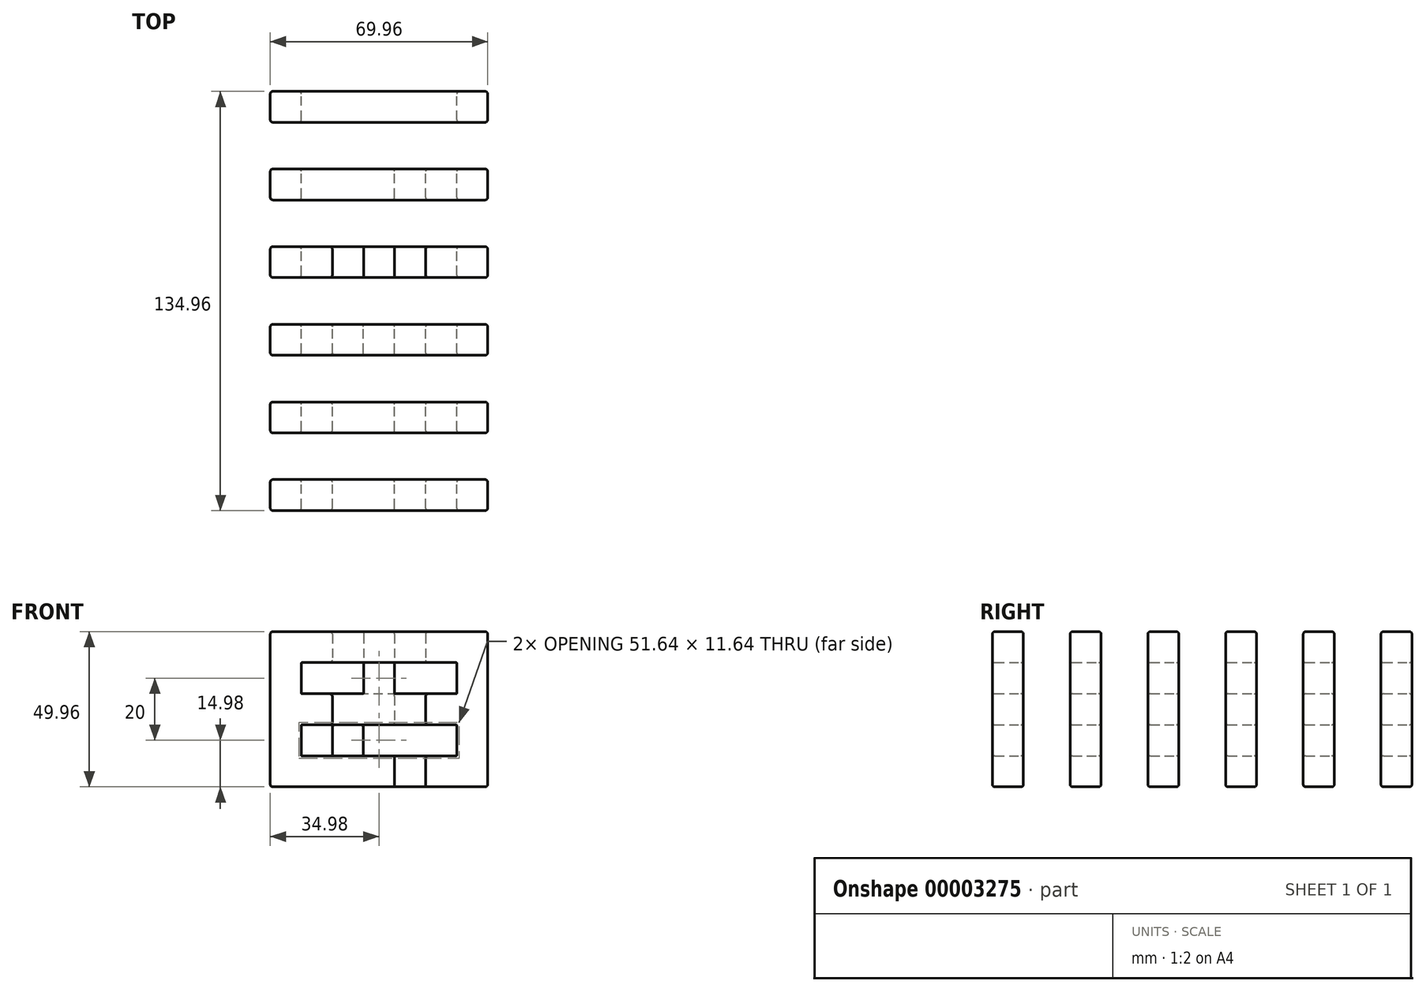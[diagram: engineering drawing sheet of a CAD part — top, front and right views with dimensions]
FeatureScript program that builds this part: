
annotation { "Feature Type Name" : "Feature", "Feature Type Description" : "" }
export const myFeature = defineFeature(function(context is Context, id is Id, definition is map)
    precondition{}
    {
        {
            var Q0;
            Q0=qCreatedBy(makeId("Front.planeOp"),FACE);
            var sketch = newSketch(context, id + "F0", { "sketchPlane" : qUnion([Q0])});
            skLineSegment(sketch, "E0", {"start": v(-35, 25) * mm, "end": v(-25, 25) * mm, "construction": true});
            skLineSegment(sketch, "E1", {"start": v(-25, 25) * mm, "end": v(-15, 25) * mm, "construction": true});
            skLineSegment(sketch, "E2", {"start": v(-15, 25) * mm, "end": v(-5, 25) * mm, "construction": true});
            skLineSegment(sketch, "E3", {"start": v(-5, 25) * mm, "end": v(5, 25) * mm, "construction": true});
            skLineSegment(sketch, "E4", {"start": v(5, 25) * mm, "end": v(15, 25) * mm, "construction": true});
            skLineSegment(sketch, "E5", {"start": v(15, 25) * mm, "end": v(25, 25) * mm, "construction": true});
            skLineSegment(sketch, "E6", {"start": v(25, 25) * mm, "end": v(35, 25) * mm, "construction": true});
            skLineSegment(sketch, "E7", {"start": v(-35, 25) * mm, "end": v(-35, 15) * mm, "construction": true});
            skLineSegment(sketch, "E8", {"start": v(-35, 15) * mm, "end": v(-35, 5) * mm, "construction": true});
            skLineSegment(sketch, "E9", {"start": v(-35, 5) * mm, "end": v(-35, -5) * mm, "construction": true});
            skLineSegment(sketch, "E10", {"start": v(-35, -5) * mm, "end": v(-35, -15) * mm, "construction": true});
            skLineSegment(sketch, "E11", {"start": v(-35, -15) * mm, "end": v(-35, -25) * mm, "construction": true});
            skLineSegment(sketch, "E12", {"start": v(-35, 25) * mm, "end": v(-34.98, 25) * mm, "construction": true});
            skLineSegment(sketch, "E13", {"start": v(-25.02, 25) * mm, "end": v(-25, 25) * mm, "construction": true});
            skLineSegment(sketch, "E14", {"start": v(-25, 25) * mm, "end": v(-24.98, 25) * mm, "construction": true});
            skLineSegment(sketch, "E15", {"start": v(-15.02, 25) * mm, "end": v(-15, 25) * mm, "construction": true});
            skLineSegment(sketch, "E16", {"start": v(-15, 25) * mm, "end": v(-14.98, 25) * mm, "construction": true});
            skLineSegment(sketch, "E17", {"start": v(-5, 25) * mm, "end": v(-5.02, 25) * mm, "construction": true});
            skLineSegment(sketch, "E18", {"start": v(-5, 25) * mm, "end": v(-4.98, 25) * mm, "construction": true});
            skLineSegment(sketch, "E19", {"start": v(5, 25) * mm, "end": v(4.98, 25) * mm, "construction": true});
            skLineSegment(sketch, "E20", {"start": v(5, 25) * mm, "end": v(5.02, 25) * mm, "construction": true});
            skLineSegment(sketch, "E21", {"start": v(15, 25) * mm, "end": v(14.98, 25) * mm, "construction": true});
            skLineSegment(sketch, "E22", {"start": v(15, 25) * mm, "end": v(15.02, 25) * mm, "construction": true});
            skLineSegment(sketch, "E23", {"start": v(25, 25) * mm, "end": v(24.98, 25) * mm, "construction": true});
            skLineSegment(sketch, "E24", {"start": v(25, 25) * mm, "end": v(25.02, 25) * mm, "construction": true});
            skLineSegment(sketch, "E25", {"start": v(35, 25) * mm, "end": v(34.98, 25) * mm, "construction": true});
            skLineSegment(sketch, "E26", {"start": v(-35, 25) * mm, "end": v(-35, 24.98) * mm, "construction": true});
            skLineSegment(sketch, "E27", {"start": v(-35, 15) * mm, "end": v(-35, 15.02) * mm, "construction": true});
            skLineSegment(sketch, "E28", {"start": v(-35, 15) * mm, "end": v(-35, 14.98) * mm, "construction": true});
            skLineSegment(sketch, "E29", {"start": v(-35, 5) * mm, "end": v(-35, 5.02) * mm, "construction": true});
            skLineSegment(sketch, "E30", {"start": v(-35, 5) * mm, "end": v(-35, 4.98) * mm, "construction": true});
            skLineSegment(sketch, "E31", {"start": v(-35, -5) * mm, "end": v(-35, -5.02) * mm, "construction": true});
            skLineSegment(sketch, "E32", {"start": v(-35, -5) * mm, "end": v(-35, -4.98) * mm, "construction": true});
            skLineSegment(sketch, "E33", {"start": v(-35, -15) * mm, "end": v(-35, -14.98) * mm, "construction": true});
            skLineSegment(sketch, "E34", {"start": v(-35, -15) * mm, "end": v(-35, -15.02) * mm, "construction": true});
            skLineSegment(sketch, "E35", {"start": v(-35, -25) * mm, "end": v(-35, -24.98) * mm, "construction": true});
            skLineSegment(sketch, "E36", {"start": v(-35, -24.98) * mm, "end": v(34.98, -24.98) * mm});
            skLineSegment(sketch, "E37", {"start": v(34.98, 25) * mm, "end": v(34.98, -24.98) * mm});
            skLineSegment(sketch, "E38", {"start": v(-35, -15.02) * mm, "end": v(34.98, -15.02) * mm});
            skLineSegment(sketch, "E39", {"start": v(-35, -14.98) * mm, "end": v(34.98, -14.98) * mm});
            skLineSegment(sketch, "E40", {"start": v(-35, -5.02) * mm, "end": v(34.98, -5.02) * mm});
            skLineSegment(sketch, "E41", {"start": v(-35, -4.98) * mm, "end": v(34.98, -4.98) * mm});
            skLineSegment(sketch, "E42", {"start": v(-35, 4.98) * mm, "end": v(34.98, 4.98) * mm});
            skLineSegment(sketch, "E43", {"start": v(-35, 5.02) * mm, "end": v(34.98, 5.02) * mm});
            skLineSegment(sketch, "E44", {"start": v(-35, 14.98) * mm, "end": v(34.98, 14.98) * mm});
            skLineSegment(sketch, "E45", {"start": v(-35, 15.02) * mm, "end": v(34.98, 15.02) * mm});
            skLineSegment(sketch, "E46", {"start": v(-35, 24.98) * mm, "end": v(34.98, 24.98) * mm});
            skLineSegment(sketch, "E47", {"start": v(-34.98, 25) * mm, "end": v(-34.98, -24.98) * mm});
            skLineSegment(sketch, "E48", {"start": v(-25.02, 25) * mm, "end": v(-25.02, -24.98) * mm});
            skLineSegment(sketch, "E49", {"start": v(-24.98, 25) * mm, "end": v(-24.98, -24.98) * mm});
            skLineSegment(sketch, "E50", {"start": v(-15.02, 25) * mm, "end": v(-15.02, -24.98) * mm});
            skLineSegment(sketch, "E51", {"start": v(-14.98, 25) * mm, "end": v(-14.98, -24.98) * mm});
            skLineSegment(sketch, "E52", {"start": v(-5.02, 25) * mm, "end": v(-5.02, -24.98) * mm});
            skLineSegment(sketch, "E53", {"start": v(-4.98, 25) * mm, "end": v(-4.98, -24.98) * mm});
            skLineSegment(sketch, "E54", {"start": v(4.98, 25) * mm, "end": v(4.98, -24.98) * mm});
            skLineSegment(sketch, "E55", {"start": v(5.02, 25) * mm, "end": v(5.02, -24.98) * mm});
            skLineSegment(sketch, "E56", {"start": v(14.98, 25) * mm, "end": v(14.98, -24.98) * mm});
            skLineSegment(sketch, "E57", {"start": v(15.02, 25) * mm, "end": v(15.02, -24.98) * mm});
            skLineSegment(sketch, "E58", {"start": v(24.98, 25) * mm, "end": v(24.98, -24.98) * mm});
            skLineSegment(sketch, "E59", {"start": v(25.02, 25) * mm, "end": v(25.02, -24.98) * mm});
            skLineSegment(sketch, "E60", {"start": v(-4.98, 4.98) * mm, "end": v(4.98, -4.98) * mm, "construction": true});
            skSolve(sketch);
        }
        {
            var Q0;
            {var subQ1=sQuery(id+"F0.wireOp",EDGE,"E45");var subQ5=sQuery(id+"F0.wireOp",EDGE,"E47");var subQ6=makeQuery(id+"F0.imprint","INTERSECT",VERTEX,{"derivedFrom":[subQ1,subQ5]});Q0=makeQuery(id+"F0.imprint","IMPRINT",FACE,{"disambiguationData":[TD([[makeQuery(id+"F0.imprint","IMPRINT",EDGE,{"disambiguationData":[TD([[subQ6,-1.0]])],"derivedFrom":subQ1}),1.0]])]});}
            var Q1;
            {var subQ1=sQuery(id+"F0.wireOp",EDGE,"E45");var subQ5=sQuery(id+"F0.wireOp",EDGE,"E48");var subQ6=makeQuery(id+"F0.imprint","INTERSECT",VERTEX,{"derivedFrom":[subQ1,subQ5]});Q1=makeQuery(id+"F0.imprint","IMPRINT",FACE,{"disambiguationData":[TD([[makeQuery(id+"F0.imprint","IMPRINT",EDGE,{"disambiguationData":[TD([[subQ6,-1.0]])],"derivedFrom":subQ1}),1.0]])]});}
            var Q2;
            {var subQ1=sQuery(id+"F0.wireOp",EDGE,"E45");var subQ5=sQuery(id+"F0.wireOp",EDGE,"E49");var subQ6=makeQuery(id+"F0.imprint","INTERSECT",VERTEX,{"derivedFrom":[subQ1,subQ5]});Q2=makeQuery(id+"F0.imprint","IMPRINT",FACE,{"disambiguationData":[TD([[makeQuery(id+"F0.imprint","IMPRINT",EDGE,{"disambiguationData":[TD([[subQ6,-1.0]])],"derivedFrom":subQ1}),1.0]])]});}
            var Q3;
            {var subQ1=sQuery(id+"F0.wireOp",EDGE,"E45");var subQ5=sQuery(id+"F0.wireOp",EDGE,"E50");var subQ6=makeQuery(id+"F0.imprint","INTERSECT",VERTEX,{"derivedFrom":[subQ1,subQ5]});Q3=makeQuery(id+"F0.imprint","IMPRINT",FACE,{"disambiguationData":[TD([[makeQuery(id+"F0.imprint","IMPRINT",EDGE,{"disambiguationData":[TD([[subQ6,-1.0]])],"derivedFrom":subQ1}),1.0]])]});}
            var Q4;
            {var subQ1=sQuery(id+"F0.wireOp",EDGE,"E45");var subQ5=sQuery(id+"F0.wireOp",EDGE,"E51");var subQ6=makeQuery(id+"F0.imprint","INTERSECT",VERTEX,{"derivedFrom":[subQ1,subQ5]});Q4=makeQuery(id+"F0.imprint","IMPRINT",FACE,{"disambiguationData":[TD([[makeQuery(id+"F0.imprint","IMPRINT",EDGE,{"disambiguationData":[TD([[subQ6,-1.0]])],"derivedFrom":subQ1}),1.0]])]});}
            var Q5;
            {var subQ1=sQuery(id+"F0.wireOp",EDGE,"E45");var subQ5=sQuery(id+"F0.wireOp",EDGE,"E52");var subQ6=makeQuery(id+"F0.imprint","INTERSECT",VERTEX,{"derivedFrom":[subQ1,subQ5]});Q5=makeQuery(id+"F0.imprint","IMPRINT",FACE,{"disambiguationData":[TD([[makeQuery(id+"F0.imprint","IMPRINT",EDGE,{"disambiguationData":[TD([[subQ6,-1.0]])],"derivedFrom":subQ1}),1.0]])]});}
            var Q6;
            {var subQ1=sQuery(id+"F0.wireOp",EDGE,"E45");var subQ5=sQuery(id+"F0.wireOp",EDGE,"E53");var subQ6=makeQuery(id+"F0.imprint","INTERSECT",VERTEX,{"derivedFrom":[subQ1,subQ5]});Q6=makeQuery(id+"F0.imprint","IMPRINT",FACE,{"disambiguationData":[TD([[makeQuery(id+"F0.imprint","IMPRINT",EDGE,{"disambiguationData":[TD([[subQ6,-1.0]])],"derivedFrom":subQ1}),1.0]])]});}
            var Q7;
            {var subQ1=sQuery(id+"F0.wireOp",EDGE,"E45");var subQ5=sQuery(id+"F0.wireOp",EDGE,"E54");var subQ6=makeQuery(id+"F0.imprint","INTERSECT",VERTEX,{"derivedFrom":[subQ1,subQ5]});Q7=makeQuery(id+"F0.imprint","IMPRINT",FACE,{"disambiguationData":[TD([[makeQuery(id+"F0.imprint","IMPRINT",EDGE,{"disambiguationData":[TD([[subQ6,-1.0]])],"derivedFrom":subQ1}),1.0]])]});}
            var Q8;
            {var subQ1=sQuery(id+"F0.wireOp",EDGE,"E45");var subQ5=sQuery(id+"F0.wireOp",EDGE,"E55");var subQ6=makeQuery(id+"F0.imprint","INTERSECT",VERTEX,{"derivedFrom":[subQ1,subQ5]});Q8=makeQuery(id+"F0.imprint","IMPRINT",FACE,{"disambiguationData":[TD([[makeQuery(id+"F0.imprint","IMPRINT",EDGE,{"disambiguationData":[TD([[subQ6,-1.0]])],"derivedFrom":subQ1}),1.0]])]});}
            var Q9;
            {var subQ0=sQuery(id+"F0.wireOp",EDGE,"E56");var subQ1=sQuery(id+"F0.wireOp",EDGE,"E45");var subQ2=makeQuery(id+"F0.imprint","INTERSECT",VERTEX,{"derivedFrom":[subQ1,subQ0]});Q9=makeQuery(id+"F0.imprint","IMPRINT",FACE,{"disambiguationData":[TD([[makeQuery(id+"F0.imprint","IMPRINT",EDGE,{"disambiguationData":[TD([[subQ2,-1.0]])],"derivedFrom":subQ1}),1.0]])]});}
            var Q10;
            {var subQ1=sQuery(id+"F0.wireOp",EDGE,"E45");var subQ5=sQuery(id+"F0.wireOp",EDGE,"E57");var subQ6=makeQuery(id+"F0.imprint","INTERSECT",VERTEX,{"derivedFrom":[subQ1,subQ5]});Q10=makeQuery(id+"F0.imprint","IMPRINT",FACE,{"disambiguationData":[TD([[makeQuery(id+"F0.imprint","IMPRINT",EDGE,{"disambiguationData":[TD([[subQ6,-1.0]])],"derivedFrom":subQ1}),1.0]])]});}
            var Q11;
            {var subQ0=sQuery(id+"F0.wireOp",EDGE,"E58");var subQ1=sQuery(id+"F0.wireOp",EDGE,"E45");var subQ2=makeQuery(id+"F0.imprint","INTERSECT",VERTEX,{"derivedFrom":[subQ1,subQ0]});Q11=makeQuery(id+"F0.imprint","IMPRINT",FACE,{"disambiguationData":[TD([[makeQuery(id+"F0.imprint","IMPRINT",EDGE,{"disambiguationData":[TD([[subQ2,-1.0]])],"derivedFrom":subQ1}),1.0]])]});}
            var Q12;
            {var subQ1=sQuery(id+"F0.wireOp",EDGE,"E45");var subQ5=sQuery(id+"F0.wireOp",EDGE,"E37");var subQ7=makeQuery(id+"F0.imprint","INTERSECT",VERTEX,{"derivedFrom":[subQ5,subQ1]});Q12=makeQuery(id+"F0.imprint","IMPRINT",FACE,{"disambiguationData":[TD([[makeQuery(id+"F0.imprint","IMPRINT",EDGE,{"disambiguationData":[TD([[subQ7,1.0]])],"derivedFrom":subQ5}),-1.0]])]});}
            var Q13;
            {var subQ3=sQuery(id+"F0.wireOp",EDGE,"E44");var subQ5=sQuery(id+"F0.wireOp",EDGE,"E37");var subQ7=makeQuery(id+"F0.imprint","INTERSECT",VERTEX,{"derivedFrom":[subQ5,subQ3]});Q13=makeQuery(id+"F0.imprint","IMPRINT",FACE,{"disambiguationData":[TD([[makeQuery(id+"F0.imprint","IMPRINT",EDGE,{"disambiguationData":[TD([[subQ7,1.0]])],"derivedFrom":subQ5}),-1.0]])]});}
            var Q14;
            {var subQ3=sQuery(id+"F0.wireOp",EDGE,"E43");var subQ5=sQuery(id+"F0.wireOp",EDGE,"E37");var subQ7=makeQuery(id+"F0.imprint","INTERSECT",VERTEX,{"derivedFrom":[subQ5,subQ3]});Q14=makeQuery(id+"F0.imprint","IMPRINT",FACE,{"disambiguationData":[TD([[makeQuery(id+"F0.imprint","IMPRINT",EDGE,{"disambiguationData":[TD([[subQ7,1.0]])],"derivedFrom":subQ5}),-1.0]])]});}
            var Q15;
            {var subQ3=sQuery(id+"F0.wireOp",EDGE,"E42");var subQ5=sQuery(id+"F0.wireOp",EDGE,"E37");var subQ7=makeQuery(id+"F0.imprint","INTERSECT",VERTEX,{"derivedFrom":[subQ5,subQ3]});Q15=makeQuery(id+"F0.imprint","IMPRINT",FACE,{"disambiguationData":[TD([[makeQuery(id+"F0.imprint","IMPRINT",EDGE,{"disambiguationData":[TD([[subQ7,1.0]])],"derivedFrom":subQ5}),-1.0]])]});}
            var Q16;
            {var subQ3=sQuery(id+"F0.wireOp",EDGE,"E41");var subQ5=sQuery(id+"F0.wireOp",EDGE,"E37");var subQ7=makeQuery(id+"F0.imprint","INTERSECT",VERTEX,{"derivedFrom":[subQ5,subQ3]});Q16=makeQuery(id+"F0.imprint","IMPRINT",FACE,{"disambiguationData":[TD([[makeQuery(id+"F0.imprint","IMPRINT",EDGE,{"disambiguationData":[TD([[subQ7,1.0]])],"derivedFrom":subQ5}),-1.0]])]});}
            var Q17;
            {var subQ3=sQuery(id+"F0.wireOp",EDGE,"E40");var subQ5=sQuery(id+"F0.wireOp",EDGE,"E37");var subQ7=makeQuery(id+"F0.imprint","INTERSECT",VERTEX,{"derivedFrom":[subQ5,subQ3]});Q17=makeQuery(id+"F0.imprint","IMPRINT",FACE,{"disambiguationData":[TD([[makeQuery(id+"F0.imprint","IMPRINT",EDGE,{"disambiguationData":[TD([[subQ7,1.0]])],"derivedFrom":subQ5}),-1.0]])]});}
            var Q18;
            {var subQ3=sQuery(id+"F0.wireOp",EDGE,"E39");var subQ5=sQuery(id+"F0.wireOp",EDGE,"E37");var subQ7=makeQuery(id+"F0.imprint","INTERSECT",VERTEX,{"derivedFrom":[subQ5,subQ3]});Q18=makeQuery(id+"F0.imprint","IMPRINT",FACE,{"disambiguationData":[TD([[makeQuery(id+"F0.imprint","IMPRINT",EDGE,{"disambiguationData":[TD([[subQ7,1.0]])],"derivedFrom":subQ5}),-1.0]])]});}
            var Q19;
            {var subQ3=sQuery(id+"F0.wireOp",EDGE,"E38");var subQ5=sQuery(id+"F0.wireOp",EDGE,"E37");var subQ7=makeQuery(id+"F0.imprint","INTERSECT",VERTEX,{"derivedFrom":[subQ5,subQ3]});Q19=makeQuery(id+"F0.imprint","IMPRINT",FACE,{"disambiguationData":[TD([[makeQuery(id+"F0.imprint","IMPRINT",EDGE,{"disambiguationData":[TD([[subQ7,1.0]])],"derivedFrom":subQ5}),-1.0]])]});}
            var Q20;
            {var subQ3=sQuery(id+"F0.wireOp",EDGE,"E36");var subQ5=sQuery(id+"F0.wireOp",EDGE,"E37");var subQ7=makeQuery(id+"F0.imprint","INTERSECT",VERTEX,{"derivedFrom":[subQ3,subQ5]});Q20=makeQuery(id+"F0.imprint","IMPRINT",FACE,{"disambiguationData":[TD([[makeQuery(id+"F0.imprint","IMPRINT",EDGE,{"disambiguationData":[TD([[subQ7,1.0]])],"derivedFrom":subQ3}),1.0]])]});}
            var Q21;
            {var subQ3=sQuery(id+"F0.wireOp",EDGE,"E36");var subQ5=sQuery(id+"F0.wireOp",EDGE,"E58");var subQ7=makeQuery(id+"F0.imprint","INTERSECT",VERTEX,{"derivedFrom":[subQ3,subQ5]});Q21=makeQuery(id+"F0.imprint","IMPRINT",FACE,{"disambiguationData":[TD([[makeQuery(id+"F0.imprint","IMPRINT",EDGE,{"disambiguationData":[TD([[subQ7,-1.0]])],"derivedFrom":subQ3}),1.0]])]});}
            var Q22;
            {var subQ3=sQuery(id+"F0.wireOp",EDGE,"E36");var subQ5=sQuery(id+"F0.wireOp",EDGE,"E57");var subQ7=makeQuery(id+"F0.imprint","INTERSECT",VERTEX,{"derivedFrom":[subQ3,subQ5]});Q22=makeQuery(id+"F0.imprint","IMPRINT",FACE,{"disambiguationData":[TD([[makeQuery(id+"F0.imprint","IMPRINT",EDGE,{"disambiguationData":[TD([[subQ7,-1.0]])],"derivedFrom":subQ3}),1.0]])]});}
            var Q23;
            {var subQ3=sQuery(id+"F0.wireOp",EDGE,"E36");var subQ5=sQuery(id+"F0.wireOp",EDGE,"E56");var subQ7=makeQuery(id+"F0.imprint","INTERSECT",VERTEX,{"derivedFrom":[subQ3,subQ5]});Q23=makeQuery(id+"F0.imprint","IMPRINT",FACE,{"disambiguationData":[TD([[makeQuery(id+"F0.imprint","IMPRINT",EDGE,{"disambiguationData":[TD([[subQ7,-1.0]])],"derivedFrom":subQ3}),1.0]])]});}
            var Q24;
            {var subQ3=sQuery(id+"F0.wireOp",EDGE,"E36");var subQ5=sQuery(id+"F0.wireOp",EDGE,"E49");var subQ7=makeQuery(id+"F0.imprint","INTERSECT",VERTEX,{"derivedFrom":[subQ3,subQ5]});Q24=makeQuery(id+"F0.imprint","IMPRINT",FACE,{"disambiguationData":[TD([[makeQuery(id+"F0.imprint","IMPRINT",EDGE,{"disambiguationData":[TD([[subQ7,-1.0]])],"derivedFrom":subQ3}),1.0]])]});}
            var Q25;
            {var subQ3=sQuery(id+"F0.wireOp",EDGE,"E36");var subQ5=sQuery(id+"F0.wireOp",EDGE,"E47");var subQ7=makeQuery(id+"F0.imprint","INTERSECT",VERTEX,{"derivedFrom":[subQ3,subQ5]});Q25=makeQuery(id+"F0.imprint","IMPRINT",FACE,{"disambiguationData":[TD([[makeQuery(id+"F0.imprint","IMPRINT",EDGE,{"disambiguationData":[TD([[subQ7,-1.0]])],"derivedFrom":subQ3}),1.0]])]});}
            var Q26;
            {var subQ3=sQuery(id+"F0.wireOp",EDGE,"E36");var subQ5=sQuery(id+"F0.wireOp",EDGE,"E48");var subQ7=makeQuery(id+"F0.imprint","INTERSECT",VERTEX,{"derivedFrom":[subQ3,subQ5]});Q26=makeQuery(id+"F0.imprint","IMPRINT",FACE,{"disambiguationData":[TD([[makeQuery(id+"F0.imprint","IMPRINT",EDGE,{"disambiguationData":[TD([[subQ7,-1.0]])],"derivedFrom":subQ3}),1.0]])]});}
            var Q27;
            {var subQ3=sQuery(id+"F0.wireOp",EDGE,"E36");var subQ5=sQuery(id+"F0.wireOp",EDGE,"E55");var subQ7=makeQuery(id+"F0.imprint","INTERSECT",VERTEX,{"derivedFrom":[subQ3,subQ5]});Q27=makeQuery(id+"F0.imprint","IMPRINT",FACE,{"disambiguationData":[TD([[makeQuery(id+"F0.imprint","IMPRINT",EDGE,{"disambiguationData":[TD([[subQ7,-1.0]])],"derivedFrom":subQ3}),1.0]])]});}
            var Q28;
            {var subQ3=sQuery(id+"F0.wireOp",EDGE,"E36");var subQ5=sQuery(id+"F0.wireOp",EDGE,"E54");var subQ7=makeQuery(id+"F0.imprint","INTERSECT",VERTEX,{"derivedFrom":[subQ3,subQ5]});Q28=makeQuery(id+"F0.imprint","IMPRINT",FACE,{"disambiguationData":[TD([[makeQuery(id+"F0.imprint","IMPRINT",EDGE,{"disambiguationData":[TD([[subQ7,-1.0]])],"derivedFrom":subQ3}),1.0]])]});}
            var Q29;
            {var subQ3=sQuery(id+"F0.wireOp",EDGE,"E36");var subQ5=sQuery(id+"F0.wireOp",EDGE,"E53");var subQ7=makeQuery(id+"F0.imprint","INTERSECT",VERTEX,{"derivedFrom":[subQ3,subQ5]});Q29=makeQuery(id+"F0.imprint","IMPRINT",FACE,{"disambiguationData":[TD([[makeQuery(id+"F0.imprint","IMPRINT",EDGE,{"disambiguationData":[TD([[subQ7,-1.0]])],"derivedFrom":subQ3}),1.0]])]});}
            var Q30;
            {var subQ3=sQuery(id+"F0.wireOp",EDGE,"E36");var subQ5=sQuery(id+"F0.wireOp",EDGE,"E52");var subQ7=makeQuery(id+"F0.imprint","INTERSECT",VERTEX,{"derivedFrom":[subQ3,subQ5]});Q30=makeQuery(id+"F0.imprint","IMPRINT",FACE,{"disambiguationData":[TD([[makeQuery(id+"F0.imprint","IMPRINT",EDGE,{"disambiguationData":[TD([[subQ7,-1.0]])],"derivedFrom":subQ3}),1.0]])]});}
            var Q31;
            {var subQ3=sQuery(id+"F0.wireOp",EDGE,"E36");var subQ5=sQuery(id+"F0.wireOp",EDGE,"E51");var subQ7=makeQuery(id+"F0.imprint","INTERSECT",VERTEX,{"derivedFrom":[subQ3,subQ5]});Q31=makeQuery(id+"F0.imprint","IMPRINT",FACE,{"disambiguationData":[TD([[makeQuery(id+"F0.imprint","IMPRINT",EDGE,{"disambiguationData":[TD([[subQ7,-1.0]])],"derivedFrom":subQ3}),1.0]])]});}
            var Q32;
            {var subQ3=sQuery(id+"F0.wireOp",EDGE,"E36");var subQ5=sQuery(id+"F0.wireOp",EDGE,"E50");var subQ7=makeQuery(id+"F0.imprint","INTERSECT",VERTEX,{"derivedFrom":[subQ3,subQ5]});Q32=makeQuery(id+"F0.imprint","IMPRINT",FACE,{"disambiguationData":[TD([[makeQuery(id+"F0.imprint","IMPRINT",EDGE,{"disambiguationData":[TD([[subQ7,-1.0]])],"derivedFrom":subQ3}),1.0]])]});}
            var Q33;
            {var subQ3=sQuery(id+"F0.wireOp",EDGE,"E40");var subQ5=sQuery(id+"F0.wireOp",EDGE,"E47");var subQ7=makeQuery(id+"F0.imprint","INTERSECT",VERTEX,{"derivedFrom":[subQ3,subQ5]});Q33=makeQuery(id+"F0.imprint","IMPRINT",FACE,{"disambiguationData":[TD([[makeQuery(id+"F0.imprint","IMPRINT",EDGE,{"disambiguationData":[TD([[subQ7,-1.0]])],"derivedFrom":subQ3}),1.0]])]});}
            var Q34;
            {var subQ3=sQuery(id+"F0.wireOp",EDGE,"E41");var subQ5=sQuery(id+"F0.wireOp",EDGE,"E47");var subQ7=makeQuery(id+"F0.imprint","INTERSECT",VERTEX,{"derivedFrom":[subQ3,subQ5]});Q34=makeQuery(id+"F0.imprint","IMPRINT",FACE,{"disambiguationData":[TD([[makeQuery(id+"F0.imprint","IMPRINT",EDGE,{"disambiguationData":[TD([[subQ7,-1.0]])],"derivedFrom":subQ3}),1.0]])]});}
            var Q35;
            {var subQ3=sQuery(id+"F0.wireOp",EDGE,"E44");var subQ5=sQuery(id+"F0.wireOp",EDGE,"E47");var subQ7=makeQuery(id+"F0.imprint","INTERSECT",VERTEX,{"derivedFrom":[subQ3,subQ5]});Q35=makeQuery(id+"F0.imprint","IMPRINT",FACE,{"disambiguationData":[TD([[makeQuery(id+"F0.imprint","IMPRINT",EDGE,{"disambiguationData":[TD([[subQ7,-1.0]])],"derivedFrom":subQ3}),1.0]])]});}
            var Q36;
            {var subQ3=sQuery(id+"F0.wireOp",EDGE,"E42");var subQ5=sQuery(id+"F0.wireOp",EDGE,"E47");var subQ7=makeQuery(id+"F0.imprint","INTERSECT",VERTEX,{"derivedFrom":[subQ3,subQ5]});Q36=makeQuery(id+"F0.imprint","IMPRINT",FACE,{"disambiguationData":[TD([[makeQuery(id+"F0.imprint","IMPRINT",EDGE,{"disambiguationData":[TD([[subQ7,-1.0]])],"derivedFrom":subQ3}),1.0]])]});}
            var Q37;
            {var subQ3=sQuery(id+"F0.wireOp",EDGE,"E38");var subQ5=sQuery(id+"F0.wireOp",EDGE,"E47");var subQ7=makeQuery(id+"F0.imprint","INTERSECT",VERTEX,{"derivedFrom":[subQ3,subQ5]});Q37=makeQuery(id+"F0.imprint","IMPRINT",FACE,{"disambiguationData":[TD([[makeQuery(id+"F0.imprint","IMPRINT",EDGE,{"disambiguationData":[TD([[subQ7,-1.0]])],"derivedFrom":subQ3}),1.0]])]});}
            var Q38;
            {var subQ3=sQuery(id+"F0.wireOp",EDGE,"E39");var subQ5=sQuery(id+"F0.wireOp",EDGE,"E47");var subQ7=makeQuery(id+"F0.imprint","INTERSECT",VERTEX,{"derivedFrom":[subQ3,subQ5]});Q38=makeQuery(id+"F0.imprint","IMPRINT",FACE,{"disambiguationData":[TD([[makeQuery(id+"F0.imprint","IMPRINT",EDGE,{"disambiguationData":[TD([[subQ7,-1.0]])],"derivedFrom":subQ3}),1.0]])]});}
            var Q39;
            {var subQ3=sQuery(id+"F0.wireOp",EDGE,"E43");var subQ5=sQuery(id+"F0.wireOp",EDGE,"E47");var subQ7=makeQuery(id+"F0.imprint","INTERSECT",VERTEX,{"derivedFrom":[subQ3,subQ5]});Q39=makeQuery(id+"F0.imprint","IMPRINT",FACE,{"disambiguationData":[TD([[makeQuery(id+"F0.imprint","IMPRINT",EDGE,{"disambiguationData":[TD([[subQ7,-1.0]])],"derivedFrom":subQ3}),1.0]])]});}
            var Q40;
            {var subQ3=sQuery(id+"F0.wireOp",EDGE,"E41");var subQ5=sQuery(id+"F0.wireOp",EDGE,"E56");var subQ7=makeQuery(id+"F0.imprint","INTERSECT",VERTEX,{"derivedFrom":[subQ3,subQ5]});Q40=makeQuery(id+"F0.imprint","IMPRINT",FACE,{"disambiguationData":[TD([[makeQuery(id+"F0.imprint","IMPRINT",EDGE,{"disambiguationData":[TD([[subQ7,-1.0]])],"derivedFrom":subQ3}),1.0]])]});}
            var Q41;
            {var subQ3=sQuery(id+"F0.wireOp",EDGE,"E41");var subQ5=sQuery(id+"F0.wireOp",EDGE,"E57");var subQ7=makeQuery(id+"F0.imprint","INTERSECT",VERTEX,{"derivedFrom":[subQ3,subQ5]});Q41=makeQuery(id+"F0.imprint","IMPRINT",FACE,{"disambiguationData":[TD([[makeQuery(id+"F0.imprint","IMPRINT",EDGE,{"disambiguationData":[TD([[subQ7,-1.0]])],"derivedFrom":subQ3}),1.0]])]});}
            var Q42;
            {var subQ3=sQuery(id+"F0.wireOp",EDGE,"E41");var subQ5=sQuery(id+"F0.wireOp",EDGE,"E52");var subQ7=makeQuery(id+"F0.imprint","INTERSECT",VERTEX,{"derivedFrom":[subQ3,subQ5]});Q42=makeQuery(id+"F0.imprint","IMPRINT",FACE,{"disambiguationData":[TD([[makeQuery(id+"F0.imprint","IMPRINT",EDGE,{"disambiguationData":[TD([[subQ7,-1.0]])],"derivedFrom":subQ3}),1.0]])]});}
            var Q43;
            {var subQ3=sQuery(id+"F0.wireOp",EDGE,"E41");var subQ5=sQuery(id+"F0.wireOp",EDGE,"E48");var subQ7=makeQuery(id+"F0.imprint","INTERSECT",VERTEX,{"derivedFrom":[subQ3,subQ5]});Q43=makeQuery(id+"F0.imprint","IMPRINT",FACE,{"disambiguationData":[TD([[makeQuery(id+"F0.imprint","IMPRINT",EDGE,{"disambiguationData":[TD([[subQ7,-1.0]])],"derivedFrom":subQ3}),1.0]])]});}
            var Q44;
            {var subQ3=sQuery(id+"F0.wireOp",EDGE,"E41");var subQ5=sQuery(id+"F0.wireOp",EDGE,"E51");var subQ7=makeQuery(id+"F0.imprint","INTERSECT",VERTEX,{"derivedFrom":[subQ3,subQ5]});Q44=makeQuery(id+"F0.imprint","IMPRINT",FACE,{"disambiguationData":[TD([[makeQuery(id+"F0.imprint","IMPRINT",EDGE,{"disambiguationData":[TD([[subQ7,-1.0]])],"derivedFrom":subQ3}),1.0]])]});}
            var Q45;
            {var subQ3=sQuery(id+"F0.wireOp",EDGE,"E41");var subQ5=sQuery(id+"F0.wireOp",EDGE,"E54");var subQ7=makeQuery(id+"F0.imprint","INTERSECT",VERTEX,{"derivedFrom":[subQ3,subQ5]});Q45=makeQuery(id+"F0.imprint","IMPRINT",FACE,{"disambiguationData":[TD([[makeQuery(id+"F0.imprint","IMPRINT",EDGE,{"disambiguationData":[TD([[subQ7,-1.0]])],"derivedFrom":subQ3}),1.0]])]});}
            var Q46;
            {var subQ3=sQuery(id+"F0.wireOp",EDGE,"E41");var subQ5=sQuery(id+"F0.wireOp",EDGE,"E49");var subQ7=makeQuery(id+"F0.imprint","INTERSECT",VERTEX,{"derivedFrom":[subQ3,subQ5]});Q46=makeQuery(id+"F0.imprint","IMPRINT",FACE,{"disambiguationData":[TD([[makeQuery(id+"F0.imprint","IMPRINT",EDGE,{"disambiguationData":[TD([[subQ7,-1.0]])],"derivedFrom":subQ3}),1.0]])]});}
            var Q47;
            {var subQ3=sQuery(id+"F0.wireOp",EDGE,"E41");var subQ5=sQuery(id+"F0.wireOp",EDGE,"E50");var subQ7=makeQuery(id+"F0.imprint","INTERSECT",VERTEX,{"derivedFrom":[subQ3,subQ5]});Q47=makeQuery(id+"F0.imprint","IMPRINT",FACE,{"disambiguationData":[TD([[makeQuery(id+"F0.imprint","IMPRINT",EDGE,{"disambiguationData":[TD([[subQ7,-1.0]])],"derivedFrom":subQ3}),1.0]])]});}
            var Q48;
            {var subQ3=sQuery(id+"F0.wireOp",EDGE,"E41");var subQ5=sQuery(id+"F0.wireOp",EDGE,"E55");var subQ7=makeQuery(id+"F0.imprint","INTERSECT",VERTEX,{"derivedFrom":[subQ3,subQ5]});Q48=makeQuery(id+"F0.imprint","IMPRINT",FACE,{"disambiguationData":[TD([[makeQuery(id+"F0.imprint","IMPRINT",EDGE,{"disambiguationData":[TD([[subQ7,-1.0]])],"derivedFrom":subQ3}),1.0]])]});}
            var Q49;
            {var subQ3=sQuery(id+"F0.wireOp",EDGE,"E41");var subQ5=sQuery(id+"F0.wireOp",EDGE,"E53");var subQ7=makeQuery(id+"F0.imprint","INTERSECT",VERTEX,{"derivedFrom":[subQ3,subQ5]});Q49=makeQuery(id+"F0.imprint","IMPRINT",FACE,{"disambiguationData":[TD([[makeQuery(id+"F0.imprint","IMPRINT",EDGE,{"disambiguationData":[TD([[subQ7,-1.0]])],"derivedFrom":subQ3}),1.0]])]});}
            var Q50;
            {var subQ0=sQuery(id+"F0.wireOp",EDGE,"E58");var subQ3=sQuery(id+"F0.wireOp",EDGE,"E41");var subQ4=makeQuery(id+"F0.imprint","INTERSECT",VERTEX,{"derivedFrom":[subQ3,subQ0]});Q50=makeQuery(id+"F0.imprint","IMPRINT",FACE,{"disambiguationData":[TD([[makeQuery(id+"F0.imprint","IMPRINT",EDGE,{"disambiguationData":[TD([[subQ4,-1.0]])],"derivedFrom":subQ3}),1.0]])]});}
            extrude(context, id + "F1", {"entities" : qUnion([Q0, Q1, Q2, Q3, Q4, Q5, Q6, Q7, Q8, Q9, Q10, Q11, Q12, Q13, Q14, Q15, Q16, Q17, Q18, Q19, Q20, Q21, Q22, Q23, Q24, Q25, Q26, Q27, Q28, Q29, Q30, Q31, Q32, Q33, Q34, Q35, Q36, Q37, Q38, Q39, Q40, Q41, Q42, Q43, Q44, Q45, Q46, Q47, Q48, Q49, Q50]), "endBound" : BoundingType.SYMMETRIC, "depth" : 9.96 * mm});
        }
        {
            var Q0;
            {var subQ1=sQuery(id+"F0.wireOp",EDGE,"E45");var subQ5=sQuery(id+"F0.wireOp",EDGE,"E53");var subQ6=makeQuery(id+"F0.imprint","INTERSECT",VERTEX,{"derivedFrom":[subQ1,subQ5]});Q0=makeQuery(id+"F0.imprint","IMPRINT",FACE,{"disambiguationData":[TD([[makeQuery(id+"F0.imprint","IMPRINT",EDGE,{"disambiguationData":[TD([[subQ6,-1.0]])],"derivedFrom":subQ1}),1.0]])]});}
            var Q1;
            {var subQ1=sQuery(id+"F0.wireOp",EDGE,"E45");var subQ5=sQuery(id+"F0.wireOp",EDGE,"E48");var subQ6=makeQuery(id+"F0.imprint","INTERSECT",VERTEX,{"derivedFrom":[subQ1,subQ5]});Q1=makeQuery(id+"F0.imprint","IMPRINT",FACE,{"disambiguationData":[TD([[makeQuery(id+"F0.imprint","IMPRINT",EDGE,{"disambiguationData":[TD([[subQ6,-1.0]])],"derivedFrom":subQ1}),1.0]])]});}
            var Q2;
            {var subQ1=sQuery(id+"F0.wireOp",EDGE,"E45");var subQ5=sQuery(id+"F0.wireOp",EDGE,"E52");var subQ6=makeQuery(id+"F0.imprint","INTERSECT",VERTEX,{"derivedFrom":[subQ1,subQ5]});Q2=makeQuery(id+"F0.imprint","IMPRINT",FACE,{"disambiguationData":[TD([[makeQuery(id+"F0.imprint","IMPRINT",EDGE,{"disambiguationData":[TD([[subQ6,-1.0]])],"derivedFrom":subQ1}),1.0]])]});}
            var Q3;
            {var subQ1=sQuery(id+"F0.wireOp",EDGE,"E45");var subQ5=sQuery(id+"F0.wireOp",EDGE,"E47");var subQ6=makeQuery(id+"F0.imprint","INTERSECT",VERTEX,{"derivedFrom":[subQ1,subQ5]});Q3=makeQuery(id+"F0.imprint","IMPRINT",FACE,{"disambiguationData":[TD([[makeQuery(id+"F0.imprint","IMPRINT",EDGE,{"disambiguationData":[TD([[subQ6,-1.0]])],"derivedFrom":subQ1}),1.0]])]});}
            var Q4;
            {var subQ1=sQuery(id+"F0.wireOp",EDGE,"E45");var subQ5=sQuery(id+"F0.wireOp",EDGE,"E54");var subQ6=makeQuery(id+"F0.imprint","INTERSECT",VERTEX,{"derivedFrom":[subQ1,subQ5]});Q4=makeQuery(id+"F0.imprint","IMPRINT",FACE,{"disambiguationData":[TD([[makeQuery(id+"F0.imprint","IMPRINT",EDGE,{"disambiguationData":[TD([[subQ6,-1.0]])],"derivedFrom":subQ1}),1.0]])]});}
            var Q5;
            {var subQ1=sQuery(id+"F0.wireOp",EDGE,"E45");var subQ5=sQuery(id+"F0.wireOp",EDGE,"E37");var subQ7=makeQuery(id+"F0.imprint","INTERSECT",VERTEX,{"derivedFrom":[subQ5,subQ1]});Q5=makeQuery(id+"F0.imprint","IMPRINT",FACE,{"disambiguationData":[TD([[makeQuery(id+"F0.imprint","IMPRINT",EDGE,{"disambiguationData":[TD([[subQ7,1.0]])],"derivedFrom":subQ5}),-1.0]])]});}
            var Q6;
            {var subQ1=sQuery(id+"F0.wireOp",EDGE,"E45");var subQ5=sQuery(id+"F0.wireOp",EDGE,"E55");var subQ6=makeQuery(id+"F0.imprint","INTERSECT",VERTEX,{"derivedFrom":[subQ1,subQ5]});Q6=makeQuery(id+"F0.imprint","IMPRINT",FACE,{"disambiguationData":[TD([[makeQuery(id+"F0.imprint","IMPRINT",EDGE,{"disambiguationData":[TD([[subQ6,-1.0]])],"derivedFrom":subQ1}),1.0]])]});}
            var Q7;
            {var subQ1=sQuery(id+"F0.wireOp",EDGE,"E45");var subQ5=sQuery(id+"F0.wireOp",EDGE,"E50");var subQ6=makeQuery(id+"F0.imprint","INTERSECT",VERTEX,{"derivedFrom":[subQ1,subQ5]});Q7=makeQuery(id+"F0.imprint","IMPRINT",FACE,{"disambiguationData":[TD([[makeQuery(id+"F0.imprint","IMPRINT",EDGE,{"disambiguationData":[TD([[subQ6,-1.0]])],"derivedFrom":subQ1}),1.0]])]});}
            var Q8;
            {var subQ1=sQuery(id+"F0.wireOp",EDGE,"E45");var subQ5=sQuery(id+"F0.wireOp",EDGE,"E57");var subQ6=makeQuery(id+"F0.imprint","INTERSECT",VERTEX,{"derivedFrom":[subQ1,subQ5]});Q8=makeQuery(id+"F0.imprint","IMPRINT",FACE,{"disambiguationData":[TD([[makeQuery(id+"F0.imprint","IMPRINT",EDGE,{"disambiguationData":[TD([[subQ6,-1.0]])],"derivedFrom":subQ1}),1.0]])]});}
            var Q9;
            {var subQ0=sQuery(id+"F0.wireOp",EDGE,"E58");var subQ1=sQuery(id+"F0.wireOp",EDGE,"E45");var subQ2=makeQuery(id+"F0.imprint","INTERSECT",VERTEX,{"derivedFrom":[subQ1,subQ0]});Q9=makeQuery(id+"F0.imprint","IMPRINT",FACE,{"disambiguationData":[TD([[makeQuery(id+"F0.imprint","IMPRINT",EDGE,{"disambiguationData":[TD([[subQ2,-1.0]])],"derivedFrom":subQ1}),1.0]])]});}
            var Q10;
            {var subQ0=sQuery(id+"F0.wireOp",EDGE,"E56");var subQ1=sQuery(id+"F0.wireOp",EDGE,"E45");var subQ2=makeQuery(id+"F0.imprint","INTERSECT",VERTEX,{"derivedFrom":[subQ1,subQ0]});Q10=makeQuery(id+"F0.imprint","IMPRINT",FACE,{"disambiguationData":[TD([[makeQuery(id+"F0.imprint","IMPRINT",EDGE,{"disambiguationData":[TD([[subQ2,-1.0]])],"derivedFrom":subQ1}),1.0]])]});}
            var Q11;
            {var subQ1=sQuery(id+"F0.wireOp",EDGE,"E45");var subQ5=sQuery(id+"F0.wireOp",EDGE,"E51");var subQ6=makeQuery(id+"F0.imprint","INTERSECT",VERTEX,{"derivedFrom":[subQ1,subQ5]});Q11=makeQuery(id+"F0.imprint","IMPRINT",FACE,{"disambiguationData":[TD([[makeQuery(id+"F0.imprint","IMPRINT",EDGE,{"disambiguationData":[TD([[subQ6,-1.0]])],"derivedFrom":subQ1}),1.0]])]});}
            var Q12;
            {var subQ1=sQuery(id+"F0.wireOp",EDGE,"E45");var subQ5=sQuery(id+"F0.wireOp",EDGE,"E49");var subQ6=makeQuery(id+"F0.imprint","INTERSECT",VERTEX,{"derivedFrom":[subQ1,subQ5]});Q12=makeQuery(id+"F0.imprint","IMPRINT",FACE,{"disambiguationData":[TD([[makeQuery(id+"F0.imprint","IMPRINT",EDGE,{"disambiguationData":[TD([[subQ6,-1.0]])],"derivedFrom":subQ1}),1.0]])]});}
            var Q13;
            {var subQ3=sQuery(id+"F0.wireOp",EDGE,"E39");var subQ5=sQuery(id+"F0.wireOp",EDGE,"E37");var subQ7=makeQuery(id+"F0.imprint","INTERSECT",VERTEX,{"derivedFrom":[subQ5,subQ3]});Q13=makeQuery(id+"F0.imprint","IMPRINT",FACE,{"disambiguationData":[TD([[makeQuery(id+"F0.imprint","IMPRINT",EDGE,{"disambiguationData":[TD([[subQ7,1.0]])],"derivedFrom":subQ5}),-1.0]])]});}
            var Q14;
            {var subQ3=sQuery(id+"F0.wireOp",EDGE,"E36");var subQ5=sQuery(id+"F0.wireOp",EDGE,"E37");var subQ7=makeQuery(id+"F0.imprint","INTERSECT",VERTEX,{"derivedFrom":[subQ3,subQ5]});Q14=makeQuery(id+"F0.imprint","IMPRINT",FACE,{"disambiguationData":[TD([[makeQuery(id+"F0.imprint","IMPRINT",EDGE,{"disambiguationData":[TD([[subQ7,1.0]])],"derivedFrom":subQ3}),1.0]])]});}
            var Q15;
            {var subQ3=sQuery(id+"F0.wireOp",EDGE,"E40");var subQ5=sQuery(id+"F0.wireOp",EDGE,"E37");var subQ7=makeQuery(id+"F0.imprint","INTERSECT",VERTEX,{"derivedFrom":[subQ5,subQ3]});Q15=makeQuery(id+"F0.imprint","IMPRINT",FACE,{"disambiguationData":[TD([[makeQuery(id+"F0.imprint","IMPRINT",EDGE,{"disambiguationData":[TD([[subQ7,1.0]])],"derivedFrom":subQ5}),-1.0]])]});}
            var Q16;
            {var subQ3=sQuery(id+"F0.wireOp",EDGE,"E41");var subQ5=sQuery(id+"F0.wireOp",EDGE,"E37");var subQ7=makeQuery(id+"F0.imprint","INTERSECT",VERTEX,{"derivedFrom":[subQ5,subQ3]});Q16=makeQuery(id+"F0.imprint","IMPRINT",FACE,{"disambiguationData":[TD([[makeQuery(id+"F0.imprint","IMPRINT",EDGE,{"disambiguationData":[TD([[subQ7,1.0]])],"derivedFrom":subQ5}),-1.0]])]});}
            var Q17;
            {var subQ3=sQuery(id+"F0.wireOp",EDGE,"E44");var subQ5=sQuery(id+"F0.wireOp",EDGE,"E37");var subQ7=makeQuery(id+"F0.imprint","INTERSECT",VERTEX,{"derivedFrom":[subQ5,subQ3]});Q17=makeQuery(id+"F0.imprint","IMPRINT",FACE,{"disambiguationData":[TD([[makeQuery(id+"F0.imprint","IMPRINT",EDGE,{"disambiguationData":[TD([[subQ7,1.0]])],"derivedFrom":subQ5}),-1.0]])]});}
            var Q18;
            {var subQ3=sQuery(id+"F0.wireOp",EDGE,"E42");var subQ5=sQuery(id+"F0.wireOp",EDGE,"E37");var subQ7=makeQuery(id+"F0.imprint","INTERSECT",VERTEX,{"derivedFrom":[subQ5,subQ3]});Q18=makeQuery(id+"F0.imprint","IMPRINT",FACE,{"disambiguationData":[TD([[makeQuery(id+"F0.imprint","IMPRINT",EDGE,{"disambiguationData":[TD([[subQ7,1.0]])],"derivedFrom":subQ5}),-1.0]])]});}
            var Q19;
            {var subQ3=sQuery(id+"F0.wireOp",EDGE,"E38");var subQ5=sQuery(id+"F0.wireOp",EDGE,"E37");var subQ7=makeQuery(id+"F0.imprint","INTERSECT",VERTEX,{"derivedFrom":[subQ5,subQ3]});Q19=makeQuery(id+"F0.imprint","IMPRINT",FACE,{"disambiguationData":[TD([[makeQuery(id+"F0.imprint","IMPRINT",EDGE,{"disambiguationData":[TD([[subQ7,1.0]])],"derivedFrom":subQ5}),-1.0]])]});}
            var Q20;
            {var subQ3=sQuery(id+"F0.wireOp",EDGE,"E43");var subQ5=sQuery(id+"F0.wireOp",EDGE,"E37");var subQ7=makeQuery(id+"F0.imprint","INTERSECT",VERTEX,{"derivedFrom":[subQ5,subQ3]});Q20=makeQuery(id+"F0.imprint","IMPRINT",FACE,{"disambiguationData":[TD([[makeQuery(id+"F0.imprint","IMPRINT",EDGE,{"disambiguationData":[TD([[subQ7,1.0]])],"derivedFrom":subQ5}),-1.0]])]});}
            var Q21;
            {var subQ3=sQuery(id+"F0.wireOp",EDGE,"E36");var subQ5=sQuery(id+"F0.wireOp",EDGE,"E47");var subQ7=makeQuery(id+"F0.imprint","INTERSECT",VERTEX,{"derivedFrom":[subQ3,subQ5]});Q21=makeQuery(id+"F0.imprint","IMPRINT",FACE,{"disambiguationData":[TD([[makeQuery(id+"F0.imprint","IMPRINT",EDGE,{"disambiguationData":[TD([[subQ7,-1.0]])],"derivedFrom":subQ3}),1.0]])]});}
            var Q22;
            {var subQ3=sQuery(id+"F0.wireOp",EDGE,"E40");var subQ5=sQuery(id+"F0.wireOp",EDGE,"E47");var subQ7=makeQuery(id+"F0.imprint","INTERSECT",VERTEX,{"derivedFrom":[subQ3,subQ5]});Q22=makeQuery(id+"F0.imprint","IMPRINT",FACE,{"disambiguationData":[TD([[makeQuery(id+"F0.imprint","IMPRINT",EDGE,{"disambiguationData":[TD([[subQ7,-1.0]])],"derivedFrom":subQ3}),1.0]])]});}
            var Q23;
            {var subQ3=sQuery(id+"F0.wireOp",EDGE,"E41");var subQ5=sQuery(id+"F0.wireOp",EDGE,"E47");var subQ7=makeQuery(id+"F0.imprint","INTERSECT",VERTEX,{"derivedFrom":[subQ3,subQ5]});Q23=makeQuery(id+"F0.imprint","IMPRINT",FACE,{"disambiguationData":[TD([[makeQuery(id+"F0.imprint","IMPRINT",EDGE,{"disambiguationData":[TD([[subQ7,-1.0]])],"derivedFrom":subQ3}),1.0]])]});}
            var Q24;
            {var subQ3=sQuery(id+"F0.wireOp",EDGE,"E44");var subQ5=sQuery(id+"F0.wireOp",EDGE,"E47");var subQ7=makeQuery(id+"F0.imprint","INTERSECT",VERTEX,{"derivedFrom":[subQ3,subQ5]});Q24=makeQuery(id+"F0.imprint","IMPRINT",FACE,{"disambiguationData":[TD([[makeQuery(id+"F0.imprint","IMPRINT",EDGE,{"disambiguationData":[TD([[subQ7,-1.0]])],"derivedFrom":subQ3}),1.0]])]});}
            var Q25;
            {var subQ3=sQuery(id+"F0.wireOp",EDGE,"E42");var subQ5=sQuery(id+"F0.wireOp",EDGE,"E47");var subQ7=makeQuery(id+"F0.imprint","INTERSECT",VERTEX,{"derivedFrom":[subQ3,subQ5]});Q25=makeQuery(id+"F0.imprint","IMPRINT",FACE,{"disambiguationData":[TD([[makeQuery(id+"F0.imprint","IMPRINT",EDGE,{"disambiguationData":[TD([[subQ7,-1.0]])],"derivedFrom":subQ3}),1.0]])]});}
            var Q26;
            {var subQ3=sQuery(id+"F0.wireOp",EDGE,"E38");var subQ5=sQuery(id+"F0.wireOp",EDGE,"E47");var subQ7=makeQuery(id+"F0.imprint","INTERSECT",VERTEX,{"derivedFrom":[subQ3,subQ5]});Q26=makeQuery(id+"F0.imprint","IMPRINT",FACE,{"disambiguationData":[TD([[makeQuery(id+"F0.imprint","IMPRINT",EDGE,{"disambiguationData":[TD([[subQ7,-1.0]])],"derivedFrom":subQ3}),1.0]])]});}
            var Q27;
            {var subQ3=sQuery(id+"F0.wireOp",EDGE,"E39");var subQ5=sQuery(id+"F0.wireOp",EDGE,"E47");var subQ7=makeQuery(id+"F0.imprint","INTERSECT",VERTEX,{"derivedFrom":[subQ3,subQ5]});Q27=makeQuery(id+"F0.imprint","IMPRINT",FACE,{"disambiguationData":[TD([[makeQuery(id+"F0.imprint","IMPRINT",EDGE,{"disambiguationData":[TD([[subQ7,-1.0]])],"derivedFrom":subQ3}),1.0]])]});}
            var Q28;
            {var subQ3=sQuery(id+"F0.wireOp",EDGE,"E43");var subQ5=sQuery(id+"F0.wireOp",EDGE,"E47");var subQ7=makeQuery(id+"F0.imprint","INTERSECT",VERTEX,{"derivedFrom":[subQ3,subQ5]});Q28=makeQuery(id+"F0.imprint","IMPRINT",FACE,{"disambiguationData":[TD([[makeQuery(id+"F0.imprint","IMPRINT",EDGE,{"disambiguationData":[TD([[subQ7,-1.0]])],"derivedFrom":subQ3}),1.0]])]});}
            var Q29;
            {var subQ3=sQuery(id+"F0.wireOp",EDGE,"E36");var subQ5=sQuery(id+"F0.wireOp",EDGE,"E49");var subQ7=makeQuery(id+"F0.imprint","INTERSECT",VERTEX,{"derivedFrom":[subQ3,subQ5]});Q29=makeQuery(id+"F0.imprint","IMPRINT",FACE,{"disambiguationData":[TD([[makeQuery(id+"F0.imprint","IMPRINT",EDGE,{"disambiguationData":[TD([[subQ7,-1.0]])],"derivedFrom":subQ3}),1.0]])]});}
            var Q30;
            {var subQ3=sQuery(id+"F0.wireOp",EDGE,"E36");var subQ5=sQuery(id+"F0.wireOp",EDGE,"E48");var subQ7=makeQuery(id+"F0.imprint","INTERSECT",VERTEX,{"derivedFrom":[subQ3,subQ5]});Q30=makeQuery(id+"F0.imprint","IMPRINT",FACE,{"disambiguationData":[TD([[makeQuery(id+"F0.imprint","IMPRINT",EDGE,{"disambiguationData":[TD([[subQ7,-1.0]])],"derivedFrom":subQ3}),1.0]])]});}
            var Q31;
            {var subQ3=sQuery(id+"F0.wireOp",EDGE,"E36");var subQ5=sQuery(id+"F0.wireOp",EDGE,"E57");var subQ7=makeQuery(id+"F0.imprint","INTERSECT",VERTEX,{"derivedFrom":[subQ3,subQ5]});Q31=makeQuery(id+"F0.imprint","IMPRINT",FACE,{"disambiguationData":[TD([[makeQuery(id+"F0.imprint","IMPRINT",EDGE,{"disambiguationData":[TD([[subQ7,-1.0]])],"derivedFrom":subQ3}),1.0]])]});}
            var Q32;
            {var subQ3=sQuery(id+"F0.wireOp",EDGE,"E36");var subQ5=sQuery(id+"F0.wireOp",EDGE,"E58");var subQ7=makeQuery(id+"F0.imprint","INTERSECT",VERTEX,{"derivedFrom":[subQ3,subQ5]});Q32=makeQuery(id+"F0.imprint","IMPRINT",FACE,{"disambiguationData":[TD([[makeQuery(id+"F0.imprint","IMPRINT",EDGE,{"disambiguationData":[TD([[subQ7,-1.0]])],"derivedFrom":subQ3}),1.0]])]});}
            var Q33;
            {var subQ3=sQuery(id+"F0.wireOp",EDGE,"E36");var subQ5=sQuery(id+"F0.wireOp",EDGE,"E53");var subQ7=makeQuery(id+"F0.imprint","INTERSECT",VERTEX,{"derivedFrom":[subQ3,subQ5]});Q33=makeQuery(id+"F0.imprint","IMPRINT",FACE,{"disambiguationData":[TD([[makeQuery(id+"F0.imprint","IMPRINT",EDGE,{"disambiguationData":[TD([[subQ7,-1.0]])],"derivedFrom":subQ3}),1.0]])]});}
            var Q34;
            {var subQ3=sQuery(id+"F0.wireOp",EDGE,"E36");var subQ5=sQuery(id+"F0.wireOp",EDGE,"E52");var subQ7=makeQuery(id+"F0.imprint","INTERSECT",VERTEX,{"derivedFrom":[subQ3,subQ5]});Q34=makeQuery(id+"F0.imprint","IMPRINT",FACE,{"disambiguationData":[TD([[makeQuery(id+"F0.imprint","IMPRINT",EDGE,{"disambiguationData":[TD([[subQ7,-1.0]])],"derivedFrom":subQ3}),1.0]])]});}
            var Q35;
            {var subQ3=sQuery(id+"F0.wireOp",EDGE,"E36");var subQ5=sQuery(id+"F0.wireOp",EDGE,"E51");var subQ7=makeQuery(id+"F0.imprint","INTERSECT",VERTEX,{"derivedFrom":[subQ3,subQ5]});Q35=makeQuery(id+"F0.imprint","IMPRINT",FACE,{"disambiguationData":[TD([[makeQuery(id+"F0.imprint","IMPRINT",EDGE,{"disambiguationData":[TD([[subQ7,-1.0]])],"derivedFrom":subQ3}),1.0]])]});}
            var Q36;
            {var subQ3=sQuery(id+"F0.wireOp",EDGE,"E36");var subQ5=sQuery(id+"F0.wireOp",EDGE,"E50");var subQ7=makeQuery(id+"F0.imprint","INTERSECT",VERTEX,{"derivedFrom":[subQ3,subQ5]});Q36=makeQuery(id+"F0.imprint","IMPRINT",FACE,{"disambiguationData":[TD([[makeQuery(id+"F0.imprint","IMPRINT",EDGE,{"disambiguationData":[TD([[subQ7,-1.0]])],"derivedFrom":subQ3}),1.0]])]});}
            var Q37;
            {var subQ3=sQuery(id+"F0.wireOp",EDGE,"E41");var subQ5=sQuery(id+"F0.wireOp",EDGE,"E57");var subQ7=makeQuery(id+"F0.imprint","INTERSECT",VERTEX,{"derivedFrom":[subQ3,subQ5]});Q37=makeQuery(id+"F0.imprint","IMPRINT",FACE,{"disambiguationData":[TD([[makeQuery(id+"F0.imprint","IMPRINT",EDGE,{"disambiguationData":[TD([[subQ7,-1.0]])],"derivedFrom":subQ3}),1.0]])]});}
            var Q38;
            {var subQ3=sQuery(id+"F0.wireOp",EDGE,"E41");var subQ5=sQuery(id+"F0.wireOp",EDGE,"E52");var subQ7=makeQuery(id+"F0.imprint","INTERSECT",VERTEX,{"derivedFrom":[subQ3,subQ5]});Q38=makeQuery(id+"F0.imprint","IMPRINT",FACE,{"disambiguationData":[TD([[makeQuery(id+"F0.imprint","IMPRINT",EDGE,{"disambiguationData":[TD([[subQ7,-1.0]])],"derivedFrom":subQ3}),1.0]])]});}
            var Q39;
            {var subQ0=sQuery(id+"F0.wireOp",EDGE,"E58");var subQ3=sQuery(id+"F0.wireOp",EDGE,"E41");var subQ4=makeQuery(id+"F0.imprint","INTERSECT",VERTEX,{"derivedFrom":[subQ3,subQ0]});Q39=makeQuery(id+"F0.imprint","IMPRINT",FACE,{"disambiguationData":[TD([[makeQuery(id+"F0.imprint","IMPRINT",EDGE,{"disambiguationData":[TD([[subQ4,-1.0]])],"derivedFrom":subQ3}),1.0]])]});}
            var Q40;
            {var subQ3=sQuery(id+"F0.wireOp",EDGE,"E41");var subQ5=sQuery(id+"F0.wireOp",EDGE,"E48");var subQ7=makeQuery(id+"F0.imprint","INTERSECT",VERTEX,{"derivedFrom":[subQ3,subQ5]});Q40=makeQuery(id+"F0.imprint","IMPRINT",FACE,{"disambiguationData":[TD([[makeQuery(id+"F0.imprint","IMPRINT",EDGE,{"disambiguationData":[TD([[subQ7,-1.0]])],"derivedFrom":subQ3}),1.0]])]});}
            var Q41;
            {var subQ3=sQuery(id+"F0.wireOp",EDGE,"E41");var subQ5=sQuery(id+"F0.wireOp",EDGE,"E51");var subQ7=makeQuery(id+"F0.imprint","INTERSECT",VERTEX,{"derivedFrom":[subQ3,subQ5]});Q41=makeQuery(id+"F0.imprint","IMPRINT",FACE,{"disambiguationData":[TD([[makeQuery(id+"F0.imprint","IMPRINT",EDGE,{"disambiguationData":[TD([[subQ7,-1.0]])],"derivedFrom":subQ3}),1.0]])]});}
            var Q42;
            {var subQ3=sQuery(id+"F0.wireOp",EDGE,"E41");var subQ5=sQuery(id+"F0.wireOp",EDGE,"E49");var subQ7=makeQuery(id+"F0.imprint","INTERSECT",VERTEX,{"derivedFrom":[subQ3,subQ5]});Q42=makeQuery(id+"F0.imprint","IMPRINT",FACE,{"disambiguationData":[TD([[makeQuery(id+"F0.imprint","IMPRINT",EDGE,{"disambiguationData":[TD([[subQ7,-1.0]])],"derivedFrom":subQ3}),1.0]])]});}
            var Q43;
            {var subQ3=sQuery(id+"F0.wireOp",EDGE,"E41");var subQ5=sQuery(id+"F0.wireOp",EDGE,"E50");var subQ7=makeQuery(id+"F0.imprint","INTERSECT",VERTEX,{"derivedFrom":[subQ3,subQ5]});Q43=makeQuery(id+"F0.imprint","IMPRINT",FACE,{"disambiguationData":[TD([[makeQuery(id+"F0.imprint","IMPRINT",EDGE,{"disambiguationData":[TD([[subQ7,-1.0]])],"derivedFrom":subQ3}),1.0]])]});}
            var Q44;
            {var subQ3=sQuery(id+"F0.wireOp",EDGE,"E41");var subQ5=sQuery(id+"F0.wireOp",EDGE,"E53");var subQ7=makeQuery(id+"F0.imprint","INTERSECT",VERTEX,{"derivedFrom":[subQ3,subQ5]});Q44=makeQuery(id+"F0.imprint","IMPRINT",FACE,{"disambiguationData":[TD([[makeQuery(id+"F0.imprint","IMPRINT",EDGE,{"disambiguationData":[TD([[subQ7,-1.0]])],"derivedFrom":subQ3}),1.0]])]});}
            extrude(context, id + "F2", {"entities" : qUnion([Q0, Q1, Q2, Q3, Q4, Q5, Q6, Q7, Q8, Q9, Q10, Q11, Q12, Q13, Q14, Q15, Q16, Q17, Q18, Q19, Q20, Q21, Q22, Q23, Q24, Q25, Q26, Q27, Q28, Q29, Q30, Q31, Q32, Q33, Q34, Q35, Q36, Q37, Q38, Q39, Q40, Q41, Q42, Q43, Q44]), "endBound" : BoundingType.SYMMETRIC, "depth" : 9.96 * mm});
        }
        {
            var Q0;
            {var subQ1=sQuery(id+"F0.wireOp",EDGE,"E45");var subQ5=sQuery(id+"F0.wireOp",EDGE,"E53");var subQ6=makeQuery(id+"F0.imprint","INTERSECT",VERTEX,{"derivedFrom":[subQ1,subQ5]});Q0=makeQuery(id+"F0.imprint","IMPRINT",FACE,{"disambiguationData":[TD([[makeQuery(id+"F0.imprint","IMPRINT",EDGE,{"disambiguationData":[TD([[subQ6,-1.0]])],"derivedFrom":subQ1}),1.0]])]});}
            var Q1;
            {var subQ1=sQuery(id+"F0.wireOp",EDGE,"E45");var subQ5=sQuery(id+"F0.wireOp",EDGE,"E48");var subQ6=makeQuery(id+"F0.imprint","INTERSECT",VERTEX,{"derivedFrom":[subQ1,subQ5]});Q1=makeQuery(id+"F0.imprint","IMPRINT",FACE,{"disambiguationData":[TD([[makeQuery(id+"F0.imprint","IMPRINT",EDGE,{"disambiguationData":[TD([[subQ6,-1.0]])],"derivedFrom":subQ1}),1.0]])]});}
            var Q2;
            {var subQ1=sQuery(id+"F0.wireOp",EDGE,"E45");var subQ5=sQuery(id+"F0.wireOp",EDGE,"E47");var subQ6=makeQuery(id+"F0.imprint","INTERSECT",VERTEX,{"derivedFrom":[subQ1,subQ5]});Q2=makeQuery(id+"F0.imprint","IMPRINT",FACE,{"disambiguationData":[TD([[makeQuery(id+"F0.imprint","IMPRINT",EDGE,{"disambiguationData":[TD([[subQ6,-1.0]])],"derivedFrom":subQ1}),1.0]])]});}
            var Q3;
            {var subQ1=sQuery(id+"F0.wireOp",EDGE,"E45");var subQ5=sQuery(id+"F0.wireOp",EDGE,"E37");var subQ7=makeQuery(id+"F0.imprint","INTERSECT",VERTEX,{"derivedFrom":[subQ5,subQ1]});Q3=makeQuery(id+"F0.imprint","IMPRINT",FACE,{"disambiguationData":[TD([[makeQuery(id+"F0.imprint","IMPRINT",EDGE,{"disambiguationData":[TD([[subQ7,1.0]])],"derivedFrom":subQ5}),-1.0]])]});}
            var Q4;
            {var subQ1=sQuery(id+"F0.wireOp",EDGE,"E45");var subQ5=sQuery(id+"F0.wireOp",EDGE,"E57");var subQ6=makeQuery(id+"F0.imprint","INTERSECT",VERTEX,{"derivedFrom":[subQ1,subQ5]});Q4=makeQuery(id+"F0.imprint","IMPRINT",FACE,{"disambiguationData":[TD([[makeQuery(id+"F0.imprint","IMPRINT",EDGE,{"disambiguationData":[TD([[subQ6,-1.0]])],"derivedFrom":subQ1}),1.0]])]});}
            var Q5;
            {var subQ0=sQuery(id+"F0.wireOp",EDGE,"E58");var subQ1=sQuery(id+"F0.wireOp",EDGE,"E45");var subQ2=makeQuery(id+"F0.imprint","INTERSECT",VERTEX,{"derivedFrom":[subQ1,subQ0]});Q5=makeQuery(id+"F0.imprint","IMPRINT",FACE,{"disambiguationData":[TD([[makeQuery(id+"F0.imprint","IMPRINT",EDGE,{"disambiguationData":[TD([[subQ2,-1.0]])],"derivedFrom":subQ1}),1.0]])]});}
            var Q6;
            {var subQ1=sQuery(id+"F0.wireOp",EDGE,"E45");var subQ5=sQuery(id+"F0.wireOp",EDGE,"E49");var subQ6=makeQuery(id+"F0.imprint","INTERSECT",VERTEX,{"derivedFrom":[subQ1,subQ5]});Q6=makeQuery(id+"F0.imprint","IMPRINT",FACE,{"disambiguationData":[TD([[makeQuery(id+"F0.imprint","IMPRINT",EDGE,{"disambiguationData":[TD([[subQ6,-1.0]])],"derivedFrom":subQ1}),1.0]])]});}
            var Q7;
            {var subQ3=sQuery(id+"F0.wireOp",EDGE,"E36");var subQ5=sQuery(id+"F0.wireOp",EDGE,"E47");var subQ7=makeQuery(id+"F0.imprint","INTERSECT",VERTEX,{"derivedFrom":[subQ3,subQ5]});Q7=makeQuery(id+"F0.imprint","IMPRINT",FACE,{"disambiguationData":[TD([[makeQuery(id+"F0.imprint","IMPRINT",EDGE,{"disambiguationData":[TD([[subQ7,-1.0]])],"derivedFrom":subQ3}),1.0]])]});}
            var Q8;
            {var subQ3=sQuery(id+"F0.wireOp",EDGE,"E40");var subQ5=sQuery(id+"F0.wireOp",EDGE,"E47");var subQ7=makeQuery(id+"F0.imprint","INTERSECT",VERTEX,{"derivedFrom":[subQ3,subQ5]});Q8=makeQuery(id+"F0.imprint","IMPRINT",FACE,{"disambiguationData":[TD([[makeQuery(id+"F0.imprint","IMPRINT",EDGE,{"disambiguationData":[TD([[subQ7,-1.0]])],"derivedFrom":subQ3}),1.0]])]});}
            var Q9;
            {var subQ3=sQuery(id+"F0.wireOp",EDGE,"E41");var subQ5=sQuery(id+"F0.wireOp",EDGE,"E47");var subQ7=makeQuery(id+"F0.imprint","INTERSECT",VERTEX,{"derivedFrom":[subQ3,subQ5]});Q9=makeQuery(id+"F0.imprint","IMPRINT",FACE,{"disambiguationData":[TD([[makeQuery(id+"F0.imprint","IMPRINT",EDGE,{"disambiguationData":[TD([[subQ7,-1.0]])],"derivedFrom":subQ3}),1.0]])]});}
            var Q10;
            {var subQ3=sQuery(id+"F0.wireOp",EDGE,"E44");var subQ5=sQuery(id+"F0.wireOp",EDGE,"E47");var subQ7=makeQuery(id+"F0.imprint","INTERSECT",VERTEX,{"derivedFrom":[subQ3,subQ5]});Q10=makeQuery(id+"F0.imprint","IMPRINT",FACE,{"disambiguationData":[TD([[makeQuery(id+"F0.imprint","IMPRINT",EDGE,{"disambiguationData":[TD([[subQ7,-1.0]])],"derivedFrom":subQ3}),1.0]])]});}
            var Q11;
            {var subQ3=sQuery(id+"F0.wireOp",EDGE,"E42");var subQ5=sQuery(id+"F0.wireOp",EDGE,"E47");var subQ7=makeQuery(id+"F0.imprint","INTERSECT",VERTEX,{"derivedFrom":[subQ3,subQ5]});Q11=makeQuery(id+"F0.imprint","IMPRINT",FACE,{"disambiguationData":[TD([[makeQuery(id+"F0.imprint","IMPRINT",EDGE,{"disambiguationData":[TD([[subQ7,-1.0]])],"derivedFrom":subQ3}),1.0]])]});}
            var Q12;
            {var subQ3=sQuery(id+"F0.wireOp",EDGE,"E38");var subQ5=sQuery(id+"F0.wireOp",EDGE,"E47");var subQ7=makeQuery(id+"F0.imprint","INTERSECT",VERTEX,{"derivedFrom":[subQ3,subQ5]});Q12=makeQuery(id+"F0.imprint","IMPRINT",FACE,{"disambiguationData":[TD([[makeQuery(id+"F0.imprint","IMPRINT",EDGE,{"disambiguationData":[TD([[subQ7,-1.0]])],"derivedFrom":subQ3}),1.0]])]});}
            var Q13;
            {var subQ3=sQuery(id+"F0.wireOp",EDGE,"E39");var subQ5=sQuery(id+"F0.wireOp",EDGE,"E47");var subQ7=makeQuery(id+"F0.imprint","INTERSECT",VERTEX,{"derivedFrom":[subQ3,subQ5]});Q13=makeQuery(id+"F0.imprint","IMPRINT",FACE,{"disambiguationData":[TD([[makeQuery(id+"F0.imprint","IMPRINT",EDGE,{"disambiguationData":[TD([[subQ7,-1.0]])],"derivedFrom":subQ3}),1.0]])]});}
            var Q14;
            {var subQ3=sQuery(id+"F0.wireOp",EDGE,"E43");var subQ5=sQuery(id+"F0.wireOp",EDGE,"E47");var subQ7=makeQuery(id+"F0.imprint","INTERSECT",VERTEX,{"derivedFrom":[subQ3,subQ5]});Q14=makeQuery(id+"F0.imprint","IMPRINT",FACE,{"disambiguationData":[TD([[makeQuery(id+"F0.imprint","IMPRINT",EDGE,{"disambiguationData":[TD([[subQ7,-1.0]])],"derivedFrom":subQ3}),1.0]])]});}
            var Q15;
            {var subQ3=sQuery(id+"F0.wireOp",EDGE,"E39");var subQ5=sQuery(id+"F0.wireOp",EDGE,"E37");var subQ7=makeQuery(id+"F0.imprint","INTERSECT",VERTEX,{"derivedFrom":[subQ5,subQ3]});Q15=makeQuery(id+"F0.imprint","IMPRINT",FACE,{"disambiguationData":[TD([[makeQuery(id+"F0.imprint","IMPRINT",EDGE,{"disambiguationData":[TD([[subQ7,1.0]])],"derivedFrom":subQ5}),-1.0]])]});}
            var Q16;
            {var subQ3=sQuery(id+"F0.wireOp",EDGE,"E36");var subQ5=sQuery(id+"F0.wireOp",EDGE,"E37");var subQ7=makeQuery(id+"F0.imprint","INTERSECT",VERTEX,{"derivedFrom":[subQ3,subQ5]});Q16=makeQuery(id+"F0.imprint","IMPRINT",FACE,{"disambiguationData":[TD([[makeQuery(id+"F0.imprint","IMPRINT",EDGE,{"disambiguationData":[TD([[subQ7,1.0]])],"derivedFrom":subQ3}),1.0]])]});}
            var Q17;
            {var subQ3=sQuery(id+"F0.wireOp",EDGE,"E40");var subQ5=sQuery(id+"F0.wireOp",EDGE,"E37");var subQ7=makeQuery(id+"F0.imprint","INTERSECT",VERTEX,{"derivedFrom":[subQ5,subQ3]});Q17=makeQuery(id+"F0.imprint","IMPRINT",FACE,{"disambiguationData":[TD([[makeQuery(id+"F0.imprint","IMPRINT",EDGE,{"disambiguationData":[TD([[subQ7,1.0]])],"derivedFrom":subQ5}),-1.0]])]});}
            var Q18;
            {var subQ3=sQuery(id+"F0.wireOp",EDGE,"E41");var subQ5=sQuery(id+"F0.wireOp",EDGE,"E37");var subQ7=makeQuery(id+"F0.imprint","INTERSECT",VERTEX,{"derivedFrom":[subQ5,subQ3]});Q18=makeQuery(id+"F0.imprint","IMPRINT",FACE,{"disambiguationData":[TD([[makeQuery(id+"F0.imprint","IMPRINT",EDGE,{"disambiguationData":[TD([[subQ7,1.0]])],"derivedFrom":subQ5}),-1.0]])]});}
            var Q19;
            {var subQ3=sQuery(id+"F0.wireOp",EDGE,"E44");var subQ5=sQuery(id+"F0.wireOp",EDGE,"E37");var subQ7=makeQuery(id+"F0.imprint","INTERSECT",VERTEX,{"derivedFrom":[subQ5,subQ3]});Q19=makeQuery(id+"F0.imprint","IMPRINT",FACE,{"disambiguationData":[TD([[makeQuery(id+"F0.imprint","IMPRINT",EDGE,{"disambiguationData":[TD([[subQ7,1.0]])],"derivedFrom":subQ5}),-1.0]])]});}
            var Q20;
            {var subQ3=sQuery(id+"F0.wireOp",EDGE,"E42");var subQ5=sQuery(id+"F0.wireOp",EDGE,"E37");var subQ7=makeQuery(id+"F0.imprint","INTERSECT",VERTEX,{"derivedFrom":[subQ5,subQ3]});Q20=makeQuery(id+"F0.imprint","IMPRINT",FACE,{"disambiguationData":[TD([[makeQuery(id+"F0.imprint","IMPRINT",EDGE,{"disambiguationData":[TD([[subQ7,1.0]])],"derivedFrom":subQ5}),-1.0]])]});}
            var Q21;
            {var subQ3=sQuery(id+"F0.wireOp",EDGE,"E38");var subQ5=sQuery(id+"F0.wireOp",EDGE,"E37");var subQ7=makeQuery(id+"F0.imprint","INTERSECT",VERTEX,{"derivedFrom":[subQ5,subQ3]});Q21=makeQuery(id+"F0.imprint","IMPRINT",FACE,{"disambiguationData":[TD([[makeQuery(id+"F0.imprint","IMPRINT",EDGE,{"disambiguationData":[TD([[subQ7,1.0]])],"derivedFrom":subQ5}),-1.0]])]});}
            var Q22;
            {var subQ3=sQuery(id+"F0.wireOp",EDGE,"E43");var subQ5=sQuery(id+"F0.wireOp",EDGE,"E37");var subQ7=makeQuery(id+"F0.imprint","INTERSECT",VERTEX,{"derivedFrom":[subQ5,subQ3]});Q22=makeQuery(id+"F0.imprint","IMPRINT",FACE,{"disambiguationData":[TD([[makeQuery(id+"F0.imprint","IMPRINT",EDGE,{"disambiguationData":[TD([[subQ7,1.0]])],"derivedFrom":subQ5}),-1.0]])]});}
            var Q23;
            {var subQ3=sQuery(id+"F0.wireOp",EDGE,"E36");var subQ5=sQuery(id+"F0.wireOp",EDGE,"E49");var subQ7=makeQuery(id+"F0.imprint","INTERSECT",VERTEX,{"derivedFrom":[subQ3,subQ5]});Q23=makeQuery(id+"F0.imprint","IMPRINT",FACE,{"disambiguationData":[TD([[makeQuery(id+"F0.imprint","IMPRINT",EDGE,{"disambiguationData":[TD([[subQ7,-1.0]])],"derivedFrom":subQ3}),1.0]])]});}
            var Q24;
            {var subQ3=sQuery(id+"F0.wireOp",EDGE,"E36");var subQ5=sQuery(id+"F0.wireOp",EDGE,"E48");var subQ7=makeQuery(id+"F0.imprint","INTERSECT",VERTEX,{"derivedFrom":[subQ3,subQ5]});Q24=makeQuery(id+"F0.imprint","IMPRINT",FACE,{"disambiguationData":[TD([[makeQuery(id+"F0.imprint","IMPRINT",EDGE,{"disambiguationData":[TD([[subQ7,-1.0]])],"derivedFrom":subQ3}),1.0]])]});}
            var Q25;
            {var subQ3=sQuery(id+"F0.wireOp",EDGE,"E36");var subQ5=sQuery(id+"F0.wireOp",EDGE,"E57");var subQ7=makeQuery(id+"F0.imprint","INTERSECT",VERTEX,{"derivedFrom":[subQ3,subQ5]});Q25=makeQuery(id+"F0.imprint","IMPRINT",FACE,{"disambiguationData":[TD([[makeQuery(id+"F0.imprint","IMPRINT",EDGE,{"disambiguationData":[TD([[subQ7,-1.0]])],"derivedFrom":subQ3}),1.0]])]});}
            var Q26;
            {var subQ3=sQuery(id+"F0.wireOp",EDGE,"E36");var subQ5=sQuery(id+"F0.wireOp",EDGE,"E58");var subQ7=makeQuery(id+"F0.imprint","INTERSECT",VERTEX,{"derivedFrom":[subQ3,subQ5]});Q26=makeQuery(id+"F0.imprint","IMPRINT",FACE,{"disambiguationData":[TD([[makeQuery(id+"F0.imprint","IMPRINT",EDGE,{"disambiguationData":[TD([[subQ7,-1.0]])],"derivedFrom":subQ3}),1.0]])]});}
            var Q27;
            {var subQ3=sQuery(id+"F0.wireOp",EDGE,"E36");var subQ5=sQuery(id+"F0.wireOp",EDGE,"E53");var subQ7=makeQuery(id+"F0.imprint","INTERSECT",VERTEX,{"derivedFrom":[subQ3,subQ5]});Q27=makeQuery(id+"F0.imprint","IMPRINT",FACE,{"disambiguationData":[TD([[makeQuery(id+"F0.imprint","IMPRINT",EDGE,{"disambiguationData":[TD([[subQ7,-1.0]])],"derivedFrom":subQ3}),1.0]])]});}
            var Q28;
            {var subQ3=sQuery(id+"F0.wireOp",EDGE,"E36");var subQ5=sQuery(id+"F0.wireOp",EDGE,"E52");var subQ7=makeQuery(id+"F0.imprint","INTERSECT",VERTEX,{"derivedFrom":[subQ3,subQ5]});Q28=makeQuery(id+"F0.imprint","IMPRINT",FACE,{"disambiguationData":[TD([[makeQuery(id+"F0.imprint","IMPRINT",EDGE,{"disambiguationData":[TD([[subQ7,-1.0]])],"derivedFrom":subQ3}),1.0]])]});}
            var Q29;
            {var subQ3=sQuery(id+"F0.wireOp",EDGE,"E36");var subQ5=sQuery(id+"F0.wireOp",EDGE,"E51");var subQ7=makeQuery(id+"F0.imprint","INTERSECT",VERTEX,{"derivedFrom":[subQ3,subQ5]});Q29=makeQuery(id+"F0.imprint","IMPRINT",FACE,{"disambiguationData":[TD([[makeQuery(id+"F0.imprint","IMPRINT",EDGE,{"disambiguationData":[TD([[subQ7,-1.0]])],"derivedFrom":subQ3}),1.0]])]});}
            var Q30;
            {var subQ3=sQuery(id+"F0.wireOp",EDGE,"E36");var subQ5=sQuery(id+"F0.wireOp",EDGE,"E50");var subQ7=makeQuery(id+"F0.imprint","INTERSECT",VERTEX,{"derivedFrom":[subQ3,subQ5]});Q30=makeQuery(id+"F0.imprint","IMPRINT",FACE,{"disambiguationData":[TD([[makeQuery(id+"F0.imprint","IMPRINT",EDGE,{"disambiguationData":[TD([[subQ7,-1.0]])],"derivedFrom":subQ3}),1.0]])]});}
            var Q31;
            {var subQ3=sQuery(id+"F0.wireOp",EDGE,"E41");var subQ5=sQuery(id+"F0.wireOp",EDGE,"E56");var subQ7=makeQuery(id+"F0.imprint","INTERSECT",VERTEX,{"derivedFrom":[subQ3,subQ5]});Q31=makeQuery(id+"F0.imprint","IMPRINT",FACE,{"disambiguationData":[TD([[makeQuery(id+"F0.imprint","IMPRINT",EDGE,{"disambiguationData":[TD([[subQ7,-1.0]])],"derivedFrom":subQ3}),1.0]])]});}
            var Q32;
            {var subQ3=sQuery(id+"F0.wireOp",EDGE,"E41");var subQ5=sQuery(id+"F0.wireOp",EDGE,"E57");var subQ7=makeQuery(id+"F0.imprint","INTERSECT",VERTEX,{"derivedFrom":[subQ3,subQ5]});Q32=makeQuery(id+"F0.imprint","IMPRINT",FACE,{"disambiguationData":[TD([[makeQuery(id+"F0.imprint","IMPRINT",EDGE,{"disambiguationData":[TD([[subQ7,-1.0]])],"derivedFrom":subQ3}),1.0]])]});}
            var Q33;
            {var subQ3=sQuery(id+"F0.wireOp",EDGE,"E41");var subQ5=sQuery(id+"F0.wireOp",EDGE,"E52");var subQ7=makeQuery(id+"F0.imprint","INTERSECT",VERTEX,{"derivedFrom":[subQ3,subQ5]});Q33=makeQuery(id+"F0.imprint","IMPRINT",FACE,{"disambiguationData":[TD([[makeQuery(id+"F0.imprint","IMPRINT",EDGE,{"disambiguationData":[TD([[subQ7,-1.0]])],"derivedFrom":subQ3}),1.0]])]});}
            var Q34;
            {var subQ0=sQuery(id+"F0.wireOp",EDGE,"E58");var subQ3=sQuery(id+"F0.wireOp",EDGE,"E41");var subQ4=makeQuery(id+"F0.imprint","INTERSECT",VERTEX,{"derivedFrom":[subQ3,subQ0]});Q34=makeQuery(id+"F0.imprint","IMPRINT",FACE,{"disambiguationData":[TD([[makeQuery(id+"F0.imprint","IMPRINT",EDGE,{"disambiguationData":[TD([[subQ4,-1.0]])],"derivedFrom":subQ3}),1.0]])]});}
            var Q35;
            {var subQ3=sQuery(id+"F0.wireOp",EDGE,"E41");var subQ5=sQuery(id+"F0.wireOp",EDGE,"E48");var subQ7=makeQuery(id+"F0.imprint","INTERSECT",VERTEX,{"derivedFrom":[subQ3,subQ5]});Q35=makeQuery(id+"F0.imprint","IMPRINT",FACE,{"disambiguationData":[TD([[makeQuery(id+"F0.imprint","IMPRINT",EDGE,{"disambiguationData":[TD([[subQ7,-1.0]])],"derivedFrom":subQ3}),1.0]])]});}
            var Q36;
            {var subQ3=sQuery(id+"F0.wireOp",EDGE,"E41");var subQ5=sQuery(id+"F0.wireOp",EDGE,"E51");var subQ7=makeQuery(id+"F0.imprint","INTERSECT",VERTEX,{"derivedFrom":[subQ3,subQ5]});Q36=makeQuery(id+"F0.imprint","IMPRINT",FACE,{"disambiguationData":[TD([[makeQuery(id+"F0.imprint","IMPRINT",EDGE,{"disambiguationData":[TD([[subQ7,-1.0]])],"derivedFrom":subQ3}),1.0]])]});}
            var Q37;
            {var subQ3=sQuery(id+"F0.wireOp",EDGE,"E41");var subQ5=sQuery(id+"F0.wireOp",EDGE,"E54");var subQ7=makeQuery(id+"F0.imprint","INTERSECT",VERTEX,{"derivedFrom":[subQ3,subQ5]});Q37=makeQuery(id+"F0.imprint","IMPRINT",FACE,{"disambiguationData":[TD([[makeQuery(id+"F0.imprint","IMPRINT",EDGE,{"disambiguationData":[TD([[subQ7,-1.0]])],"derivedFrom":subQ3}),1.0]])]});}
            var Q38;
            {var subQ3=sQuery(id+"F0.wireOp",EDGE,"E41");var subQ5=sQuery(id+"F0.wireOp",EDGE,"E49");var subQ7=makeQuery(id+"F0.imprint","INTERSECT",VERTEX,{"derivedFrom":[subQ3,subQ5]});Q38=makeQuery(id+"F0.imprint","IMPRINT",FACE,{"disambiguationData":[TD([[makeQuery(id+"F0.imprint","IMPRINT",EDGE,{"disambiguationData":[TD([[subQ7,-1.0]])],"derivedFrom":subQ3}),1.0]])]});}
            var Q39;
            {var subQ3=sQuery(id+"F0.wireOp",EDGE,"E41");var subQ5=sQuery(id+"F0.wireOp",EDGE,"E50");var subQ7=makeQuery(id+"F0.imprint","INTERSECT",VERTEX,{"derivedFrom":[subQ3,subQ5]});Q39=makeQuery(id+"F0.imprint","IMPRINT",FACE,{"disambiguationData":[TD([[makeQuery(id+"F0.imprint","IMPRINT",EDGE,{"disambiguationData":[TD([[subQ7,-1.0]])],"derivedFrom":subQ3}),1.0]])]});}
            var Q40;
            {var subQ3=sQuery(id+"F0.wireOp",EDGE,"E41");var subQ5=sQuery(id+"F0.wireOp",EDGE,"E55");var subQ7=makeQuery(id+"F0.imprint","INTERSECT",VERTEX,{"derivedFrom":[subQ3,subQ5]});Q40=makeQuery(id+"F0.imprint","IMPRINT",FACE,{"disambiguationData":[TD([[makeQuery(id+"F0.imprint","IMPRINT",EDGE,{"disambiguationData":[TD([[subQ7,-1.0]])],"derivedFrom":subQ3}),1.0]])]});}
            var Q41;
            {var subQ3=sQuery(id+"F0.wireOp",EDGE,"E41");var subQ5=sQuery(id+"F0.wireOp",EDGE,"E53");var subQ7=makeQuery(id+"F0.imprint","INTERSECT",VERTEX,{"derivedFrom":[subQ3,subQ5]});Q41=makeQuery(id+"F0.imprint","IMPRINT",FACE,{"disambiguationData":[TD([[makeQuery(id+"F0.imprint","IMPRINT",EDGE,{"disambiguationData":[TD([[subQ7,-1.0]])],"derivedFrom":subQ3}),1.0]])]});}
            var Q42;
            {var subQ3=sQuery(id+"F0.wireOp",EDGE,"E43");var subQ5=sQuery(id+"F0.wireOp",EDGE,"E53");var subQ7=makeQuery(id+"F0.imprint","INTERSECT",VERTEX,{"derivedFrom":[subQ3,subQ5]});Q42=makeQuery(id+"F0.imprint","IMPRINT",FACE,{"disambiguationData":[TD([[makeQuery(id+"F0.imprint","IMPRINT",EDGE,{"disambiguationData":[TD([[subQ7,-1.0]])],"derivedFrom":subQ3}),1.0]])]});}
            var Q43;
            {var subQ3=sQuery(id+"F0.wireOp",EDGE,"E42");var subQ5=sQuery(id+"F0.wireOp",EDGE,"E53");var subQ7=makeQuery(id+"F0.imprint","INTERSECT",VERTEX,{"derivedFrom":[subQ3,subQ5]});Q43=makeQuery(id+"F0.imprint","IMPRINT",FACE,{"disambiguationData":[TD([[makeQuery(id+"F0.imprint","IMPRINT",EDGE,{"disambiguationData":[TD([[subQ7,-1.0]])],"derivedFrom":subQ3}),1.0]])]});}
            var Q44;
            {var subQ3=sQuery(id+"F0.wireOp",EDGE,"E44");var subQ5=sQuery(id+"F0.wireOp",EDGE,"E53");var subQ7=makeQuery(id+"F0.imprint","INTERSECT",VERTEX,{"derivedFrom":[subQ3,subQ5]});Q44=makeQuery(id+"F0.imprint","IMPRINT",FACE,{"disambiguationData":[TD([[makeQuery(id+"F0.imprint","IMPRINT",EDGE,{"disambiguationData":[TD([[subQ7,-1.0]])],"derivedFrom":subQ3}),1.0]])]});}
            extrude(context, id + "F3", {"entities" : qUnion([Q0, Q1, Q2, Q3, Q4, Q5, Q6, Q7, Q8, Q9, Q10, Q11, Q12, Q13, Q14, Q15, Q16, Q17, Q18, Q19, Q20, Q21, Q22, Q23, Q24, Q25, Q26, Q27, Q28, Q29, Q30, Q31, Q32, Q33, Q34, Q35, Q36, Q37, Q38, Q39, Q40, Q41, Q42, Q43, Q44]), "endBound" : BoundingType.SYMMETRIC, "depth" : 9.96 * mm});
        }
        {
            var Q0;
            {var subQ1=sQuery(id+"F0.wireOp",EDGE,"E45");var subQ5=sQuery(id+"F0.wireOp",EDGE,"E53");var subQ6=makeQuery(id+"F0.imprint","INTERSECT",VERTEX,{"derivedFrom":[subQ1,subQ5]});Q0=makeQuery(id+"F0.imprint","IMPRINT",FACE,{"disambiguationData":[TD([[makeQuery(id+"F0.imprint","IMPRINT",EDGE,{"disambiguationData":[TD([[subQ6,-1.0]])],"derivedFrom":subQ1}),1.0]])]});}
            var Q1;
            {var subQ1=sQuery(id+"F0.wireOp",EDGE,"E45");var subQ5=sQuery(id+"F0.wireOp",EDGE,"E48");var subQ6=makeQuery(id+"F0.imprint","INTERSECT",VERTEX,{"derivedFrom":[subQ1,subQ5]});Q1=makeQuery(id+"F0.imprint","IMPRINT",FACE,{"disambiguationData":[TD([[makeQuery(id+"F0.imprint","IMPRINT",EDGE,{"disambiguationData":[TD([[subQ6,-1.0]])],"derivedFrom":subQ1}),1.0]])]});}
            var Q2;
            {var subQ1=sQuery(id+"F0.wireOp",EDGE,"E45");var subQ5=sQuery(id+"F0.wireOp",EDGE,"E52");var subQ6=makeQuery(id+"F0.imprint","INTERSECT",VERTEX,{"derivedFrom":[subQ1,subQ5]});Q2=makeQuery(id+"F0.imprint","IMPRINT",FACE,{"disambiguationData":[TD([[makeQuery(id+"F0.imprint","IMPRINT",EDGE,{"disambiguationData":[TD([[subQ6,-1.0]])],"derivedFrom":subQ1}),1.0]])]});}
            var Q3;
            {var subQ1=sQuery(id+"F0.wireOp",EDGE,"E45");var subQ5=sQuery(id+"F0.wireOp",EDGE,"E47");var subQ6=makeQuery(id+"F0.imprint","INTERSECT",VERTEX,{"derivedFrom":[subQ1,subQ5]});Q3=makeQuery(id+"F0.imprint","IMPRINT",FACE,{"disambiguationData":[TD([[makeQuery(id+"F0.imprint","IMPRINT",EDGE,{"disambiguationData":[TD([[subQ6,-1.0]])],"derivedFrom":subQ1}),1.0]])]});}
            var Q4;
            {var subQ1=sQuery(id+"F0.wireOp",EDGE,"E45");var subQ5=sQuery(id+"F0.wireOp",EDGE,"E54");var subQ6=makeQuery(id+"F0.imprint","INTERSECT",VERTEX,{"derivedFrom":[subQ1,subQ5]});Q4=makeQuery(id+"F0.imprint","IMPRINT",FACE,{"disambiguationData":[TD([[makeQuery(id+"F0.imprint","IMPRINT",EDGE,{"disambiguationData":[TD([[subQ6,-1.0]])],"derivedFrom":subQ1}),1.0]])]});}
            var Q5;
            {var subQ1=sQuery(id+"F0.wireOp",EDGE,"E45");var subQ5=sQuery(id+"F0.wireOp",EDGE,"E37");var subQ7=makeQuery(id+"F0.imprint","INTERSECT",VERTEX,{"derivedFrom":[subQ5,subQ1]});Q5=makeQuery(id+"F0.imprint","IMPRINT",FACE,{"disambiguationData":[TD([[makeQuery(id+"F0.imprint","IMPRINT",EDGE,{"disambiguationData":[TD([[subQ7,1.0]])],"derivedFrom":subQ5}),-1.0]])]});}
            var Q6;
            {var subQ1=sQuery(id+"F0.wireOp",EDGE,"E45");var subQ5=sQuery(id+"F0.wireOp",EDGE,"E55");var subQ6=makeQuery(id+"F0.imprint","INTERSECT",VERTEX,{"derivedFrom":[subQ1,subQ5]});Q6=makeQuery(id+"F0.imprint","IMPRINT",FACE,{"disambiguationData":[TD([[makeQuery(id+"F0.imprint","IMPRINT",EDGE,{"disambiguationData":[TD([[subQ6,-1.0]])],"derivedFrom":subQ1}),1.0]])]});}
            var Q7;
            {var subQ1=sQuery(id+"F0.wireOp",EDGE,"E45");var subQ5=sQuery(id+"F0.wireOp",EDGE,"E50");var subQ6=makeQuery(id+"F0.imprint","INTERSECT",VERTEX,{"derivedFrom":[subQ1,subQ5]});Q7=makeQuery(id+"F0.imprint","IMPRINT",FACE,{"disambiguationData":[TD([[makeQuery(id+"F0.imprint","IMPRINT",EDGE,{"disambiguationData":[TD([[subQ6,-1.0]])],"derivedFrom":subQ1}),1.0]])]});}
            var Q8;
            {var subQ1=sQuery(id+"F0.wireOp",EDGE,"E45");var subQ5=sQuery(id+"F0.wireOp",EDGE,"E57");var subQ6=makeQuery(id+"F0.imprint","INTERSECT",VERTEX,{"derivedFrom":[subQ1,subQ5]});Q8=makeQuery(id+"F0.imprint","IMPRINT",FACE,{"disambiguationData":[TD([[makeQuery(id+"F0.imprint","IMPRINT",EDGE,{"disambiguationData":[TD([[subQ6,-1.0]])],"derivedFrom":subQ1}),1.0]])]});}
            var Q9;
            {var subQ0=sQuery(id+"F0.wireOp",EDGE,"E58");var subQ1=sQuery(id+"F0.wireOp",EDGE,"E45");var subQ2=makeQuery(id+"F0.imprint","INTERSECT",VERTEX,{"derivedFrom":[subQ1,subQ0]});Q9=makeQuery(id+"F0.imprint","IMPRINT",FACE,{"disambiguationData":[TD([[makeQuery(id+"F0.imprint","IMPRINT",EDGE,{"disambiguationData":[TD([[subQ2,-1.0]])],"derivedFrom":subQ1}),1.0]])]});}
            var Q10;
            {var subQ0=sQuery(id+"F0.wireOp",EDGE,"E56");var subQ1=sQuery(id+"F0.wireOp",EDGE,"E45");var subQ2=makeQuery(id+"F0.imprint","INTERSECT",VERTEX,{"derivedFrom":[subQ1,subQ0]});Q10=makeQuery(id+"F0.imprint","IMPRINT",FACE,{"disambiguationData":[TD([[makeQuery(id+"F0.imprint","IMPRINT",EDGE,{"disambiguationData":[TD([[subQ2,-1.0]])],"derivedFrom":subQ1}),1.0]])]});}
            var Q11;
            {var subQ1=sQuery(id+"F0.wireOp",EDGE,"E45");var subQ5=sQuery(id+"F0.wireOp",EDGE,"E51");var subQ6=makeQuery(id+"F0.imprint","INTERSECT",VERTEX,{"derivedFrom":[subQ1,subQ5]});Q11=makeQuery(id+"F0.imprint","IMPRINT",FACE,{"disambiguationData":[TD([[makeQuery(id+"F0.imprint","IMPRINT",EDGE,{"disambiguationData":[TD([[subQ6,-1.0]])],"derivedFrom":subQ1}),1.0]])]});}
            var Q12;
            {var subQ1=sQuery(id+"F0.wireOp",EDGE,"E45");var subQ5=sQuery(id+"F0.wireOp",EDGE,"E49");var subQ6=makeQuery(id+"F0.imprint","INTERSECT",VERTEX,{"derivedFrom":[subQ1,subQ5]});Q12=makeQuery(id+"F0.imprint","IMPRINT",FACE,{"disambiguationData":[TD([[makeQuery(id+"F0.imprint","IMPRINT",EDGE,{"disambiguationData":[TD([[subQ6,-1.0]])],"derivedFrom":subQ1}),1.0]])]});}
            var Q13;
            {var subQ3=sQuery(id+"F0.wireOp",EDGE,"E39");var subQ5=sQuery(id+"F0.wireOp",EDGE,"E37");var subQ7=makeQuery(id+"F0.imprint","INTERSECT",VERTEX,{"derivedFrom":[subQ5,subQ3]});Q13=makeQuery(id+"F0.imprint","IMPRINT",FACE,{"disambiguationData":[TD([[makeQuery(id+"F0.imprint","IMPRINT",EDGE,{"disambiguationData":[TD([[subQ7,1.0]])],"derivedFrom":subQ5}),-1.0]])]});}
            var Q14;
            {var subQ3=sQuery(id+"F0.wireOp",EDGE,"E36");var subQ5=sQuery(id+"F0.wireOp",EDGE,"E37");var subQ7=makeQuery(id+"F0.imprint","INTERSECT",VERTEX,{"derivedFrom":[subQ3,subQ5]});Q14=makeQuery(id+"F0.imprint","IMPRINT",FACE,{"disambiguationData":[TD([[makeQuery(id+"F0.imprint","IMPRINT",EDGE,{"disambiguationData":[TD([[subQ7,1.0]])],"derivedFrom":subQ3}),1.0]])]});}
            var Q15;
            {var subQ3=sQuery(id+"F0.wireOp",EDGE,"E40");var subQ5=sQuery(id+"F0.wireOp",EDGE,"E37");var subQ7=makeQuery(id+"F0.imprint","INTERSECT",VERTEX,{"derivedFrom":[subQ5,subQ3]});Q15=makeQuery(id+"F0.imprint","IMPRINT",FACE,{"disambiguationData":[TD([[makeQuery(id+"F0.imprint","IMPRINT",EDGE,{"disambiguationData":[TD([[subQ7,1.0]])],"derivedFrom":subQ5}),-1.0]])]});}
            var Q16;
            {var subQ3=sQuery(id+"F0.wireOp",EDGE,"E41");var subQ5=sQuery(id+"F0.wireOp",EDGE,"E37");var subQ7=makeQuery(id+"F0.imprint","INTERSECT",VERTEX,{"derivedFrom":[subQ5,subQ3]});Q16=makeQuery(id+"F0.imprint","IMPRINT",FACE,{"disambiguationData":[TD([[makeQuery(id+"F0.imprint","IMPRINT",EDGE,{"disambiguationData":[TD([[subQ7,1.0]])],"derivedFrom":subQ5}),-1.0]])]});}
            var Q17;
            {var subQ3=sQuery(id+"F0.wireOp",EDGE,"E44");var subQ5=sQuery(id+"F0.wireOp",EDGE,"E37");var subQ7=makeQuery(id+"F0.imprint","INTERSECT",VERTEX,{"derivedFrom":[subQ5,subQ3]});Q17=makeQuery(id+"F0.imprint","IMPRINT",FACE,{"disambiguationData":[TD([[makeQuery(id+"F0.imprint","IMPRINT",EDGE,{"disambiguationData":[TD([[subQ7,1.0]])],"derivedFrom":subQ5}),-1.0]])]});}
            var Q18;
            {var subQ3=sQuery(id+"F0.wireOp",EDGE,"E42");var subQ5=sQuery(id+"F0.wireOp",EDGE,"E37");var subQ7=makeQuery(id+"F0.imprint","INTERSECT",VERTEX,{"derivedFrom":[subQ5,subQ3]});Q18=makeQuery(id+"F0.imprint","IMPRINT",FACE,{"disambiguationData":[TD([[makeQuery(id+"F0.imprint","IMPRINT",EDGE,{"disambiguationData":[TD([[subQ7,1.0]])],"derivedFrom":subQ5}),-1.0]])]});}
            var Q19;
            {var subQ3=sQuery(id+"F0.wireOp",EDGE,"E38");var subQ5=sQuery(id+"F0.wireOp",EDGE,"E37");var subQ7=makeQuery(id+"F0.imprint","INTERSECT",VERTEX,{"derivedFrom":[subQ5,subQ3]});Q19=makeQuery(id+"F0.imprint","IMPRINT",FACE,{"disambiguationData":[TD([[makeQuery(id+"F0.imprint","IMPRINT",EDGE,{"disambiguationData":[TD([[subQ7,1.0]])],"derivedFrom":subQ5}),-1.0]])]});}
            var Q20;
            {var subQ3=sQuery(id+"F0.wireOp",EDGE,"E43");var subQ5=sQuery(id+"F0.wireOp",EDGE,"E37");var subQ7=makeQuery(id+"F0.imprint","INTERSECT",VERTEX,{"derivedFrom":[subQ5,subQ3]});Q20=makeQuery(id+"F0.imprint","IMPRINT",FACE,{"disambiguationData":[TD([[makeQuery(id+"F0.imprint","IMPRINT",EDGE,{"disambiguationData":[TD([[subQ7,1.0]])],"derivedFrom":subQ5}),-1.0]])]});}
            var Q21;
            {var subQ3=sQuery(id+"F0.wireOp",EDGE,"E36");var subQ5=sQuery(id+"F0.wireOp",EDGE,"E47");var subQ7=makeQuery(id+"F0.imprint","INTERSECT",VERTEX,{"derivedFrom":[subQ3,subQ5]});Q21=makeQuery(id+"F0.imprint","IMPRINT",FACE,{"disambiguationData":[TD([[makeQuery(id+"F0.imprint","IMPRINT",EDGE,{"disambiguationData":[TD([[subQ7,-1.0]])],"derivedFrom":subQ3}),1.0]])]});}
            var Q22;
            {var subQ3=sQuery(id+"F0.wireOp",EDGE,"E40");var subQ5=sQuery(id+"F0.wireOp",EDGE,"E47");var subQ7=makeQuery(id+"F0.imprint","INTERSECT",VERTEX,{"derivedFrom":[subQ3,subQ5]});Q22=makeQuery(id+"F0.imprint","IMPRINT",FACE,{"disambiguationData":[TD([[makeQuery(id+"F0.imprint","IMPRINT",EDGE,{"disambiguationData":[TD([[subQ7,-1.0]])],"derivedFrom":subQ3}),1.0]])]});}
            var Q23;
            {var subQ3=sQuery(id+"F0.wireOp",EDGE,"E41");var subQ5=sQuery(id+"F0.wireOp",EDGE,"E47");var subQ7=makeQuery(id+"F0.imprint","INTERSECT",VERTEX,{"derivedFrom":[subQ3,subQ5]});Q23=makeQuery(id+"F0.imprint","IMPRINT",FACE,{"disambiguationData":[TD([[makeQuery(id+"F0.imprint","IMPRINT",EDGE,{"disambiguationData":[TD([[subQ7,-1.0]])],"derivedFrom":subQ3}),1.0]])]});}
            var Q24;
            {var subQ3=sQuery(id+"F0.wireOp",EDGE,"E44");var subQ5=sQuery(id+"F0.wireOp",EDGE,"E47");var subQ7=makeQuery(id+"F0.imprint","INTERSECT",VERTEX,{"derivedFrom":[subQ3,subQ5]});Q24=makeQuery(id+"F0.imprint","IMPRINT",FACE,{"disambiguationData":[TD([[makeQuery(id+"F0.imprint","IMPRINT",EDGE,{"disambiguationData":[TD([[subQ7,-1.0]])],"derivedFrom":subQ3}),1.0]])]});}
            var Q25;
            {var subQ3=sQuery(id+"F0.wireOp",EDGE,"E42");var subQ5=sQuery(id+"F0.wireOp",EDGE,"E47");var subQ7=makeQuery(id+"F0.imprint","INTERSECT",VERTEX,{"derivedFrom":[subQ3,subQ5]});Q25=makeQuery(id+"F0.imprint","IMPRINT",FACE,{"disambiguationData":[TD([[makeQuery(id+"F0.imprint","IMPRINT",EDGE,{"disambiguationData":[TD([[subQ7,-1.0]])],"derivedFrom":subQ3}),1.0]])]});}
            var Q26;
            {var subQ3=sQuery(id+"F0.wireOp",EDGE,"E38");var subQ5=sQuery(id+"F0.wireOp",EDGE,"E47");var subQ7=makeQuery(id+"F0.imprint","INTERSECT",VERTEX,{"derivedFrom":[subQ3,subQ5]});Q26=makeQuery(id+"F0.imprint","IMPRINT",FACE,{"disambiguationData":[TD([[makeQuery(id+"F0.imprint","IMPRINT",EDGE,{"disambiguationData":[TD([[subQ7,-1.0]])],"derivedFrom":subQ3}),1.0]])]});}
            var Q27;
            {var subQ3=sQuery(id+"F0.wireOp",EDGE,"E39");var subQ5=sQuery(id+"F0.wireOp",EDGE,"E47");var subQ7=makeQuery(id+"F0.imprint","INTERSECT",VERTEX,{"derivedFrom":[subQ3,subQ5]});Q27=makeQuery(id+"F0.imprint","IMPRINT",FACE,{"disambiguationData":[TD([[makeQuery(id+"F0.imprint","IMPRINT",EDGE,{"disambiguationData":[TD([[subQ7,-1.0]])],"derivedFrom":subQ3}),1.0]])]});}
            var Q28;
            {var subQ3=sQuery(id+"F0.wireOp",EDGE,"E43");var subQ5=sQuery(id+"F0.wireOp",EDGE,"E47");var subQ7=makeQuery(id+"F0.imprint","INTERSECT",VERTEX,{"derivedFrom":[subQ3,subQ5]});Q28=makeQuery(id+"F0.imprint","IMPRINT",FACE,{"disambiguationData":[TD([[makeQuery(id+"F0.imprint","IMPRINT",EDGE,{"disambiguationData":[TD([[subQ7,-1.0]])],"derivedFrom":subQ3}),1.0]])]});}
            var Q29;
            {var subQ3=sQuery(id+"F0.wireOp",EDGE,"E36");var subQ5=sQuery(id+"F0.wireOp",EDGE,"E49");var subQ7=makeQuery(id+"F0.imprint","INTERSECT",VERTEX,{"derivedFrom":[subQ3,subQ5]});Q29=makeQuery(id+"F0.imprint","IMPRINT",FACE,{"disambiguationData":[TD([[makeQuery(id+"F0.imprint","IMPRINT",EDGE,{"disambiguationData":[TD([[subQ7,-1.0]])],"derivedFrom":subQ3}),1.0]])]});}
            var Q30;
            {var subQ3=sQuery(id+"F0.wireOp",EDGE,"E36");var subQ5=sQuery(id+"F0.wireOp",EDGE,"E48");var subQ7=makeQuery(id+"F0.imprint","INTERSECT",VERTEX,{"derivedFrom":[subQ3,subQ5]});Q30=makeQuery(id+"F0.imprint","IMPRINT",FACE,{"disambiguationData":[TD([[makeQuery(id+"F0.imprint","IMPRINT",EDGE,{"disambiguationData":[TD([[subQ7,-1.0]])],"derivedFrom":subQ3}),1.0]])]});}
            var Q31;
            {var subQ3=sQuery(id+"F0.wireOp",EDGE,"E36");var subQ5=sQuery(id+"F0.wireOp",EDGE,"E57");var subQ7=makeQuery(id+"F0.imprint","INTERSECT",VERTEX,{"derivedFrom":[subQ3,subQ5]});Q31=makeQuery(id+"F0.imprint","IMPRINT",FACE,{"disambiguationData":[TD([[makeQuery(id+"F0.imprint","IMPRINT",EDGE,{"disambiguationData":[TD([[subQ7,-1.0]])],"derivedFrom":subQ3}),1.0]])]});}
            var Q32;
            {var subQ3=sQuery(id+"F0.wireOp",EDGE,"E36");var subQ5=sQuery(id+"F0.wireOp",EDGE,"E58");var subQ7=makeQuery(id+"F0.imprint","INTERSECT",VERTEX,{"derivedFrom":[subQ3,subQ5]});Q32=makeQuery(id+"F0.imprint","IMPRINT",FACE,{"disambiguationData":[TD([[makeQuery(id+"F0.imprint","IMPRINT",EDGE,{"disambiguationData":[TD([[subQ7,-1.0]])],"derivedFrom":subQ3}),1.0]])]});}
            var Q33;
            {var subQ3=sQuery(id+"F0.wireOp",EDGE,"E36");var subQ5=sQuery(id+"F0.wireOp",EDGE,"E53");var subQ7=makeQuery(id+"F0.imprint","INTERSECT",VERTEX,{"derivedFrom":[subQ3,subQ5]});Q33=makeQuery(id+"F0.imprint","IMPRINT",FACE,{"disambiguationData":[TD([[makeQuery(id+"F0.imprint","IMPRINT",EDGE,{"disambiguationData":[TD([[subQ7,-1.0]])],"derivedFrom":subQ3}),1.0]])]});}
            var Q34;
            {var subQ3=sQuery(id+"F0.wireOp",EDGE,"E36");var subQ5=sQuery(id+"F0.wireOp",EDGE,"E52");var subQ7=makeQuery(id+"F0.imprint","INTERSECT",VERTEX,{"derivedFrom":[subQ3,subQ5]});Q34=makeQuery(id+"F0.imprint","IMPRINT",FACE,{"disambiguationData":[TD([[makeQuery(id+"F0.imprint","IMPRINT",EDGE,{"disambiguationData":[TD([[subQ7,-1.0]])],"derivedFrom":subQ3}),1.0]])]});}
            var Q35;
            {var subQ3=sQuery(id+"F0.wireOp",EDGE,"E36");var subQ5=sQuery(id+"F0.wireOp",EDGE,"E51");var subQ7=makeQuery(id+"F0.imprint","INTERSECT",VERTEX,{"derivedFrom":[subQ3,subQ5]});Q35=makeQuery(id+"F0.imprint","IMPRINT",FACE,{"disambiguationData":[TD([[makeQuery(id+"F0.imprint","IMPRINT",EDGE,{"disambiguationData":[TD([[subQ7,-1.0]])],"derivedFrom":subQ3}),1.0]])]});}
            var Q36;
            {var subQ3=sQuery(id+"F0.wireOp",EDGE,"E36");var subQ5=sQuery(id+"F0.wireOp",EDGE,"E50");var subQ7=makeQuery(id+"F0.imprint","INTERSECT",VERTEX,{"derivedFrom":[subQ3,subQ5]});Q36=makeQuery(id+"F0.imprint","IMPRINT",FACE,{"disambiguationData":[TD([[makeQuery(id+"F0.imprint","IMPRINT",EDGE,{"disambiguationData":[TD([[subQ7,-1.0]])],"derivedFrom":subQ3}),1.0]])]});}
            var Q37;
            {var subQ3=sQuery(id+"F0.wireOp",EDGE,"E41");var subQ5=sQuery(id+"F0.wireOp",EDGE,"E57");var subQ7=makeQuery(id+"F0.imprint","INTERSECT",VERTEX,{"derivedFrom":[subQ3,subQ5]});Q37=makeQuery(id+"F0.imprint","IMPRINT",FACE,{"disambiguationData":[TD([[makeQuery(id+"F0.imprint","IMPRINT",EDGE,{"disambiguationData":[TD([[subQ7,-1.0]])],"derivedFrom":subQ3}),1.0]])]});}
            var Q38;
            {var subQ0=sQuery(id+"F0.wireOp",EDGE,"E58");var subQ3=sQuery(id+"F0.wireOp",EDGE,"E41");var subQ4=makeQuery(id+"F0.imprint","INTERSECT",VERTEX,{"derivedFrom":[subQ3,subQ0]});Q38=makeQuery(id+"F0.imprint","IMPRINT",FACE,{"disambiguationData":[TD([[makeQuery(id+"F0.imprint","IMPRINT",EDGE,{"disambiguationData":[TD([[subQ4,-1.0]])],"derivedFrom":subQ3}),1.0]])]});}
            var Q39;
            {var subQ3=sQuery(id+"F0.wireOp",EDGE,"E41");var subQ5=sQuery(id+"F0.wireOp",EDGE,"E48");var subQ7=makeQuery(id+"F0.imprint","INTERSECT",VERTEX,{"derivedFrom":[subQ3,subQ5]});Q39=makeQuery(id+"F0.imprint","IMPRINT",FACE,{"disambiguationData":[TD([[makeQuery(id+"F0.imprint","IMPRINT",EDGE,{"disambiguationData":[TD([[subQ7,-1.0]])],"derivedFrom":subQ3}),1.0]])]});}
            var Q40;
            {var subQ3=sQuery(id+"F0.wireOp",EDGE,"E41");var subQ5=sQuery(id+"F0.wireOp",EDGE,"E49");var subQ7=makeQuery(id+"F0.imprint","INTERSECT",VERTEX,{"derivedFrom":[subQ3,subQ5]});Q40=makeQuery(id+"F0.imprint","IMPRINT",FACE,{"disambiguationData":[TD([[makeQuery(id+"F0.imprint","IMPRINT",EDGE,{"disambiguationData":[TD([[subQ7,-1.0]])],"derivedFrom":subQ3}),1.0]])]});}
            var Q41;
            {var subQ3=sQuery(id+"F0.wireOp",EDGE,"E38");var subQ5=sQuery(id+"F0.wireOp",EDGE,"E51");var subQ7=makeQuery(id+"F0.imprint","INTERSECT",VERTEX,{"derivedFrom":[subQ3,subQ5]});Q41=makeQuery(id+"F0.imprint","IMPRINT",FACE,{"disambiguationData":[TD([[makeQuery(id+"F0.imprint","IMPRINT",EDGE,{"disambiguationData":[TD([[subQ7,-1.0]])],"derivedFrom":subQ3}),1.0]])]});}
            var Q42;
            {var subQ3=sQuery(id+"F0.wireOp",EDGE,"E39");var subQ5=sQuery(id+"F0.wireOp",EDGE,"E51");var subQ7=makeQuery(id+"F0.imprint","INTERSECT",VERTEX,{"derivedFrom":[subQ3,subQ5]});Q42=makeQuery(id+"F0.imprint","IMPRINT",FACE,{"disambiguationData":[TD([[makeQuery(id+"F0.imprint","IMPRINT",EDGE,{"disambiguationData":[TD([[subQ7,-1.0]])],"derivedFrom":subQ3}),1.0]])]});}
            extrude(context, id + "F4", {"entities" : qUnion([Q0, Q1, Q2, Q3, Q4, Q5, Q6, Q7, Q8, Q9, Q10, Q11, Q12, Q13, Q14, Q15, Q16, Q17, Q18, Q19, Q20, Q21, Q22, Q23, Q24, Q25, Q26, Q27, Q28, Q29, Q30, Q31, Q32, Q33, Q34, Q35, Q36, Q37, Q38, Q39, Q40, Q41, Q42]), "endBound" : BoundingType.SYMMETRIC, "depth" : 9.96 * mm});
        }
        {
            var Q0;
            {var subQ1=sQuery(id+"F0.wireOp",EDGE,"E45");var subQ5=sQuery(id+"F0.wireOp",EDGE,"E53");var subQ6=makeQuery(id+"F0.imprint","INTERSECT",VERTEX,{"derivedFrom":[subQ1,subQ5]});Q0=makeQuery(id+"F0.imprint","IMPRINT",FACE,{"disambiguationData":[TD([[makeQuery(id+"F0.imprint","IMPRINT",EDGE,{"disambiguationData":[TD([[subQ6,-1.0]])],"derivedFrom":subQ1}),1.0]])]});}
            var Q1;
            {var subQ1=sQuery(id+"F0.wireOp",EDGE,"E45");var subQ5=sQuery(id+"F0.wireOp",EDGE,"E48");var subQ6=makeQuery(id+"F0.imprint","INTERSECT",VERTEX,{"derivedFrom":[subQ1,subQ5]});Q1=makeQuery(id+"F0.imprint","IMPRINT",FACE,{"disambiguationData":[TD([[makeQuery(id+"F0.imprint","IMPRINT",EDGE,{"disambiguationData":[TD([[subQ6,-1.0]])],"derivedFrom":subQ1}),1.0]])]});}
            var Q2;
            {var subQ1=sQuery(id+"F0.wireOp",EDGE,"E45");var subQ5=sQuery(id+"F0.wireOp",EDGE,"E52");var subQ6=makeQuery(id+"F0.imprint","INTERSECT",VERTEX,{"derivedFrom":[subQ1,subQ5]});Q2=makeQuery(id+"F0.imprint","IMPRINT",FACE,{"disambiguationData":[TD([[makeQuery(id+"F0.imprint","IMPRINT",EDGE,{"disambiguationData":[TD([[subQ6,-1.0]])],"derivedFrom":subQ1}),1.0]])]});}
            var Q3;
            {var subQ1=sQuery(id+"F0.wireOp",EDGE,"E45");var subQ5=sQuery(id+"F0.wireOp",EDGE,"E47");var subQ6=makeQuery(id+"F0.imprint","INTERSECT",VERTEX,{"derivedFrom":[subQ1,subQ5]});Q3=makeQuery(id+"F0.imprint","IMPRINT",FACE,{"disambiguationData":[TD([[makeQuery(id+"F0.imprint","IMPRINT",EDGE,{"disambiguationData":[TD([[subQ6,-1.0]])],"derivedFrom":subQ1}),1.0]])]});}
            var Q4;
            {var subQ1=sQuery(id+"F0.wireOp",EDGE,"E45");var subQ5=sQuery(id+"F0.wireOp",EDGE,"E54");var subQ6=makeQuery(id+"F0.imprint","INTERSECT",VERTEX,{"derivedFrom":[subQ1,subQ5]});Q4=makeQuery(id+"F0.imprint","IMPRINT",FACE,{"disambiguationData":[TD([[makeQuery(id+"F0.imprint","IMPRINT",EDGE,{"disambiguationData":[TD([[subQ6,-1.0]])],"derivedFrom":subQ1}),1.0]])]});}
            var Q5;
            {var subQ1=sQuery(id+"F0.wireOp",EDGE,"E45");var subQ5=sQuery(id+"F0.wireOp",EDGE,"E37");var subQ7=makeQuery(id+"F0.imprint","INTERSECT",VERTEX,{"derivedFrom":[subQ5,subQ1]});Q5=makeQuery(id+"F0.imprint","IMPRINT",FACE,{"disambiguationData":[TD([[makeQuery(id+"F0.imprint","IMPRINT",EDGE,{"disambiguationData":[TD([[subQ7,1.0]])],"derivedFrom":subQ5}),-1.0]])]});}
            var Q6;
            {var subQ1=sQuery(id+"F0.wireOp",EDGE,"E45");var subQ5=sQuery(id+"F0.wireOp",EDGE,"E55");var subQ6=makeQuery(id+"F0.imprint","INTERSECT",VERTEX,{"derivedFrom":[subQ1,subQ5]});Q6=makeQuery(id+"F0.imprint","IMPRINT",FACE,{"disambiguationData":[TD([[makeQuery(id+"F0.imprint","IMPRINT",EDGE,{"disambiguationData":[TD([[subQ6,-1.0]])],"derivedFrom":subQ1}),1.0]])]});}
            var Q7;
            {var subQ1=sQuery(id+"F0.wireOp",EDGE,"E45");var subQ5=sQuery(id+"F0.wireOp",EDGE,"E50");var subQ6=makeQuery(id+"F0.imprint","INTERSECT",VERTEX,{"derivedFrom":[subQ1,subQ5]});Q7=makeQuery(id+"F0.imprint","IMPRINT",FACE,{"disambiguationData":[TD([[makeQuery(id+"F0.imprint","IMPRINT",EDGE,{"disambiguationData":[TD([[subQ6,-1.0]])],"derivedFrom":subQ1}),1.0]])]});}
            var Q8;
            {var subQ1=sQuery(id+"F0.wireOp",EDGE,"E45");var subQ5=sQuery(id+"F0.wireOp",EDGE,"E57");var subQ6=makeQuery(id+"F0.imprint","INTERSECT",VERTEX,{"derivedFrom":[subQ1,subQ5]});Q8=makeQuery(id+"F0.imprint","IMPRINT",FACE,{"disambiguationData":[TD([[makeQuery(id+"F0.imprint","IMPRINT",EDGE,{"disambiguationData":[TD([[subQ6,-1.0]])],"derivedFrom":subQ1}),1.0]])]});}
            var Q9;
            {var subQ0=sQuery(id+"F0.wireOp",EDGE,"E58");var subQ1=sQuery(id+"F0.wireOp",EDGE,"E45");var subQ2=makeQuery(id+"F0.imprint","INTERSECT",VERTEX,{"derivedFrom":[subQ1,subQ0]});Q9=makeQuery(id+"F0.imprint","IMPRINT",FACE,{"disambiguationData":[TD([[makeQuery(id+"F0.imprint","IMPRINT",EDGE,{"disambiguationData":[TD([[subQ2,-1.0]])],"derivedFrom":subQ1}),1.0]])]});}
            var Q10;
            {var subQ0=sQuery(id+"F0.wireOp",EDGE,"E56");var subQ1=sQuery(id+"F0.wireOp",EDGE,"E45");var subQ2=makeQuery(id+"F0.imprint","INTERSECT",VERTEX,{"derivedFrom":[subQ1,subQ0]});Q10=makeQuery(id+"F0.imprint","IMPRINT",FACE,{"disambiguationData":[TD([[makeQuery(id+"F0.imprint","IMPRINT",EDGE,{"disambiguationData":[TD([[subQ2,-1.0]])],"derivedFrom":subQ1}),1.0]])]});}
            var Q11;
            {var subQ1=sQuery(id+"F0.wireOp",EDGE,"E45");var subQ5=sQuery(id+"F0.wireOp",EDGE,"E51");var subQ6=makeQuery(id+"F0.imprint","INTERSECT",VERTEX,{"derivedFrom":[subQ1,subQ5]});Q11=makeQuery(id+"F0.imprint","IMPRINT",FACE,{"disambiguationData":[TD([[makeQuery(id+"F0.imprint","IMPRINT",EDGE,{"disambiguationData":[TD([[subQ6,-1.0]])],"derivedFrom":subQ1}),1.0]])]});}
            var Q12;
            {var subQ1=sQuery(id+"F0.wireOp",EDGE,"E45");var subQ5=sQuery(id+"F0.wireOp",EDGE,"E49");var subQ6=makeQuery(id+"F0.imprint","INTERSECT",VERTEX,{"derivedFrom":[subQ1,subQ5]});Q12=makeQuery(id+"F0.imprint","IMPRINT",FACE,{"disambiguationData":[TD([[makeQuery(id+"F0.imprint","IMPRINT",EDGE,{"disambiguationData":[TD([[subQ6,-1.0]])],"derivedFrom":subQ1}),1.0]])]});}
            var Q13;
            {var subQ3=sQuery(id+"F0.wireOp",EDGE,"E36");var subQ5=sQuery(id+"F0.wireOp",EDGE,"E47");var subQ7=makeQuery(id+"F0.imprint","INTERSECT",VERTEX,{"derivedFrom":[subQ3,subQ5]});Q13=makeQuery(id+"F0.imprint","IMPRINT",FACE,{"disambiguationData":[TD([[makeQuery(id+"F0.imprint","IMPRINT",EDGE,{"disambiguationData":[TD([[subQ7,-1.0]])],"derivedFrom":subQ3}),1.0]])]});}
            var Q14;
            {var subQ3=sQuery(id+"F0.wireOp",EDGE,"E40");var subQ5=sQuery(id+"F0.wireOp",EDGE,"E47");var subQ7=makeQuery(id+"F0.imprint","INTERSECT",VERTEX,{"derivedFrom":[subQ3,subQ5]});Q14=makeQuery(id+"F0.imprint","IMPRINT",FACE,{"disambiguationData":[TD([[makeQuery(id+"F0.imprint","IMPRINT",EDGE,{"disambiguationData":[TD([[subQ7,-1.0]])],"derivedFrom":subQ3}),1.0]])]});}
            var Q15;
            {var subQ3=sQuery(id+"F0.wireOp",EDGE,"E41");var subQ5=sQuery(id+"F0.wireOp",EDGE,"E47");var subQ7=makeQuery(id+"F0.imprint","INTERSECT",VERTEX,{"derivedFrom":[subQ3,subQ5]});Q15=makeQuery(id+"F0.imprint","IMPRINT",FACE,{"disambiguationData":[TD([[makeQuery(id+"F0.imprint","IMPRINT",EDGE,{"disambiguationData":[TD([[subQ7,-1.0]])],"derivedFrom":subQ3}),1.0]])]});}
            var Q16;
            {var subQ3=sQuery(id+"F0.wireOp",EDGE,"E44");var subQ5=sQuery(id+"F0.wireOp",EDGE,"E47");var subQ7=makeQuery(id+"F0.imprint","INTERSECT",VERTEX,{"derivedFrom":[subQ3,subQ5]});Q16=makeQuery(id+"F0.imprint","IMPRINT",FACE,{"disambiguationData":[TD([[makeQuery(id+"F0.imprint","IMPRINT",EDGE,{"disambiguationData":[TD([[subQ7,-1.0]])],"derivedFrom":subQ3}),1.0]])]});}
            var Q17;
            {var subQ3=sQuery(id+"F0.wireOp",EDGE,"E42");var subQ5=sQuery(id+"F0.wireOp",EDGE,"E47");var subQ7=makeQuery(id+"F0.imprint","INTERSECT",VERTEX,{"derivedFrom":[subQ3,subQ5]});Q17=makeQuery(id+"F0.imprint","IMPRINT",FACE,{"disambiguationData":[TD([[makeQuery(id+"F0.imprint","IMPRINT",EDGE,{"disambiguationData":[TD([[subQ7,-1.0]])],"derivedFrom":subQ3}),1.0]])]});}
            var Q18;
            {var subQ3=sQuery(id+"F0.wireOp",EDGE,"E38");var subQ5=sQuery(id+"F0.wireOp",EDGE,"E47");var subQ7=makeQuery(id+"F0.imprint","INTERSECT",VERTEX,{"derivedFrom":[subQ3,subQ5]});Q18=makeQuery(id+"F0.imprint","IMPRINT",FACE,{"disambiguationData":[TD([[makeQuery(id+"F0.imprint","IMPRINT",EDGE,{"disambiguationData":[TD([[subQ7,-1.0]])],"derivedFrom":subQ3}),1.0]])]});}
            var Q19;
            {var subQ3=sQuery(id+"F0.wireOp",EDGE,"E39");var subQ5=sQuery(id+"F0.wireOp",EDGE,"E47");var subQ7=makeQuery(id+"F0.imprint","INTERSECT",VERTEX,{"derivedFrom":[subQ3,subQ5]});Q19=makeQuery(id+"F0.imprint","IMPRINT",FACE,{"disambiguationData":[TD([[makeQuery(id+"F0.imprint","IMPRINT",EDGE,{"disambiguationData":[TD([[subQ7,-1.0]])],"derivedFrom":subQ3}),1.0]])]});}
            var Q20;
            {var subQ3=sQuery(id+"F0.wireOp",EDGE,"E43");var subQ5=sQuery(id+"F0.wireOp",EDGE,"E47");var subQ7=makeQuery(id+"F0.imprint","INTERSECT",VERTEX,{"derivedFrom":[subQ3,subQ5]});Q20=makeQuery(id+"F0.imprint","IMPRINT",FACE,{"disambiguationData":[TD([[makeQuery(id+"F0.imprint","IMPRINT",EDGE,{"disambiguationData":[TD([[subQ7,-1.0]])],"derivedFrom":subQ3}),1.0]])]});}
            var Q21;
            {var subQ3=sQuery(id+"F0.wireOp",EDGE,"E39");var subQ5=sQuery(id+"F0.wireOp",EDGE,"E37");var subQ7=makeQuery(id+"F0.imprint","INTERSECT",VERTEX,{"derivedFrom":[subQ5,subQ3]});Q21=makeQuery(id+"F0.imprint","IMPRINT",FACE,{"disambiguationData":[TD([[makeQuery(id+"F0.imprint","IMPRINT",EDGE,{"disambiguationData":[TD([[subQ7,1.0]])],"derivedFrom":subQ5}),-1.0]])]});}
            var Q22;
            {var subQ3=sQuery(id+"F0.wireOp",EDGE,"E36");var subQ5=sQuery(id+"F0.wireOp",EDGE,"E37");var subQ7=makeQuery(id+"F0.imprint","INTERSECT",VERTEX,{"derivedFrom":[subQ3,subQ5]});Q22=makeQuery(id+"F0.imprint","IMPRINT",FACE,{"disambiguationData":[TD([[makeQuery(id+"F0.imprint","IMPRINT",EDGE,{"disambiguationData":[TD([[subQ7,1.0]])],"derivedFrom":subQ3}),1.0]])]});}
            var Q23;
            {var subQ3=sQuery(id+"F0.wireOp",EDGE,"E40");var subQ5=sQuery(id+"F0.wireOp",EDGE,"E37");var subQ7=makeQuery(id+"F0.imprint","INTERSECT",VERTEX,{"derivedFrom":[subQ5,subQ3]});Q23=makeQuery(id+"F0.imprint","IMPRINT",FACE,{"disambiguationData":[TD([[makeQuery(id+"F0.imprint","IMPRINT",EDGE,{"disambiguationData":[TD([[subQ7,1.0]])],"derivedFrom":subQ5}),-1.0]])]});}
            var Q24;
            {var subQ3=sQuery(id+"F0.wireOp",EDGE,"E41");var subQ5=sQuery(id+"F0.wireOp",EDGE,"E37");var subQ7=makeQuery(id+"F0.imprint","INTERSECT",VERTEX,{"derivedFrom":[subQ5,subQ3]});Q24=makeQuery(id+"F0.imprint","IMPRINT",FACE,{"disambiguationData":[TD([[makeQuery(id+"F0.imprint","IMPRINT",EDGE,{"disambiguationData":[TD([[subQ7,1.0]])],"derivedFrom":subQ5}),-1.0]])]});}
            var Q25;
            {var subQ3=sQuery(id+"F0.wireOp",EDGE,"E44");var subQ5=sQuery(id+"F0.wireOp",EDGE,"E37");var subQ7=makeQuery(id+"F0.imprint","INTERSECT",VERTEX,{"derivedFrom":[subQ5,subQ3]});Q25=makeQuery(id+"F0.imprint","IMPRINT",FACE,{"disambiguationData":[TD([[makeQuery(id+"F0.imprint","IMPRINT",EDGE,{"disambiguationData":[TD([[subQ7,1.0]])],"derivedFrom":subQ5}),-1.0]])]});}
            var Q26;
            {var subQ3=sQuery(id+"F0.wireOp",EDGE,"E42");var subQ5=sQuery(id+"F0.wireOp",EDGE,"E37");var subQ7=makeQuery(id+"F0.imprint","INTERSECT",VERTEX,{"derivedFrom":[subQ5,subQ3]});Q26=makeQuery(id+"F0.imprint","IMPRINT",FACE,{"disambiguationData":[TD([[makeQuery(id+"F0.imprint","IMPRINT",EDGE,{"disambiguationData":[TD([[subQ7,1.0]])],"derivedFrom":subQ5}),-1.0]])]});}
            var Q27;
            {var subQ3=sQuery(id+"F0.wireOp",EDGE,"E38");var subQ5=sQuery(id+"F0.wireOp",EDGE,"E37");var subQ7=makeQuery(id+"F0.imprint","INTERSECT",VERTEX,{"derivedFrom":[subQ5,subQ3]});Q27=makeQuery(id+"F0.imprint","IMPRINT",FACE,{"disambiguationData":[TD([[makeQuery(id+"F0.imprint","IMPRINT",EDGE,{"disambiguationData":[TD([[subQ7,1.0]])],"derivedFrom":subQ5}),-1.0]])]});}
            var Q28;
            {var subQ3=sQuery(id+"F0.wireOp",EDGE,"E43");var subQ5=sQuery(id+"F0.wireOp",EDGE,"E37");var subQ7=makeQuery(id+"F0.imprint","INTERSECT",VERTEX,{"derivedFrom":[subQ5,subQ3]});Q28=makeQuery(id+"F0.imprint","IMPRINT",FACE,{"disambiguationData":[TD([[makeQuery(id+"F0.imprint","IMPRINT",EDGE,{"disambiguationData":[TD([[subQ7,1.0]])],"derivedFrom":subQ5}),-1.0]])]});}
            var Q29;
            {var subQ3=sQuery(id+"F0.wireOp",EDGE,"E36");var subQ5=sQuery(id+"F0.wireOp",EDGE,"E49");var subQ7=makeQuery(id+"F0.imprint","INTERSECT",VERTEX,{"derivedFrom":[subQ3,subQ5]});Q29=makeQuery(id+"F0.imprint","IMPRINT",FACE,{"disambiguationData":[TD([[makeQuery(id+"F0.imprint","IMPRINT",EDGE,{"disambiguationData":[TD([[subQ7,-1.0]])],"derivedFrom":subQ3}),1.0]])]});}
            var Q30;
            {var subQ3=sQuery(id+"F0.wireOp",EDGE,"E36");var subQ5=sQuery(id+"F0.wireOp",EDGE,"E48");var subQ7=makeQuery(id+"F0.imprint","INTERSECT",VERTEX,{"derivedFrom":[subQ3,subQ5]});Q30=makeQuery(id+"F0.imprint","IMPRINT",FACE,{"disambiguationData":[TD([[makeQuery(id+"F0.imprint","IMPRINT",EDGE,{"disambiguationData":[TD([[subQ7,-1.0]])],"derivedFrom":subQ3}),1.0]])]});}
            var Q31;
            {var subQ3=sQuery(id+"F0.wireOp",EDGE,"E36");var subQ5=sQuery(id+"F0.wireOp",EDGE,"E57");var subQ7=makeQuery(id+"F0.imprint","INTERSECT",VERTEX,{"derivedFrom":[subQ3,subQ5]});Q31=makeQuery(id+"F0.imprint","IMPRINT",FACE,{"disambiguationData":[TD([[makeQuery(id+"F0.imprint","IMPRINT",EDGE,{"disambiguationData":[TD([[subQ7,-1.0]])],"derivedFrom":subQ3}),1.0]])]});}
            var Q32;
            {var subQ3=sQuery(id+"F0.wireOp",EDGE,"E36");var subQ5=sQuery(id+"F0.wireOp",EDGE,"E58");var subQ7=makeQuery(id+"F0.imprint","INTERSECT",VERTEX,{"derivedFrom":[subQ3,subQ5]});Q32=makeQuery(id+"F0.imprint","IMPRINT",FACE,{"disambiguationData":[TD([[makeQuery(id+"F0.imprint","IMPRINT",EDGE,{"disambiguationData":[TD([[subQ7,-1.0]])],"derivedFrom":subQ3}),1.0]])]});}
            var Q33;
            {var subQ3=sQuery(id+"F0.wireOp",EDGE,"E36");var subQ5=sQuery(id+"F0.wireOp",EDGE,"E53");var subQ7=makeQuery(id+"F0.imprint","INTERSECT",VERTEX,{"derivedFrom":[subQ3,subQ5]});Q33=makeQuery(id+"F0.imprint","IMPRINT",FACE,{"disambiguationData":[TD([[makeQuery(id+"F0.imprint","IMPRINT",EDGE,{"disambiguationData":[TD([[subQ7,-1.0]])],"derivedFrom":subQ3}),1.0]])]});}
            var Q34;
            {var subQ3=sQuery(id+"F0.wireOp",EDGE,"E36");var subQ5=sQuery(id+"F0.wireOp",EDGE,"E52");var subQ7=makeQuery(id+"F0.imprint","INTERSECT",VERTEX,{"derivedFrom":[subQ3,subQ5]});Q34=makeQuery(id+"F0.imprint","IMPRINT",FACE,{"disambiguationData":[TD([[makeQuery(id+"F0.imprint","IMPRINT",EDGE,{"disambiguationData":[TD([[subQ7,-1.0]])],"derivedFrom":subQ3}),1.0]])]});}
            var Q35;
            {var subQ3=sQuery(id+"F0.wireOp",EDGE,"E36");var subQ5=sQuery(id+"F0.wireOp",EDGE,"E51");var subQ7=makeQuery(id+"F0.imprint","INTERSECT",VERTEX,{"derivedFrom":[subQ3,subQ5]});Q35=makeQuery(id+"F0.imprint","IMPRINT",FACE,{"disambiguationData":[TD([[makeQuery(id+"F0.imprint","IMPRINT",EDGE,{"disambiguationData":[TD([[subQ7,-1.0]])],"derivedFrom":subQ3}),1.0]])]});}
            var Q36;
            {var subQ3=sQuery(id+"F0.wireOp",EDGE,"E36");var subQ5=sQuery(id+"F0.wireOp",EDGE,"E50");var subQ7=makeQuery(id+"F0.imprint","INTERSECT",VERTEX,{"derivedFrom":[subQ3,subQ5]});Q36=makeQuery(id+"F0.imprint","IMPRINT",FACE,{"disambiguationData":[TD([[makeQuery(id+"F0.imprint","IMPRINT",EDGE,{"disambiguationData":[TD([[subQ7,-1.0]])],"derivedFrom":subQ3}),1.0]])]});}
            var Q37;
            {var subQ3=sQuery(id+"F0.wireOp",EDGE,"E41");var subQ5=sQuery(id+"F0.wireOp",EDGE,"E48");var subQ7=makeQuery(id+"F0.imprint","INTERSECT",VERTEX,{"derivedFrom":[subQ3,subQ5]});Q37=makeQuery(id+"F0.imprint","IMPRINT",FACE,{"disambiguationData":[TD([[makeQuery(id+"F0.imprint","IMPRINT",EDGE,{"disambiguationData":[TD([[subQ7,-1.0]])],"derivedFrom":subQ3}),1.0]])]});}
            var Q38;
            {var subQ3=sQuery(id+"F0.wireOp",EDGE,"E41");var subQ5=sQuery(id+"F0.wireOp",EDGE,"E49");var subQ7=makeQuery(id+"F0.imprint","INTERSECT",VERTEX,{"derivedFrom":[subQ3,subQ5]});Q38=makeQuery(id+"F0.imprint","IMPRINT",FACE,{"disambiguationData":[TD([[makeQuery(id+"F0.imprint","IMPRINT",EDGE,{"disambiguationData":[TD([[subQ7,-1.0]])],"derivedFrom":subQ3}),1.0]])]});}
            var Q39;
            {var subQ3=sQuery(id+"F0.wireOp",EDGE,"E41");var subQ5=sQuery(id+"F0.wireOp",EDGE,"E57");var subQ7=makeQuery(id+"F0.imprint","INTERSECT",VERTEX,{"derivedFrom":[subQ3,subQ5]});Q39=makeQuery(id+"F0.imprint","IMPRINT",FACE,{"disambiguationData":[TD([[makeQuery(id+"F0.imprint","IMPRINT",EDGE,{"disambiguationData":[TD([[subQ7,-1.0]])],"derivedFrom":subQ3}),1.0]])]});}
            var Q40;
            {var subQ0=sQuery(id+"F0.wireOp",EDGE,"E58");var subQ3=sQuery(id+"F0.wireOp",EDGE,"E41");var subQ4=makeQuery(id+"F0.imprint","INTERSECT",VERTEX,{"derivedFrom":[subQ3,subQ0]});Q40=makeQuery(id+"F0.imprint","IMPRINT",FACE,{"disambiguationData":[TD([[makeQuery(id+"F0.imprint","IMPRINT",EDGE,{"disambiguationData":[TD([[subQ4,-1.0]])],"derivedFrom":subQ3}),1.0]])]});}
            extrude(context, id + "F5", {"entities" : qUnion([Q0, Q1, Q2, Q3, Q4, Q5, Q6, Q7, Q8, Q9, Q10, Q11, Q12, Q13, Q14, Q15, Q16, Q17, Q18, Q19, Q20, Q21, Q22, Q23, Q24, Q25, Q26, Q27, Q28, Q29, Q30, Q31, Q32, Q33, Q34, Q35, Q36, Q37, Q38, Q39, Q40]), "endBound" : BoundingType.SYMMETRIC, "depth" : 9.96 * mm});
        }
        {
            var Q0;
            {var subQ1=sQuery(id+"F0.wireOp",EDGE,"E45");var subQ5=sQuery(id+"F0.wireOp",EDGE,"E53");var subQ6=makeQuery(id+"F0.imprint","INTERSECT",VERTEX,{"derivedFrom":[subQ1,subQ5]});Q0=makeQuery(id+"F0.imprint","IMPRINT",FACE,{"disambiguationData":[TD([[makeQuery(id+"F0.imprint","IMPRINT",EDGE,{"disambiguationData":[TD([[subQ6,-1.0]])],"derivedFrom":subQ1}),1.0]])]});}
            var Q1;
            {var subQ1=sQuery(id+"F0.wireOp",EDGE,"E45");var subQ5=sQuery(id+"F0.wireOp",EDGE,"E48");var subQ6=makeQuery(id+"F0.imprint","INTERSECT",VERTEX,{"derivedFrom":[subQ1,subQ5]});Q1=makeQuery(id+"F0.imprint","IMPRINT",FACE,{"disambiguationData":[TD([[makeQuery(id+"F0.imprint","IMPRINT",EDGE,{"disambiguationData":[TD([[subQ6,-1.0]])],"derivedFrom":subQ1}),1.0]])]});}
            var Q2;
            {var subQ1=sQuery(id+"F0.wireOp",EDGE,"E45");var subQ5=sQuery(id+"F0.wireOp",EDGE,"E52");var subQ6=makeQuery(id+"F0.imprint","INTERSECT",VERTEX,{"derivedFrom":[subQ1,subQ5]});Q2=makeQuery(id+"F0.imprint","IMPRINT",FACE,{"disambiguationData":[TD([[makeQuery(id+"F0.imprint","IMPRINT",EDGE,{"disambiguationData":[TD([[subQ6,-1.0]])],"derivedFrom":subQ1}),1.0]])]});}
            var Q3;
            {var subQ1=sQuery(id+"F0.wireOp",EDGE,"E45");var subQ5=sQuery(id+"F0.wireOp",EDGE,"E47");var subQ6=makeQuery(id+"F0.imprint","INTERSECT",VERTEX,{"derivedFrom":[subQ1,subQ5]});Q3=makeQuery(id+"F0.imprint","IMPRINT",FACE,{"disambiguationData":[TD([[makeQuery(id+"F0.imprint","IMPRINT",EDGE,{"disambiguationData":[TD([[subQ6,-1.0]])],"derivedFrom":subQ1}),1.0]])]});}
            var Q4;
            {var subQ1=sQuery(id+"F0.wireOp",EDGE,"E45");var subQ5=sQuery(id+"F0.wireOp",EDGE,"E54");var subQ6=makeQuery(id+"F0.imprint","INTERSECT",VERTEX,{"derivedFrom":[subQ1,subQ5]});Q4=makeQuery(id+"F0.imprint","IMPRINT",FACE,{"disambiguationData":[TD([[makeQuery(id+"F0.imprint","IMPRINT",EDGE,{"disambiguationData":[TD([[subQ6,-1.0]])],"derivedFrom":subQ1}),1.0]])]});}
            var Q5;
            {var subQ1=sQuery(id+"F0.wireOp",EDGE,"E45");var subQ5=sQuery(id+"F0.wireOp",EDGE,"E37");var subQ7=makeQuery(id+"F0.imprint","INTERSECT",VERTEX,{"derivedFrom":[subQ5,subQ1]});Q5=makeQuery(id+"F0.imprint","IMPRINT",FACE,{"disambiguationData":[TD([[makeQuery(id+"F0.imprint","IMPRINT",EDGE,{"disambiguationData":[TD([[subQ7,1.0]])],"derivedFrom":subQ5}),-1.0]])]});}
            var Q6;
            {var subQ1=sQuery(id+"F0.wireOp",EDGE,"E45");var subQ5=sQuery(id+"F0.wireOp",EDGE,"E55");var subQ6=makeQuery(id+"F0.imprint","INTERSECT",VERTEX,{"derivedFrom":[subQ1,subQ5]});Q6=makeQuery(id+"F0.imprint","IMPRINT",FACE,{"disambiguationData":[TD([[makeQuery(id+"F0.imprint","IMPRINT",EDGE,{"disambiguationData":[TD([[subQ6,-1.0]])],"derivedFrom":subQ1}),1.0]])]});}
            var Q7;
            {var subQ1=sQuery(id+"F0.wireOp",EDGE,"E45");var subQ5=sQuery(id+"F0.wireOp",EDGE,"E50");var subQ6=makeQuery(id+"F0.imprint","INTERSECT",VERTEX,{"derivedFrom":[subQ1,subQ5]});Q7=makeQuery(id+"F0.imprint","IMPRINT",FACE,{"disambiguationData":[TD([[makeQuery(id+"F0.imprint","IMPRINT",EDGE,{"disambiguationData":[TD([[subQ6,-1.0]])],"derivedFrom":subQ1}),1.0]])]});}
            var Q8;
            {var subQ1=sQuery(id+"F0.wireOp",EDGE,"E45");var subQ5=sQuery(id+"F0.wireOp",EDGE,"E57");var subQ6=makeQuery(id+"F0.imprint","INTERSECT",VERTEX,{"derivedFrom":[subQ1,subQ5]});Q8=makeQuery(id+"F0.imprint","IMPRINT",FACE,{"disambiguationData":[TD([[makeQuery(id+"F0.imprint","IMPRINT",EDGE,{"disambiguationData":[TD([[subQ6,-1.0]])],"derivedFrom":subQ1}),1.0]])]});}
            var Q9;
            {var subQ0=sQuery(id+"F0.wireOp",EDGE,"E58");var subQ1=sQuery(id+"F0.wireOp",EDGE,"E45");var subQ2=makeQuery(id+"F0.imprint","INTERSECT",VERTEX,{"derivedFrom":[subQ1,subQ0]});Q9=makeQuery(id+"F0.imprint","IMPRINT",FACE,{"disambiguationData":[TD([[makeQuery(id+"F0.imprint","IMPRINT",EDGE,{"disambiguationData":[TD([[subQ2,-1.0]])],"derivedFrom":subQ1}),1.0]])]});}
            var Q10;
            {var subQ0=sQuery(id+"F0.wireOp",EDGE,"E56");var subQ1=sQuery(id+"F0.wireOp",EDGE,"E45");var subQ2=makeQuery(id+"F0.imprint","INTERSECT",VERTEX,{"derivedFrom":[subQ1,subQ0]});Q10=makeQuery(id+"F0.imprint","IMPRINT",FACE,{"disambiguationData":[TD([[makeQuery(id+"F0.imprint","IMPRINT",EDGE,{"disambiguationData":[TD([[subQ2,-1.0]])],"derivedFrom":subQ1}),1.0]])]});}
            var Q11;
            {var subQ1=sQuery(id+"F0.wireOp",EDGE,"E45");var subQ5=sQuery(id+"F0.wireOp",EDGE,"E51");var subQ6=makeQuery(id+"F0.imprint","INTERSECT",VERTEX,{"derivedFrom":[subQ1,subQ5]});Q11=makeQuery(id+"F0.imprint","IMPRINT",FACE,{"disambiguationData":[TD([[makeQuery(id+"F0.imprint","IMPRINT",EDGE,{"disambiguationData":[TD([[subQ6,-1.0]])],"derivedFrom":subQ1}),1.0]])]});}
            var Q12;
            {var subQ1=sQuery(id+"F0.wireOp",EDGE,"E45");var subQ5=sQuery(id+"F0.wireOp",EDGE,"E49");var subQ6=makeQuery(id+"F0.imprint","INTERSECT",VERTEX,{"derivedFrom":[subQ1,subQ5]});Q12=makeQuery(id+"F0.imprint","IMPRINT",FACE,{"disambiguationData":[TD([[makeQuery(id+"F0.imprint","IMPRINT",EDGE,{"disambiguationData":[TD([[subQ6,-1.0]])],"derivedFrom":subQ1}),1.0]])]});}
            var Q13;
            {var subQ3=sQuery(id+"F0.wireOp",EDGE,"E39");var subQ5=sQuery(id+"F0.wireOp",EDGE,"E37");var subQ7=makeQuery(id+"F0.imprint","INTERSECT",VERTEX,{"derivedFrom":[subQ5,subQ3]});Q13=makeQuery(id+"F0.imprint","IMPRINT",FACE,{"disambiguationData":[TD([[makeQuery(id+"F0.imprint","IMPRINT",EDGE,{"disambiguationData":[TD([[subQ7,1.0]])],"derivedFrom":subQ5}),-1.0]])]});}
            var Q14;
            {var subQ3=sQuery(id+"F0.wireOp",EDGE,"E36");var subQ5=sQuery(id+"F0.wireOp",EDGE,"E37");var subQ7=makeQuery(id+"F0.imprint","INTERSECT",VERTEX,{"derivedFrom":[subQ3,subQ5]});Q14=makeQuery(id+"F0.imprint","IMPRINT",FACE,{"disambiguationData":[TD([[makeQuery(id+"F0.imprint","IMPRINT",EDGE,{"disambiguationData":[TD([[subQ7,1.0]])],"derivedFrom":subQ3}),1.0]])]});}
            var Q15;
            {var subQ3=sQuery(id+"F0.wireOp",EDGE,"E40");var subQ5=sQuery(id+"F0.wireOp",EDGE,"E37");var subQ7=makeQuery(id+"F0.imprint","INTERSECT",VERTEX,{"derivedFrom":[subQ5,subQ3]});Q15=makeQuery(id+"F0.imprint","IMPRINT",FACE,{"disambiguationData":[TD([[makeQuery(id+"F0.imprint","IMPRINT",EDGE,{"disambiguationData":[TD([[subQ7,1.0]])],"derivedFrom":subQ5}),-1.0]])]});}
            var Q16;
            {var subQ3=sQuery(id+"F0.wireOp",EDGE,"E41");var subQ5=sQuery(id+"F0.wireOp",EDGE,"E37");var subQ7=makeQuery(id+"F0.imprint","INTERSECT",VERTEX,{"derivedFrom":[subQ5,subQ3]});Q16=makeQuery(id+"F0.imprint","IMPRINT",FACE,{"disambiguationData":[TD([[makeQuery(id+"F0.imprint","IMPRINT",EDGE,{"disambiguationData":[TD([[subQ7,1.0]])],"derivedFrom":subQ5}),-1.0]])]});}
            var Q17;
            {var subQ3=sQuery(id+"F0.wireOp",EDGE,"E44");var subQ5=sQuery(id+"F0.wireOp",EDGE,"E37");var subQ7=makeQuery(id+"F0.imprint","INTERSECT",VERTEX,{"derivedFrom":[subQ5,subQ3]});Q17=makeQuery(id+"F0.imprint","IMPRINT",FACE,{"disambiguationData":[TD([[makeQuery(id+"F0.imprint","IMPRINT",EDGE,{"disambiguationData":[TD([[subQ7,1.0]])],"derivedFrom":subQ5}),-1.0]])]});}
            var Q18;
            {var subQ3=sQuery(id+"F0.wireOp",EDGE,"E42");var subQ5=sQuery(id+"F0.wireOp",EDGE,"E37");var subQ7=makeQuery(id+"F0.imprint","INTERSECT",VERTEX,{"derivedFrom":[subQ5,subQ3]});Q18=makeQuery(id+"F0.imprint","IMPRINT",FACE,{"disambiguationData":[TD([[makeQuery(id+"F0.imprint","IMPRINT",EDGE,{"disambiguationData":[TD([[subQ7,1.0]])],"derivedFrom":subQ5}),-1.0]])]});}
            var Q19;
            {var subQ3=sQuery(id+"F0.wireOp",EDGE,"E38");var subQ5=sQuery(id+"F0.wireOp",EDGE,"E37");var subQ7=makeQuery(id+"F0.imprint","INTERSECT",VERTEX,{"derivedFrom":[subQ5,subQ3]});Q19=makeQuery(id+"F0.imprint","IMPRINT",FACE,{"disambiguationData":[TD([[makeQuery(id+"F0.imprint","IMPRINT",EDGE,{"disambiguationData":[TD([[subQ7,1.0]])],"derivedFrom":subQ5}),-1.0]])]});}
            var Q20;
            {var subQ3=sQuery(id+"F0.wireOp",EDGE,"E43");var subQ5=sQuery(id+"F0.wireOp",EDGE,"E37");var subQ7=makeQuery(id+"F0.imprint","INTERSECT",VERTEX,{"derivedFrom":[subQ5,subQ3]});Q20=makeQuery(id+"F0.imprint","IMPRINT",FACE,{"disambiguationData":[TD([[makeQuery(id+"F0.imprint","IMPRINT",EDGE,{"disambiguationData":[TD([[subQ7,1.0]])],"derivedFrom":subQ5}),-1.0]])]});}
            var Q21;
            {var subQ3=sQuery(id+"F0.wireOp",EDGE,"E36");var subQ5=sQuery(id+"F0.wireOp",EDGE,"E47");var subQ7=makeQuery(id+"F0.imprint","INTERSECT",VERTEX,{"derivedFrom":[subQ3,subQ5]});Q21=makeQuery(id+"F0.imprint","IMPRINT",FACE,{"disambiguationData":[TD([[makeQuery(id+"F0.imprint","IMPRINT",EDGE,{"disambiguationData":[TD([[subQ7,-1.0]])],"derivedFrom":subQ3}),1.0]])]});}
            var Q22;
            {var subQ3=sQuery(id+"F0.wireOp",EDGE,"E40");var subQ5=sQuery(id+"F0.wireOp",EDGE,"E47");var subQ7=makeQuery(id+"F0.imprint","INTERSECT",VERTEX,{"derivedFrom":[subQ3,subQ5]});Q22=makeQuery(id+"F0.imprint","IMPRINT",FACE,{"disambiguationData":[TD([[makeQuery(id+"F0.imprint","IMPRINT",EDGE,{"disambiguationData":[TD([[subQ7,-1.0]])],"derivedFrom":subQ3}),1.0]])]});}
            var Q23;
            {var subQ3=sQuery(id+"F0.wireOp",EDGE,"E41");var subQ5=sQuery(id+"F0.wireOp",EDGE,"E47");var subQ7=makeQuery(id+"F0.imprint","INTERSECT",VERTEX,{"derivedFrom":[subQ3,subQ5]});Q23=makeQuery(id+"F0.imprint","IMPRINT",FACE,{"disambiguationData":[TD([[makeQuery(id+"F0.imprint","IMPRINT",EDGE,{"disambiguationData":[TD([[subQ7,-1.0]])],"derivedFrom":subQ3}),1.0]])]});}
            var Q24;
            {var subQ3=sQuery(id+"F0.wireOp",EDGE,"E44");var subQ5=sQuery(id+"F0.wireOp",EDGE,"E47");var subQ7=makeQuery(id+"F0.imprint","INTERSECT",VERTEX,{"derivedFrom":[subQ3,subQ5]});Q24=makeQuery(id+"F0.imprint","IMPRINT",FACE,{"disambiguationData":[TD([[makeQuery(id+"F0.imprint","IMPRINT",EDGE,{"disambiguationData":[TD([[subQ7,-1.0]])],"derivedFrom":subQ3}),1.0]])]});}
            var Q25;
            {var subQ3=sQuery(id+"F0.wireOp",EDGE,"E42");var subQ5=sQuery(id+"F0.wireOp",EDGE,"E47");var subQ7=makeQuery(id+"F0.imprint","INTERSECT",VERTEX,{"derivedFrom":[subQ3,subQ5]});Q25=makeQuery(id+"F0.imprint","IMPRINT",FACE,{"disambiguationData":[TD([[makeQuery(id+"F0.imprint","IMPRINT",EDGE,{"disambiguationData":[TD([[subQ7,-1.0]])],"derivedFrom":subQ3}),1.0]])]});}
            var Q26;
            {var subQ3=sQuery(id+"F0.wireOp",EDGE,"E38");var subQ5=sQuery(id+"F0.wireOp",EDGE,"E47");var subQ7=makeQuery(id+"F0.imprint","INTERSECT",VERTEX,{"derivedFrom":[subQ3,subQ5]});Q26=makeQuery(id+"F0.imprint","IMPRINT",FACE,{"disambiguationData":[TD([[makeQuery(id+"F0.imprint","IMPRINT",EDGE,{"disambiguationData":[TD([[subQ7,-1.0]])],"derivedFrom":subQ3}),1.0]])]});}
            var Q27;
            {var subQ3=sQuery(id+"F0.wireOp",EDGE,"E39");var subQ5=sQuery(id+"F0.wireOp",EDGE,"E47");var subQ7=makeQuery(id+"F0.imprint","INTERSECT",VERTEX,{"derivedFrom":[subQ3,subQ5]});Q27=makeQuery(id+"F0.imprint","IMPRINT",FACE,{"disambiguationData":[TD([[makeQuery(id+"F0.imprint","IMPRINT",EDGE,{"disambiguationData":[TD([[subQ7,-1.0]])],"derivedFrom":subQ3}),1.0]])]});}
            var Q28;
            {var subQ3=sQuery(id+"F0.wireOp",EDGE,"E43");var subQ5=sQuery(id+"F0.wireOp",EDGE,"E47");var subQ7=makeQuery(id+"F0.imprint","INTERSECT",VERTEX,{"derivedFrom":[subQ3,subQ5]});Q28=makeQuery(id+"F0.imprint","IMPRINT",FACE,{"disambiguationData":[TD([[makeQuery(id+"F0.imprint","IMPRINT",EDGE,{"disambiguationData":[TD([[subQ7,-1.0]])],"derivedFrom":subQ3}),1.0]])]});}
            var Q29;
            {var subQ3=sQuery(id+"F0.wireOp",EDGE,"E36");var subQ5=sQuery(id+"F0.wireOp",EDGE,"E49");var subQ7=makeQuery(id+"F0.imprint","INTERSECT",VERTEX,{"derivedFrom":[subQ3,subQ5]});Q29=makeQuery(id+"F0.imprint","IMPRINT",FACE,{"disambiguationData":[TD([[makeQuery(id+"F0.imprint","IMPRINT",EDGE,{"disambiguationData":[TD([[subQ7,-1.0]])],"derivedFrom":subQ3}),1.0]])]});}
            var Q30;
            {var subQ3=sQuery(id+"F0.wireOp",EDGE,"E36");var subQ5=sQuery(id+"F0.wireOp",EDGE,"E48");var subQ7=makeQuery(id+"F0.imprint","INTERSECT",VERTEX,{"derivedFrom":[subQ3,subQ5]});Q30=makeQuery(id+"F0.imprint","IMPRINT",FACE,{"disambiguationData":[TD([[makeQuery(id+"F0.imprint","IMPRINT",EDGE,{"disambiguationData":[TD([[subQ7,-1.0]])],"derivedFrom":subQ3}),1.0]])]});}
            var Q31;
            {var subQ3=sQuery(id+"F0.wireOp",EDGE,"E36");var subQ5=sQuery(id+"F0.wireOp",EDGE,"E57");var subQ7=makeQuery(id+"F0.imprint","INTERSECT",VERTEX,{"derivedFrom":[subQ3,subQ5]});Q31=makeQuery(id+"F0.imprint","IMPRINT",FACE,{"disambiguationData":[TD([[makeQuery(id+"F0.imprint","IMPRINT",EDGE,{"disambiguationData":[TD([[subQ7,-1.0]])],"derivedFrom":subQ3}),1.0]])]});}
            var Q32;
            {var subQ3=sQuery(id+"F0.wireOp",EDGE,"E36");var subQ5=sQuery(id+"F0.wireOp",EDGE,"E58");var subQ7=makeQuery(id+"F0.imprint","INTERSECT",VERTEX,{"derivedFrom":[subQ3,subQ5]});Q32=makeQuery(id+"F0.imprint","IMPRINT",FACE,{"disambiguationData":[TD([[makeQuery(id+"F0.imprint","IMPRINT",EDGE,{"disambiguationData":[TD([[subQ7,-1.0]])],"derivedFrom":subQ3}),1.0]])]});}
            var Q33;
            {var subQ3=sQuery(id+"F0.wireOp",EDGE,"E36");var subQ5=sQuery(id+"F0.wireOp",EDGE,"E53");var subQ7=makeQuery(id+"F0.imprint","INTERSECT",VERTEX,{"derivedFrom":[subQ3,subQ5]});Q33=makeQuery(id+"F0.imprint","IMPRINT",FACE,{"disambiguationData":[TD([[makeQuery(id+"F0.imprint","IMPRINT",EDGE,{"disambiguationData":[TD([[subQ7,-1.0]])],"derivedFrom":subQ3}),1.0]])]});}
            var Q34;
            {var subQ3=sQuery(id+"F0.wireOp",EDGE,"E36");var subQ5=sQuery(id+"F0.wireOp",EDGE,"E52");var subQ7=makeQuery(id+"F0.imprint","INTERSECT",VERTEX,{"derivedFrom":[subQ3,subQ5]});Q34=makeQuery(id+"F0.imprint","IMPRINT",FACE,{"disambiguationData":[TD([[makeQuery(id+"F0.imprint","IMPRINT",EDGE,{"disambiguationData":[TD([[subQ7,-1.0]])],"derivedFrom":subQ3}),1.0]])]});}
            var Q35;
            {var subQ3=sQuery(id+"F0.wireOp",EDGE,"E36");var subQ5=sQuery(id+"F0.wireOp",EDGE,"E51");var subQ7=makeQuery(id+"F0.imprint","INTERSECT",VERTEX,{"derivedFrom":[subQ3,subQ5]});Q35=makeQuery(id+"F0.imprint","IMPRINT",FACE,{"disambiguationData":[TD([[makeQuery(id+"F0.imprint","IMPRINT",EDGE,{"disambiguationData":[TD([[subQ7,-1.0]])],"derivedFrom":subQ3}),1.0]])]});}
            var Q36;
            {var subQ3=sQuery(id+"F0.wireOp",EDGE,"E36");var subQ5=sQuery(id+"F0.wireOp",EDGE,"E50");var subQ7=makeQuery(id+"F0.imprint","INTERSECT",VERTEX,{"derivedFrom":[subQ3,subQ5]});Q36=makeQuery(id+"F0.imprint","IMPRINT",FACE,{"disambiguationData":[TD([[makeQuery(id+"F0.imprint","IMPRINT",EDGE,{"disambiguationData":[TD([[subQ7,-1.0]])],"derivedFrom":subQ3}),1.0]])]});}
            var Q37;
            {var subQ3=sQuery(id+"F0.wireOp",EDGE,"E41");var subQ5=sQuery(id+"F0.wireOp",EDGE,"E48");var subQ7=makeQuery(id+"F0.imprint","INTERSECT",VERTEX,{"derivedFrom":[subQ3,subQ5]});Q37=makeQuery(id+"F0.imprint","IMPRINT",FACE,{"disambiguationData":[TD([[makeQuery(id+"F0.imprint","IMPRINT",EDGE,{"disambiguationData":[TD([[subQ7,-1.0]])],"derivedFrom":subQ3}),1.0]])]});}
            var Q38;
            {var subQ3=sQuery(id+"F0.wireOp",EDGE,"E41");var subQ5=sQuery(id+"F0.wireOp",EDGE,"E49");var subQ7=makeQuery(id+"F0.imprint","INTERSECT",VERTEX,{"derivedFrom":[subQ3,subQ5]});Q38=makeQuery(id+"F0.imprint","IMPRINT",FACE,{"disambiguationData":[TD([[makeQuery(id+"F0.imprint","IMPRINT",EDGE,{"disambiguationData":[TD([[subQ7,-1.0]])],"derivedFrom":subQ3}),1.0]])]});}
            var Q39;
            {var subQ3=sQuery(id+"F0.wireOp",EDGE,"E41");var subQ5=sQuery(id+"F0.wireOp",EDGE,"E57");var subQ7=makeQuery(id+"F0.imprint","INTERSECT",VERTEX,{"derivedFrom":[subQ3,subQ5]});Q39=makeQuery(id+"F0.imprint","IMPRINT",FACE,{"disambiguationData":[TD([[makeQuery(id+"F0.imprint","IMPRINT",EDGE,{"disambiguationData":[TD([[subQ7,-1.0]])],"derivedFrom":subQ3}),1.0]])]});}
            var Q40;
            {var subQ0=sQuery(id+"F0.wireOp",EDGE,"E58");var subQ3=sQuery(id+"F0.wireOp",EDGE,"E41");var subQ4=makeQuery(id+"F0.imprint","INTERSECT",VERTEX,{"derivedFrom":[subQ3,subQ0]});Q40=makeQuery(id+"F0.imprint","IMPRINT",FACE,{"disambiguationData":[TD([[makeQuery(id+"F0.imprint","IMPRINT",EDGE,{"disambiguationData":[TD([[subQ4,-1.0]])],"derivedFrom":subQ3}),1.0]])]});}
            extrude(context, id + "F6", {"entities" : qUnion([Q0, Q1, Q2, Q3, Q4, Q5, Q6, Q7, Q8, Q9, Q10, Q11, Q12, Q13, Q14, Q15, Q16, Q17, Q18, Q19, Q20, Q21, Q22, Q23, Q24, Q25, Q26, Q27, Q28, Q29, Q30, Q31, Q32, Q33, Q34, Q35, Q36, Q37, Q38, Q39, Q40]), "endBound" : BoundingType.SYMMETRIC, "depth" : 9.96 * mm});
        }
        {
            var Q0;
            Q0=makeQuery(id+"F1.opExtrude","SWEPT_BODY",BODY,{"disambiguationData":[OSD([sQuery(id+"F0.wireOp",EDGE,"E36"),sQuery(id+"F0.wireOp",EDGE,"E37"),sQuery(id+"F0.wireOp",EDGE,"E38"),sQuery(id+"F0.wireOp",EDGE,"E41"),sQuery(id+"F0.wireOp",EDGE,"E42"),sQuery(id+"F0.wireOp",EDGE,"E45"),sQuery(id+"F0.wireOp",EDGE,"E46"),sQuery(id+"F0.wireOp",EDGE,"E47"),sQuery(id+"F0.wireOp",EDGE,"E48"),sQuery(id+"F0.wireOp",EDGE,"E59")])]});
            transform(context, id + "F7", {"entities" : qUnion([Q0]), "transformType" : TransformType.TRANSLATION_3D, "dx" : 0 * mm, "dy" : 125 * mm, "dz" : 0 * mm, "makeCopy" : false});
        }
        {
            var Q0;
            Q0=makeQuery(id+"F2.opExtrude","SWEPT_BODY",BODY,{"disambiguationData":[OSD([sQuery(id+"F0.wireOp",EDGE,"E36"),sQuery(id+"F0.wireOp",EDGE,"E37"),sQuery(id+"F0.wireOp",EDGE,"E38"),sQuery(id+"F0.wireOp",EDGE,"E41"),sQuery(id+"F0.wireOp",EDGE,"E42"),sQuery(id+"F0.wireOp",EDGE,"E45"),sQuery(id+"F0.wireOp",EDGE,"E46"),sQuery(id+"F0.wireOp",EDGE,"E47"),sQuery(id+"F0.wireOp",EDGE,"E48"),sQuery(id+"F0.wireOp",EDGE,"E54"),sQuery(id+"F0.wireOp",EDGE,"E57"),sQuery(id+"F0.wireOp",EDGE,"E59")])]});
            transform(context, id + "F8", {"entities" : qUnion([Q0]), "transformType" : TransformType.TRANSLATION_3D, "dx" : 0 * mm, "dy" : 100 * mm, "dz" : 0 * mm, "makeCopy" : false});
        }
        {
            var Q0;
            Q0=makeQuery(id+"F3.opExtrude","SWEPT_BODY",BODY,{"disambiguationData":[OSD([sQuery(id+"F0.wireOp",EDGE,"E36"),sQuery(id+"F0.wireOp",EDGE,"E37"),sQuery(id+"F0.wireOp",EDGE,"E38"),sQuery(id+"F0.wireOp",EDGE,"E41"),sQuery(id+"F0.wireOp",EDGE,"E42"),sQuery(id+"F0.wireOp",EDGE,"E45"),sQuery(id+"F0.wireOp",EDGE,"E46"),sQuery(id+"F0.wireOp",EDGE,"E47"),sQuery(id+"F0.wireOp",EDGE,"E48"),sQuery(id+"F0.wireOp",EDGE,"E50"),sQuery(id+"F0.wireOp",EDGE,"E53"),sQuery(id+"F0.wireOp",EDGE,"E54"),sQuery(id+"F0.wireOp",EDGE,"E57"),sQuery(id+"F0.wireOp",EDGE,"E59")])]});
            transform(context, id + "F9", {"entities" : qUnion([Q0]), "transformType" : TransformType.TRANSLATION_3D, "dx" : 0 * mm, "dy" : 75 * mm, "dz" : 0 * mm, "makeCopy" : false});
        }
        {
            var Q0;
            Q0=makeQuery(id+"F4.opExtrude","SWEPT_BODY",BODY,{"disambiguationData":[OSD([sQuery(id+"F0.wireOp",EDGE,"E36"),sQuery(id+"F0.wireOp",EDGE,"E37"),sQuery(id+"F0.wireOp",EDGE,"E38"),sQuery(id+"F0.wireOp",EDGE,"E40"),sQuery(id+"F0.wireOp",EDGE,"E41"),sQuery(id+"F0.wireOp",EDGE,"E42"),sQuery(id+"F0.wireOp",EDGE,"E45"),sQuery(id+"F0.wireOp",EDGE,"E46"),sQuery(id+"F0.wireOp",EDGE,"E47"),sQuery(id+"F0.wireOp",EDGE,"E48"),sQuery(id+"F0.wireOp",EDGE,"E50"),sQuery(id+"F0.wireOp",EDGE,"E51"),sQuery(id+"F0.wireOp",EDGE,"E52"),sQuery(id+"F0.wireOp",EDGE,"E54"),sQuery(id+"F0.wireOp",EDGE,"E57"),sQuery(id+"F0.wireOp",EDGE,"E59")])]});
            transform(context, id + "F10", {"entities" : qUnion([Q0]), "transformType" : TransformType.TRANSLATION_3D, "dx" : 0 * mm, "dy" : 50 * mm, "dz" : 0 * mm, "makeCopy" : false});
        }
        {
            var Q0;
            Q0=makeQuery(id+"F5.opExtrude","SWEPT_BODY",BODY,{"disambiguationData":[OSD([sQuery(id+"F0.wireOp",EDGE,"E36"),sQuery(id+"F0.wireOp",EDGE,"E37"),sQuery(id+"F0.wireOp",EDGE,"E38"),sQuery(id+"F0.wireOp",EDGE,"E41"),sQuery(id+"F0.wireOp",EDGE,"E42"),sQuery(id+"F0.wireOp",EDGE,"E45"),sQuery(id+"F0.wireOp",EDGE,"E46"),sQuery(id+"F0.wireOp",EDGE,"E47"),sQuery(id+"F0.wireOp",EDGE,"E48"),sQuery(id+"F0.wireOp",EDGE,"E50"),sQuery(id+"F0.wireOp",EDGE,"E54"),sQuery(id+"F0.wireOp",EDGE,"E57"),sQuery(id+"F0.wireOp",EDGE,"E59")])]});
            transform(context, id + "F11", {"entities" : qUnion([Q0]), "transformType" : TransformType.TRANSLATION_3D, "dx" : 0 * mm, "dy" : 25 * mm, "dz" : 0 * mm, "makeCopy" : false});
        }
        {
            var Q0;
            Q0=makeQuery(id+"F1.opExtrude","SWEPT_EDGE",EDGE,{"disambiguationData":[OSD([sQuery(id+"F0.wireOp",EDGE,"E45"),sQuery(id+"F0.wireOp",EDGE,"E48")])]});
            var Q1;
            Q1=makeQuery(id+"F1.opExtrude","SWEPT_EDGE",EDGE,{"disambiguationData":[OSD([sQuery(id+"F0.wireOp",EDGE,"E42"),sQuery(id+"F0.wireOp",EDGE,"E48")])]});
            var Q2;
            Q2=makeQuery(id+"F1.opExtrude","SWEPT_EDGE",EDGE,{"disambiguationData":[OSD([sQuery(id+"F0.wireOp",EDGE,"E41"),sQuery(id+"F0.wireOp",EDGE,"E48")])]});
            var Q3;
            Q3=makeQuery(id+"F1.opExtrude","SWEPT_EDGE",EDGE,{"disambiguationData":[OSD([sQuery(id+"F0.wireOp",EDGE,"E38"),sQuery(id+"F0.wireOp",EDGE,"E48")])]});
            var Q4;
            Q4=makeQuery(id+"F1.opExtrude","SWEPT_EDGE",EDGE,{"disambiguationData":[OSD([sQuery(id+"F0.wireOp",EDGE,"E45"),sQuery(id+"F0.wireOp",EDGE,"E59")])]});
            var Q5;
            Q5=makeQuery(id+"F1.opExtrude","SWEPT_EDGE",EDGE,{"disambiguationData":[OSD([sQuery(id+"F0.wireOp",EDGE,"E42"),sQuery(id+"F0.wireOp",EDGE,"E59")])]});
            var Q6;
            Q6=makeQuery(id+"F1.opExtrude","SWEPT_EDGE",EDGE,{"disambiguationData":[OSD([sQuery(id+"F0.wireOp",EDGE,"E41"),sQuery(id+"F0.wireOp",EDGE,"E59")])]});
            var Q7;
            Q7=makeQuery(id+"F1.opExtrude","SWEPT_EDGE",EDGE,{"disambiguationData":[OSD([sQuery(id+"F0.wireOp",EDGE,"E38"),sQuery(id+"F0.wireOp",EDGE,"E59")])]});
            var Q8;
            Q8=makeQuery(id+"F2.opExtrude","SWEPT_EDGE",EDGE,{"disambiguationData":[OSD([sQuery(id+"F0.wireOp",EDGE,"E45"),sQuery(id+"F0.wireOp",EDGE,"E48")])]});
            var Q9;
            Q9=makeQuery(id+"F2.opExtrude","SWEPT_EDGE",EDGE,{"disambiguationData":[OSD([sQuery(id+"F0.wireOp",EDGE,"E42"),sQuery(id+"F0.wireOp",EDGE,"E48")])]});
            var Q10;
            Q10=makeQuery(id+"F2.opExtrude","SWEPT_EDGE",EDGE,{"disambiguationData":[OSD([sQuery(id+"F0.wireOp",EDGE,"E41"),sQuery(id+"F0.wireOp",EDGE,"E48")])]});
            var Q11;
            Q11=makeQuery(id+"F2.opExtrude","SWEPT_EDGE",EDGE,{"disambiguationData":[OSD([sQuery(id+"F0.wireOp",EDGE,"E38"),sQuery(id+"F0.wireOp",EDGE,"E48")])]});
            var Q12;
            Q12=makeQuery(id+"F2.opExtrude","SWEPT_EDGE",EDGE,{"disambiguationData":[OSD([sQuery(id+"F0.wireOp",EDGE,"E45"),sQuery(id+"F0.wireOp",EDGE,"E59")])]});
            var Q13;
            Q13=makeQuery(id+"F2.opExtrude","SWEPT_EDGE",EDGE,{"disambiguationData":[OSD([sQuery(id+"F0.wireOp",EDGE,"E42"),sQuery(id+"F0.wireOp",EDGE,"E59")])]});
            var Q14;
            Q14=makeQuery(id+"F2.opExtrude","SWEPT_EDGE",EDGE,{"disambiguationData":[OSD([sQuery(id+"F0.wireOp",EDGE,"E41"),sQuery(id+"F0.wireOp",EDGE,"E59")])]});
            var Q15;
            Q15=makeQuery(id+"F2.opExtrude","SWEPT_EDGE",EDGE,{"disambiguationData":[OSD([sQuery(id+"F0.wireOp",EDGE,"E38"),sQuery(id+"F0.wireOp",EDGE,"E59")])]});
            var Q16;
            Q16=makeQuery(id+"F3.opExtrude","SWEPT_EDGE",EDGE,{"disambiguationData":[OSD([sQuery(id+"F0.wireOp",EDGE,"E45"),sQuery(id+"F0.wireOp",EDGE,"E48")])]});
            var Q17;
            Q17=makeQuery(id+"F3.opExtrude","SWEPT_EDGE",EDGE,{"disambiguationData":[OSD([sQuery(id+"F0.wireOp",EDGE,"E42"),sQuery(id+"F0.wireOp",EDGE,"E48")])]});
            var Q18;
            Q18=makeQuery(id+"F3.opExtrude","SWEPT_EDGE",EDGE,{"disambiguationData":[OSD([sQuery(id+"F0.wireOp",EDGE,"E41"),sQuery(id+"F0.wireOp",EDGE,"E48")])]});
            var Q19;
            Q19=makeQuery(id+"F3.opExtrude","SWEPT_EDGE",EDGE,{"disambiguationData":[OSD([sQuery(id+"F0.wireOp",EDGE,"E38"),sQuery(id+"F0.wireOp",EDGE,"E48")])]});
            var Q20;
            Q20=makeQuery(id+"F3.opExtrude","SWEPT_EDGE",EDGE,{"disambiguationData":[OSD([sQuery(id+"F0.wireOp",EDGE,"E45"),sQuery(id+"F0.wireOp",EDGE,"E59")])]});
            var Q21;
            Q21=makeQuery(id+"F3.opExtrude","SWEPT_EDGE",EDGE,{"disambiguationData":[OSD([sQuery(id+"F0.wireOp",EDGE,"E42"),sQuery(id+"F0.wireOp",EDGE,"E59")])]});
            var Q22;
            Q22=makeQuery(id+"F3.opExtrude","SWEPT_EDGE",EDGE,{"disambiguationData":[OSD([sQuery(id+"F0.wireOp",EDGE,"E41"),sQuery(id+"F0.wireOp",EDGE,"E59")])]});
            var Q23;
            Q23=makeQuery(id+"F3.opExtrude","SWEPT_EDGE",EDGE,{"disambiguationData":[OSD([sQuery(id+"F0.wireOp",EDGE,"E38"),sQuery(id+"F0.wireOp",EDGE,"E59")])]});
            var Q24;
            Q24=makeQuery(id+"F3.opExtrude","SWEPT_EDGE",EDGE,{"disambiguationData":[OSD([sQuery(id+"F0.wireOp",EDGE,"E42"),sQuery(id+"F0.wireOp",EDGE,"E53")])]});
            var Q25;
            Q25=makeQuery(id+"F3.opExtrude","SWEPT_EDGE",EDGE,{"disambiguationData":[OSD([sQuery(id+"F0.wireOp",EDGE,"E42"),sQuery(id+"F0.wireOp",EDGE,"E54")])]});
            var Q26;
            Q26=makeQuery(id+"F4.opExtrude","SWEPT_EDGE",EDGE,{"disambiguationData":[OSD([sQuery(id+"F0.wireOp",EDGE,"E45"),sQuery(id+"F0.wireOp",EDGE,"E48")])]});
            var Q27;
            Q27=makeQuery(id+"F4.opExtrude","SWEPT_EDGE",EDGE,{"disambiguationData":[OSD([sQuery(id+"F0.wireOp",EDGE,"E42"),sQuery(id+"F0.wireOp",EDGE,"E48")])]});
            var Q28;
            Q28=makeQuery(id+"F4.opExtrude","SWEPT_EDGE",EDGE,{"disambiguationData":[OSD([sQuery(id+"F0.wireOp",EDGE,"E41"),sQuery(id+"F0.wireOp",EDGE,"E48")])]});
            var Q29;
            Q29=makeQuery(id+"F4.opExtrude","SWEPT_EDGE",EDGE,{"disambiguationData":[OSD([sQuery(id+"F0.wireOp",EDGE,"E38"),sQuery(id+"F0.wireOp",EDGE,"E48")])]});
            var Q30;
            Q30=makeQuery(id+"F4.opExtrude","SWEPT_EDGE",EDGE,{"disambiguationData":[OSD([sQuery(id+"F0.wireOp",EDGE,"E45"),sQuery(id+"F0.wireOp",EDGE,"E59")])]});
            var Q31;
            Q31=makeQuery(id+"F4.opExtrude","SWEPT_EDGE",EDGE,{"disambiguationData":[OSD([sQuery(id+"F0.wireOp",EDGE,"E42"),sQuery(id+"F0.wireOp",EDGE,"E59")])]});
            var Q32;
            Q32=makeQuery(id+"F4.opExtrude","SWEPT_EDGE",EDGE,{"disambiguationData":[OSD([sQuery(id+"F0.wireOp",EDGE,"E41"),sQuery(id+"F0.wireOp",EDGE,"E59")])]});
            var Q33;
            Q33=makeQuery(id+"F4.opExtrude","SWEPT_EDGE",EDGE,{"disambiguationData":[OSD([sQuery(id+"F0.wireOp",EDGE,"E38"),sQuery(id+"F0.wireOp",EDGE,"E59")])]});
            var Q34;
            Q34=makeQuery(id+"F4.opExtrude","SWEPT_EDGE",EDGE,{"disambiguationData":[OSD([sQuery(id+"F0.wireOp",EDGE,"E38"),sQuery(id+"F0.wireOp",EDGE,"E51")])]});
            var Q35;
            Q35=makeQuery(id+"F4.opExtrude","SWEPT_EDGE",EDGE,{"disambiguationData":[OSD([sQuery(id+"F0.wireOp",EDGE,"E38"),sQuery(id+"F0.wireOp",EDGE,"E52")])]});
            var Q36;
            Q36=makeQuery(id+"F5.opExtrude","SWEPT_EDGE",EDGE,{"disambiguationData":[OSD([sQuery(id+"F0.wireOp",EDGE,"E45"),sQuery(id+"F0.wireOp",EDGE,"E48")])]});
            var Q37;
            Q37=makeQuery(id+"F5.opExtrude","SWEPT_EDGE",EDGE,{"disambiguationData":[OSD([sQuery(id+"F0.wireOp",EDGE,"E42"),sQuery(id+"F0.wireOp",EDGE,"E48")])]});
            var Q38;
            Q38=makeQuery(id+"F5.opExtrude","SWEPT_EDGE",EDGE,{"disambiguationData":[OSD([sQuery(id+"F0.wireOp",EDGE,"E41"),sQuery(id+"F0.wireOp",EDGE,"E48")])]});
            var Q39;
            Q39=makeQuery(id+"F5.opExtrude","SWEPT_EDGE",EDGE,{"disambiguationData":[OSD([sQuery(id+"F0.wireOp",EDGE,"E38"),sQuery(id+"F0.wireOp",EDGE,"E48")])]});
            var Q40;
            Q40=makeQuery(id+"F5.opExtrude","SWEPT_EDGE",EDGE,{"disambiguationData":[OSD([sQuery(id+"F0.wireOp",EDGE,"E45"),sQuery(id+"F0.wireOp",EDGE,"E59")])]});
            var Q41;
            Q41=makeQuery(id+"F5.opExtrude","SWEPT_EDGE",EDGE,{"disambiguationData":[OSD([sQuery(id+"F0.wireOp",EDGE,"E42"),sQuery(id+"F0.wireOp",EDGE,"E59")])]});
            var Q42;
            Q42=makeQuery(id+"F5.opExtrude","SWEPT_EDGE",EDGE,{"disambiguationData":[OSD([sQuery(id+"F0.wireOp",EDGE,"E41"),sQuery(id+"F0.wireOp",EDGE,"E59")])]});
            var Q43;
            Q43=makeQuery(id+"F5.opExtrude","SWEPT_EDGE",EDGE,{"disambiguationData":[OSD([sQuery(id+"F0.wireOp",EDGE,"E38"),sQuery(id+"F0.wireOp",EDGE,"E59")])]});
            var Q44;
            Q44=makeQuery(id+"F6.opExtrude","SWEPT_EDGE",EDGE,{"disambiguationData":[OSD([sQuery(id+"F0.wireOp",EDGE,"E45"),sQuery(id+"F0.wireOp",EDGE,"E48")])]});
            var Q45;
            Q45=makeQuery(id+"F6.opExtrude","SWEPT_EDGE",EDGE,{"disambiguationData":[OSD([sQuery(id+"F0.wireOp",EDGE,"E42"),sQuery(id+"F0.wireOp",EDGE,"E48")])]});
            var Q46;
            Q46=makeQuery(id+"F6.opExtrude","SWEPT_EDGE",EDGE,{"disambiguationData":[OSD([sQuery(id+"F0.wireOp",EDGE,"E41"),sQuery(id+"F0.wireOp",EDGE,"E48")])]});
            var Q47;
            Q47=makeQuery(id+"F6.opExtrude","SWEPT_EDGE",EDGE,{"disambiguationData":[OSD([sQuery(id+"F0.wireOp",EDGE,"E38"),sQuery(id+"F0.wireOp",EDGE,"E48")])]});
            var Q48;
            Q48=makeQuery(id+"F6.opExtrude","SWEPT_EDGE",EDGE,{"disambiguationData":[OSD([sQuery(id+"F0.wireOp",EDGE,"E45"),sQuery(id+"F0.wireOp",EDGE,"E59")])]});
            var Q49;
            Q49=makeQuery(id+"F6.opExtrude","SWEPT_EDGE",EDGE,{"disambiguationData":[OSD([sQuery(id+"F0.wireOp",EDGE,"E42"),sQuery(id+"F0.wireOp",EDGE,"E59")])]});
            var Q50;
            Q50=makeQuery(id+"F6.opExtrude","SWEPT_EDGE",EDGE,{"disambiguationData":[OSD([sQuery(id+"F0.wireOp",EDGE,"E41"),sQuery(id+"F0.wireOp",EDGE,"E59")])]});
            var Q51;
            Q51=makeQuery(id+"F6.opExtrude","SWEPT_EDGE",EDGE,{"disambiguationData":[OSD([sQuery(id+"F0.wireOp",EDGE,"E38"),sQuery(id+"F0.wireOp",EDGE,"E59")])]});
            fillet(context, id + "F12", {"entities" : qUnion([Q0, Q1, Q2, Q3, Q4, Q5, Q6, Q7, Q8, Q9, Q10, Q11, Q12, Q13, Q14, Q15, Q16, Q17, Q18, Q19, Q20, Q21, Q22, Q23, Q24, Q25, Q26, Q27, Q28, Q29, Q30, Q31, Q32, Q33, Q34, Q35, Q36, Q37, Q38, Q39, Q40, Q41, Q42, Q43, Q44, Q45, Q46, Q47, Q48, Q49, Q50, Q51]), "radius" : .2 * mm, "tangentPropagation" : true, "allowEdgeOverflow" : false});
        }
        {
            var Q0;
            Q0=makeQuery(id+"F1.opExtrude","CAP_FACE",FACE,{"disambiguationData":[OSD([sQuery(id+"F0.wireOp",EDGE,"E36"),sQuery(id+"F0.wireOp",EDGE,"E37"),sQuery(id+"F0.wireOp",EDGE,"E38"),sQuery(id+"F0.wireOp",EDGE,"E41"),sQuery(id+"F0.wireOp",EDGE,"E42"),sQuery(id+"F0.wireOp",EDGE,"E45"),sQuery(id+"F0.wireOp",EDGE,"E46"),sQuery(id+"F0.wireOp",EDGE,"E47"),sQuery(id+"F0.wireOp",EDGE,"E48"),sQuery(id+"F0.wireOp",EDGE,"E59")])],"isStart":false});
            var Q1;
            Q1=makeQuery(id+"F1.opExtrude","CAP_FACE",FACE,{"disambiguationData":[OSD([sQuery(id+"F0.wireOp",EDGE,"E36"),sQuery(id+"F0.wireOp",EDGE,"E37"),sQuery(id+"F0.wireOp",EDGE,"E38"),sQuery(id+"F0.wireOp",EDGE,"E41"),sQuery(id+"F0.wireOp",EDGE,"E42"),sQuery(id+"F0.wireOp",EDGE,"E45"),sQuery(id+"F0.wireOp",EDGE,"E46"),sQuery(id+"F0.wireOp",EDGE,"E47"),sQuery(id+"F0.wireOp",EDGE,"E48"),sQuery(id+"F0.wireOp",EDGE,"E59")])],"isStart":true});
            var Q2;
            Q2=makeQuery(id+"F2.opExtrude","CAP_FACE",FACE,{"disambiguationData":[OSD([sQuery(id+"F0.wireOp",EDGE,"E36"),sQuery(id+"F0.wireOp",EDGE,"E37"),sQuery(id+"F0.wireOp",EDGE,"E38"),sQuery(id+"F0.wireOp",EDGE,"E41"),sQuery(id+"F0.wireOp",EDGE,"E42"),sQuery(id+"F0.wireOp",EDGE,"E45"),sQuery(id+"F0.wireOp",EDGE,"E46"),sQuery(id+"F0.wireOp",EDGE,"E47"),sQuery(id+"F0.wireOp",EDGE,"E48"),sQuery(id+"F0.wireOp",EDGE,"E54"),sQuery(id+"F0.wireOp",EDGE,"E57"),sQuery(id+"F0.wireOp",EDGE,"E59")])],"isStart":false});
            var Q3;
            Q3=makeQuery(id+"F2.opExtrude","CAP_FACE",FACE,{"disambiguationData":[OSD([sQuery(id+"F0.wireOp",EDGE,"E36"),sQuery(id+"F0.wireOp",EDGE,"E37"),sQuery(id+"F0.wireOp",EDGE,"E38"),sQuery(id+"F0.wireOp",EDGE,"E41"),sQuery(id+"F0.wireOp",EDGE,"E42"),sQuery(id+"F0.wireOp",EDGE,"E45"),sQuery(id+"F0.wireOp",EDGE,"E46"),sQuery(id+"F0.wireOp",EDGE,"E47"),sQuery(id+"F0.wireOp",EDGE,"E48"),sQuery(id+"F0.wireOp",EDGE,"E54"),sQuery(id+"F0.wireOp",EDGE,"E57"),sQuery(id+"F0.wireOp",EDGE,"E59")])],"isStart":true});
            var Q4;
            {var subQ0=sQuery(id+"F0.wireOp",EDGE,"E54");Q4=makeQuery(id+"F2.opExtrude","SWEPT_FACE",FACE,{"disambiguationData":[OSD([subQ0]),TDD([makeQuery(id+"F0.imprint","IMPRINT",EDGE,{"disambiguationData":[TD([[makeQuery(id+"F0.imprint","INTERSECT",VERTEX,{"derivedFrom":[sQuery(id+"F0.wireOp",EDGE,"E36"),subQ0]}),1.0]])],"derivedFrom":subQ0})])]});}
            var Q5;
            {var subQ0=sQuery(id+"F0.wireOp",EDGE,"E54");Q5=makeQuery(id+"F2.opExtrude","SWEPT_FACE",FACE,{"disambiguationData":[OSD([subQ0]),TDD([makeQuery(id+"F0.imprint","IMPRINT",EDGE,{"disambiguationData":[TD([[makeQuery(id+"F0.imprint","INTERSECT",VERTEX,{"derivedFrom":[sQuery(id+"F0.wireOp",EDGE,"E41"),subQ0]}),1.0]])],"derivedFrom":subQ0})])]});}
            var Q6;
            {var subQ0=sQuery(id+"F0.wireOp",EDGE,"E57");Q6=makeQuery(id+"F2.opExtrude","SWEPT_FACE",FACE,{"disambiguationData":[OSD([subQ0]),TDD([makeQuery(id+"F0.imprint","IMPRINT",EDGE,{"disambiguationData":[TD([[makeQuery(id+"F0.imprint","INTERSECT",VERTEX,{"derivedFrom":[sQuery(id+"F0.wireOp",EDGE,"E41"),subQ0]}),1.0]])],"derivedFrom":subQ0})])]});}
            var Q7;
            {var subQ0=sQuery(id+"F0.wireOp",EDGE,"E57");Q7=makeQuery(id+"F2.opExtrude","SWEPT_FACE",FACE,{"disambiguationData":[OSD([subQ0]),TDD([makeQuery(id+"F0.imprint","IMPRINT",EDGE,{"disambiguationData":[TD([[makeQuery(id+"F0.imprint","INTERSECT",VERTEX,{"derivedFrom":[sQuery(id+"F0.wireOp",EDGE,"E36"),subQ0]}),1.0]])],"derivedFrom":subQ0})])]});}
            var Q8;
            Q8=makeQuery(id+"F3.opExtrude","CAP_FACE",FACE,{"disambiguationData":[OSD([sQuery(id+"F0.wireOp",EDGE,"E36"),sQuery(id+"F0.wireOp",EDGE,"E37"),sQuery(id+"F0.wireOp",EDGE,"E38"),sQuery(id+"F0.wireOp",EDGE,"E41"),sQuery(id+"F0.wireOp",EDGE,"E42"),sQuery(id+"F0.wireOp",EDGE,"E45"),sQuery(id+"F0.wireOp",EDGE,"E46"),sQuery(id+"F0.wireOp",EDGE,"E47"),sQuery(id+"F0.wireOp",EDGE,"E48"),sQuery(id+"F0.wireOp",EDGE,"E50"),sQuery(id+"F0.wireOp",EDGE,"E53"),sQuery(id+"F0.wireOp",EDGE,"E54"),sQuery(id+"F0.wireOp",EDGE,"E57"),sQuery(id+"F0.wireOp",EDGE,"E59")])],"isStart":false});
            var Q9;
            Q9=makeQuery(id+"F3.opExtrude","CAP_FACE",FACE,{"disambiguationData":[OSD([sQuery(id+"F0.wireOp",EDGE,"E36"),sQuery(id+"F0.wireOp",EDGE,"E37"),sQuery(id+"F0.wireOp",EDGE,"E38"),sQuery(id+"F0.wireOp",EDGE,"E41"),sQuery(id+"F0.wireOp",EDGE,"E42"),sQuery(id+"F0.wireOp",EDGE,"E45"),sQuery(id+"F0.wireOp",EDGE,"E46"),sQuery(id+"F0.wireOp",EDGE,"E47"),sQuery(id+"F0.wireOp",EDGE,"E48"),sQuery(id+"F0.wireOp",EDGE,"E50"),sQuery(id+"F0.wireOp",EDGE,"E53"),sQuery(id+"F0.wireOp",EDGE,"E54"),sQuery(id+"F0.wireOp",EDGE,"E57"),sQuery(id+"F0.wireOp",EDGE,"E59")])],"isStart":true});
            var Q10;
            {var subQ0=sQuery(id+"F0.wireOp",EDGE,"E57");Q10=makeQuery(id+"F3.opExtrude","SWEPT_FACE",FACE,{"disambiguationData":[OSD([subQ0]),TDD([makeQuery(id+"F0.imprint","IMPRINT",EDGE,{"disambiguationData":[TD([[makeQuery(id+"F0.imprint","INTERSECT",VERTEX,{"derivedFrom":[sQuery(id+"F0.wireOp",EDGE,"E46"),subQ0]}),-1.0]])],"derivedFrom":subQ0})])]});}
            var Q11;
            Q11=makeQuery(id+"F3.opExtrude","SWEPT_EDGE",EDGE,{"disambiguationData":[OSD([sQuery(id+"F0.wireOp",EDGE,"E46"),sQuery(id+"F0.wireOp",EDGE,"E54")])]});
            var Q12;
            Q12=makeQuery(id+"F3.opExtrude","SWEPT_EDGE",EDGE,{"disambiguationData":[OSD([sQuery(id+"F0.wireOp",EDGE,"E46"),sQuery(id+"F0.wireOp",EDGE,"E53")])]});
            var Q13;
            Q13=makeQuery(id+"F3.opExtrude","SWEPT_FACE",FACE,{"disambiguationData":[OSD([sQuery(id+"F0.wireOp",EDGE,"E50")])]});
            var Q14;
            {var subQ0=sQuery(id+"F0.wireOp",EDGE,"E54");Q14=makeQuery(id+"F3.opExtrude","SWEPT_FACE",FACE,{"disambiguationData":[OSD([subQ0]),TDD([makeQuery(id+"F0.imprint","IMPRINT",EDGE,{"disambiguationData":[TD([[makeQuery(id+"F0.imprint","INTERSECT",VERTEX,{"derivedFrom":[sQuery(id+"F0.wireOp",EDGE,"E36"),subQ0]}),1.0]])],"derivedFrom":subQ0})])]});}
            var Q15;
            {var subQ0=sQuery(id+"F0.wireOp",EDGE,"E57");Q15=makeQuery(id+"F3.opExtrude","SWEPT_FACE",FACE,{"disambiguationData":[OSD([subQ0]),TDD([makeQuery(id+"F0.imprint","IMPRINT",EDGE,{"disambiguationData":[TD([[makeQuery(id+"F0.imprint","INTERSECT",VERTEX,{"derivedFrom":[sQuery(id+"F0.wireOp",EDGE,"E36"),subQ0]}),1.0]])],"derivedFrom":subQ0})])]});}
            var Q16;
            Q16=makeQuery(id+"F4.opExtrude","CAP_FACE",FACE,{"disambiguationData":[OSD([sQuery(id+"F0.wireOp",EDGE,"E36"),sQuery(id+"F0.wireOp",EDGE,"E37"),sQuery(id+"F0.wireOp",EDGE,"E38"),sQuery(id+"F0.wireOp",EDGE,"E40"),sQuery(id+"F0.wireOp",EDGE,"E41"),sQuery(id+"F0.wireOp",EDGE,"E42"),sQuery(id+"F0.wireOp",EDGE,"E45"),sQuery(id+"F0.wireOp",EDGE,"E46"),sQuery(id+"F0.wireOp",EDGE,"E47"),sQuery(id+"F0.wireOp",EDGE,"E48"),sQuery(id+"F0.wireOp",EDGE,"E50"),sQuery(id+"F0.wireOp",EDGE,"E51"),sQuery(id+"F0.wireOp",EDGE,"E52"),sQuery(id+"F0.wireOp",EDGE,"E54"),sQuery(id+"F0.wireOp",EDGE,"E57"),sQuery(id+"F0.wireOp",EDGE,"E59")])],"isStart":false});
            var Q17;
            Q17=makeQuery(id+"F4.opExtrude","CAP_FACE",FACE,{"disambiguationData":[OSD([sQuery(id+"F0.wireOp",EDGE,"E36"),sQuery(id+"F0.wireOp",EDGE,"E37"),sQuery(id+"F0.wireOp",EDGE,"E38"),sQuery(id+"F0.wireOp",EDGE,"E40"),sQuery(id+"F0.wireOp",EDGE,"E41"),sQuery(id+"F0.wireOp",EDGE,"E42"),sQuery(id+"F0.wireOp",EDGE,"E45"),sQuery(id+"F0.wireOp",EDGE,"E46"),sQuery(id+"F0.wireOp",EDGE,"E47"),sQuery(id+"F0.wireOp",EDGE,"E48"),sQuery(id+"F0.wireOp",EDGE,"E50"),sQuery(id+"F0.wireOp",EDGE,"E51"),sQuery(id+"F0.wireOp",EDGE,"E52"),sQuery(id+"F0.wireOp",EDGE,"E54"),sQuery(id+"F0.wireOp",EDGE,"E57"),sQuery(id+"F0.wireOp",EDGE,"E59")])],"isStart":true});
            var Q18;
            Q18=makeQuery(id+"F4.opExtrude","SWEPT_FACE",FACE,{"disambiguationData":[OSD([sQuery(id+"F0.wireOp",EDGE,"E54")])]});
            var Q19;
            {var subQ0=sQuery(id+"F0.wireOp",EDGE,"E57");Q19=makeQuery(id+"F4.opExtrude","SWEPT_FACE",FACE,{"disambiguationData":[OSD([subQ0]),TDD([makeQuery(id+"F0.imprint","IMPRINT",EDGE,{"disambiguationData":[TD([[makeQuery(id+"F0.imprint","INTERSECT",VERTEX,{"derivedFrom":[sQuery(id+"F0.wireOp",EDGE,"E36"),subQ0]}),1.0]])],"derivedFrom":subQ0})])]});}
            var Q20;
            Q20=makeQuery(id+"F4.opExtrude","SWEPT_FACE",FACE,{"disambiguationData":[OSD([sQuery(id+"F0.wireOp",EDGE,"E50")])]});
            var Q21;
            Q21=makeQuery(id+"F4.opExtrude","SWEPT_FACE",FACE,{"disambiguationData":[OSD([sQuery(id+"F0.wireOp",EDGE,"E40")])]});
            var Q22;
            {var subQ0=sQuery(id+"F0.wireOp",EDGE,"E57");Q22=makeQuery(id+"F4.opExtrude","SWEPT_FACE",FACE,{"disambiguationData":[OSD([subQ0]),TDD([makeQuery(id+"F0.imprint","IMPRINT",EDGE,{"disambiguationData":[TD([[makeQuery(id+"F0.imprint","INTERSECT",VERTEX,{"derivedFrom":[sQuery(id+"F0.wireOp",EDGE,"E41"),subQ0]}),1.0]])],"derivedFrom":subQ0})])]});}
            var Q23;
            Q23=makeQuery(id+"F5.opExtrude","CAP_FACE",FACE,{"disambiguationData":[OSD([sQuery(id+"F0.wireOp",EDGE,"E36"),sQuery(id+"F0.wireOp",EDGE,"E37"),sQuery(id+"F0.wireOp",EDGE,"E38"),sQuery(id+"F0.wireOp",EDGE,"E41"),sQuery(id+"F0.wireOp",EDGE,"E42"),sQuery(id+"F0.wireOp",EDGE,"E45"),sQuery(id+"F0.wireOp",EDGE,"E46"),sQuery(id+"F0.wireOp",EDGE,"E47"),sQuery(id+"F0.wireOp",EDGE,"E48"),sQuery(id+"F0.wireOp",EDGE,"E50"),sQuery(id+"F0.wireOp",EDGE,"E54"),sQuery(id+"F0.wireOp",EDGE,"E57"),sQuery(id+"F0.wireOp",EDGE,"E59")])],"isStart":false});
            var Q24;
            Q24=makeQuery(id+"F5.opExtrude","CAP_FACE",FACE,{"disambiguationData":[OSD([sQuery(id+"F0.wireOp",EDGE,"E36"),sQuery(id+"F0.wireOp",EDGE,"E37"),sQuery(id+"F0.wireOp",EDGE,"E38"),sQuery(id+"F0.wireOp",EDGE,"E41"),sQuery(id+"F0.wireOp",EDGE,"E42"),sQuery(id+"F0.wireOp",EDGE,"E45"),sQuery(id+"F0.wireOp",EDGE,"E46"),sQuery(id+"F0.wireOp",EDGE,"E47"),sQuery(id+"F0.wireOp",EDGE,"E48"),sQuery(id+"F0.wireOp",EDGE,"E50"),sQuery(id+"F0.wireOp",EDGE,"E54"),sQuery(id+"F0.wireOp",EDGE,"E57"),sQuery(id+"F0.wireOp",EDGE,"E59")])],"isStart":true});
            var Q25;
            Q25=makeQuery(id+"F5.opExtrude","SWEPT_FACE",FACE,{"disambiguationData":[OSD([sQuery(id+"F0.wireOp",EDGE,"E50")])]});
            var Q26;
            Q26=makeQuery(id+"F5.opExtrude","SWEPT_FACE",FACE,{"disambiguationData":[OSD([sQuery(id+"F0.wireOp",EDGE,"E54")])]});
            var Q27;
            {var subQ0=sQuery(id+"F0.wireOp",EDGE,"E57");Q27=makeQuery(id+"F5.opExtrude","SWEPT_FACE",FACE,{"disambiguationData":[OSD([subQ0]),TDD([makeQuery(id+"F0.imprint","IMPRINT",EDGE,{"disambiguationData":[TD([[makeQuery(id+"F0.imprint","INTERSECT",VERTEX,{"derivedFrom":[sQuery(id+"F0.wireOp",EDGE,"E41"),subQ0]}),1.0]])],"derivedFrom":subQ0})])]});}
            var Q28;
            {var subQ0=sQuery(id+"F0.wireOp",EDGE,"E57");Q28=makeQuery(id+"F5.opExtrude","SWEPT_FACE",FACE,{"disambiguationData":[OSD([subQ0]),TDD([makeQuery(id+"F0.imprint","IMPRINT",EDGE,{"disambiguationData":[TD([[makeQuery(id+"F0.imprint","INTERSECT",VERTEX,{"derivedFrom":[sQuery(id+"F0.wireOp",EDGE,"E36"),subQ0]}),1.0]])],"derivedFrom":subQ0})])]});}
            var Q29;
            Q29=makeQuery(id+"F6.opExtrude","CAP_FACE",FACE,{"disambiguationData":[OSD([sQuery(id+"F0.wireOp",EDGE,"E36"),sQuery(id+"F0.wireOp",EDGE,"E37"),sQuery(id+"F0.wireOp",EDGE,"E38"),sQuery(id+"F0.wireOp",EDGE,"E41"),sQuery(id+"F0.wireOp",EDGE,"E42"),sQuery(id+"F0.wireOp",EDGE,"E45"),sQuery(id+"F0.wireOp",EDGE,"E46"),sQuery(id+"F0.wireOp",EDGE,"E47"),sQuery(id+"F0.wireOp",EDGE,"E48"),sQuery(id+"F0.wireOp",EDGE,"E50"),sQuery(id+"F0.wireOp",EDGE,"E54"),sQuery(id+"F0.wireOp",EDGE,"E57"),sQuery(id+"F0.wireOp",EDGE,"E59")])],"isStart":false});
            var Q30;
            Q30=makeQuery(id+"F6.opExtrude","CAP_FACE",FACE,{"disambiguationData":[OSD([sQuery(id+"F0.wireOp",EDGE,"E36"),sQuery(id+"F0.wireOp",EDGE,"E37"),sQuery(id+"F0.wireOp",EDGE,"E38"),sQuery(id+"F0.wireOp",EDGE,"E41"),sQuery(id+"F0.wireOp",EDGE,"E42"),sQuery(id+"F0.wireOp",EDGE,"E45"),sQuery(id+"F0.wireOp",EDGE,"E46"),sQuery(id+"F0.wireOp",EDGE,"E47"),sQuery(id+"F0.wireOp",EDGE,"E48"),sQuery(id+"F0.wireOp",EDGE,"E50"),sQuery(id+"F0.wireOp",EDGE,"E54"),sQuery(id+"F0.wireOp",EDGE,"E57"),sQuery(id+"F0.wireOp",EDGE,"E59")])],"isStart":true});
            var Q31;
            Q31=makeQuery(id+"F6.opExtrude","SWEPT_FACE",FACE,{"disambiguationData":[OSD([sQuery(id+"F0.wireOp",EDGE,"E50")])]});
            var Q32;
            Q32=makeQuery(id+"F6.opExtrude","SWEPT_FACE",FACE,{"disambiguationData":[OSD([sQuery(id+"F0.wireOp",EDGE,"E54")])]});
            var Q33;
            {var subQ0=sQuery(id+"F0.wireOp",EDGE,"E57");Q33=makeQuery(id+"F6.opExtrude","SWEPT_FACE",FACE,{"disambiguationData":[OSD([subQ0]),TDD([makeQuery(id+"F0.imprint","IMPRINT",EDGE,{"disambiguationData":[TD([[makeQuery(id+"F0.imprint","INTERSECT",VERTEX,{"derivedFrom":[sQuery(id+"F0.wireOp",EDGE,"E41"),subQ0]}),1.0]])],"derivedFrom":subQ0})])]});}
            var Q34;
            {var subQ0=sQuery(id+"F0.wireOp",EDGE,"E57");Q34=makeQuery(id+"F6.opExtrude","SWEPT_FACE",FACE,{"disambiguationData":[OSD([subQ0]),TDD([makeQuery(id+"F0.imprint","IMPRINT",EDGE,{"disambiguationData":[TD([[makeQuery(id+"F0.imprint","INTERSECT",VERTEX,{"derivedFrom":[sQuery(id+"F0.wireOp",EDGE,"E36"),subQ0]}),1.0]])],"derivedFrom":subQ0})])]});}
            var Q35;
            Q35=makeQuery(id+"F1.opExtrude","SWEPT_FACE",FACE,{"disambiguationData":[OSD([sQuery(id+"F0.wireOp",EDGE,"E37")])]});
            var Q36;
            Q36=makeQuery(id+"F2.opExtrude","SWEPT_FACE",FACE,{"disambiguationData":[OSD([sQuery(id+"F0.wireOp",EDGE,"E37")])]});
            var Q37;
            Q37=makeQuery(id+"F3.opExtrude","SWEPT_FACE",FACE,{"disambiguationData":[OSD([sQuery(id+"F0.wireOp",EDGE,"E37")])]});
            var Q38;
            Q38=makeQuery(id+"F4.opExtrude","SWEPT_FACE",FACE,{"disambiguationData":[OSD([sQuery(id+"F0.wireOp",EDGE,"E37")])]});
            var Q39;
            Q39=makeQuery(id+"F5.opExtrude","SWEPT_FACE",FACE,{"disambiguationData":[OSD([sQuery(id+"F0.wireOp",EDGE,"E37")])]});
            var Q40;
            Q40=makeQuery(id+"F6.opExtrude","SWEPT_FACE",FACE,{"disambiguationData":[OSD([sQuery(id+"F0.wireOp",EDGE,"E37")])]});
            var Q41;
            Q41=makeQuery(id+"F1.opExtrude","SWEPT_FACE",FACE,{"disambiguationData":[OSD([sQuery(id+"F0.wireOp",EDGE,"E47")])]});
            var Q42;
            Q42=makeQuery(id+"F2.opExtrude","SWEPT_FACE",FACE,{"disambiguationData":[OSD([sQuery(id+"F0.wireOp",EDGE,"E47")])]});
            var Q43;
            Q43=makeQuery(id+"F3.opExtrude","SWEPT_FACE",FACE,{"disambiguationData":[OSD([sQuery(id+"F0.wireOp",EDGE,"E47")])]});
            var Q44;
            Q44=makeQuery(id+"F4.opExtrude","SWEPT_FACE",FACE,{"disambiguationData":[OSD([sQuery(id+"F0.wireOp",EDGE,"E47")])]});
            var Q45;
            Q45=makeQuery(id+"F5.opExtrude","SWEPT_FACE",FACE,{"disambiguationData":[OSD([sQuery(id+"F0.wireOp",EDGE,"E47")])]});
            var Q46;
            Q46=makeQuery(id+"F6.opExtrude","SWEPT_FACE",FACE,{"disambiguationData":[OSD([sQuery(id+"F0.wireOp",EDGE,"E47")])]});
            fillet(context, id + "F13", {"entities" : qUnion([Q0, Q1, Q2, Q3, Q4, Q5, Q6, Q7, Q8, Q9, Q10, Q11, Q12, Q13, Q14, Q15, Q16, Q17, Q18, Q19, Q20, Q21, Q22, Q23, Q24, Q25, Q26, Q27, Q28, Q29, Q30, Q31, Q32, Q33, Q34, Q35, Q36, Q37, Q38, Q39, Q40, Q41, Q42, Q43, Q44, Q45, Q46]), "radius" : .8 * mm, "tangentPropagation" : true, "allowEdgeOverflow" : false});
        }
    });
